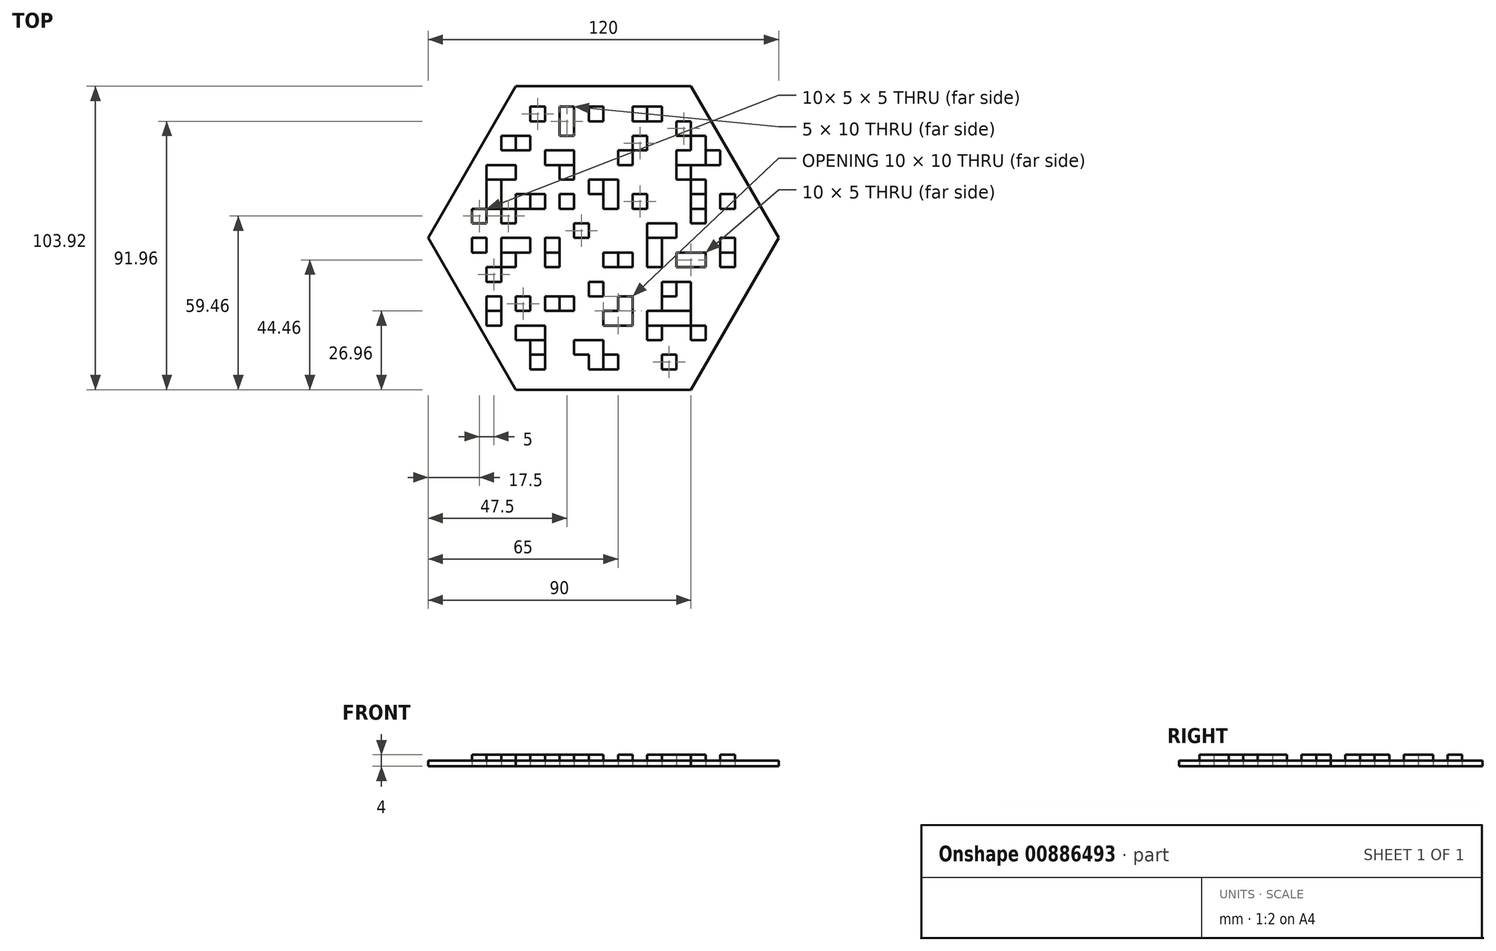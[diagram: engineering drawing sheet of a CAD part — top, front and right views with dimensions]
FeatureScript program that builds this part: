
annotation { "Feature Type Name" : "Feature", "Feature Type Description" : "" }
export const myFeature = defineFeature(function(context is Context, id is Id, definition is map)
    precondition{}
    {
        {
            var Q0;
            Q0=qCreatedBy(makeId("Top.planeOp"),FACE);
            var sketch = newSketch(context, id + "F0", { "sketchPlane" : qUnion([Q0])});
            skCircle(sketch, "E0.cCircle", {"center": v(0, 0) * mm, "radius": 60 * mm, "construction": true});
            skLineSegment(sketch, "E0.0", {"start": v(-60, 0) * mm, "end": v(-30, 51.96) * mm});
            skLineSegment(sketch, "E0.1", {"start": v(-30, 51.96) * mm, "end": v(30, 51.96) * mm});
            skLineSegment(sketch, "E0.2", {"start": v(30, 51.96) * mm, "end": v(60, 0) * mm});
            skLineSegment(sketch, "E0.3", {"start": v(60, 0) * mm, "end": v(30, -51.96) * mm});
            skLineSegment(sketch, "E0.4", {"start": v(30, -51.96) * mm, "end": v(-30, -51.96) * mm});
            skLineSegment(sketch, "E0.5", {"start": v(-30, -51.96) * mm, "end": v(-60, 0) * mm});
            skLineSegment(sketch, "E1", {"start": v(-60, 0) * mm, "end": v(60, 0) * mm});
            skLineSegment(sketch, "E2.0.9.0", {"start": v(-34.02, 45) * mm, "end": v(34.02, 45) * mm});
            skLineSegment(sketch, "E3.trimOffspring", {"start": v(-34.02, -45) * mm, "end": v(34.02, -45) * mm});
            skLineSegment(sketch, "E4.trimOffspring", {"start": v(-36.9, -40) * mm, "end": v(36.9, -40) * mm});
            skLineSegment(sketch, "E5.trimOffspring", {"start": v(-39.8, -35) * mm, "end": v(39.8, -35) * mm});
            skLineSegment(sketch, "E6.trimOffspring", {"start": v(-42.68, -30) * mm, "end": v(42.68, -30) * mm});
            skLineSegment(sketch, "E7.trimOffspring", {"start": v(-45.57, -25) * mm, "end": v(45.57, -25) * mm});
            skLineSegment(sketch, "E8.trimOffspring", {"start": v(-48.45, -20) * mm, "end": v(48.45, -20) * mm});
            skLineSegment(sketch, "E9.trimOffspring", {"start": v(-51.34, -15) * mm, "end": v(51.34, -15) * mm});
            skLineSegment(sketch, "E10.trimOffspring", {"start": v(-54.23, -10) * mm, "end": v(54.23, -10) * mm});
            skLineSegment(sketch, "E11.trimOffspring", {"start": v(-57.11, -5) * mm, "end": v(57.11, -5) * mm});
            skLineSegment(sketch, "E12.trimOffspring", {"start": v(-57.11, 5) * mm, "end": v(57.11, 5) * mm});
            skLineSegment(sketch, "E13.trimOffspring", {"start": v(-54.23, 10) * mm, "end": v(54.23, 10) * mm});
            skLineSegment(sketch, "E14.trimOffspring", {"start": v(-51.34, 15) * mm, "end": v(51.34, 15) * mm});
            skLineSegment(sketch, "E15.trimOffspring", {"start": v(-48.45, 20) * mm, "end": v(48.45, 20) * mm});
            skLineSegment(sketch, "E16.trimOffspring", {"start": v(-45.57, 25) * mm, "end": v(45.57, 25) * mm});
            skLineSegment(sketch, "E17.trimOffspring", {"start": v(-42.68, 30) * mm, "end": v(42.68, 30) * mm});
            skLineSegment(sketch, "E18.trimOffspring", {"start": v(-39.8, 35) * mm, "end": v(39.8, 35) * mm});
            skLineSegment(sketch, "E19.trimOffspring", {"start": v(-36.9, 40) * mm, "end": v(36.9, 40) * mm});
            skLineSegment(sketch, "E20", {"start": v(0, 51.96) * mm, "end": v(0, -51.96) * mm});
            skLineSegment(sketch, "E21.1.0.0", {"start": v(5, 51.96) * mm, "end": v(5, -51.96) * mm});
            skLineSegment(sketch, "E21.2.0.0", {"start": v(10, 51.96) * mm, "end": v(10, -51.96) * mm});
            skLineSegment(sketch, "E21.3.0.0", {"start": v(15, 51.96) * mm, "end": v(15, -51.96) * mm});
            skLineSegment(sketch, "E21.4.0.0", {"start": v(20, 51.96) * mm, "end": v(20, -51.96) * mm});
            skLineSegment(sketch, "E21.5.0.0", {"start": v(25, 51.96) * mm, "end": v(25, -51.96) * mm});
            skLineSegment(sketch, "E21.6.0.0", {"start": v(30, 51.96) * mm, "end": v(30, -51.96) * mm});
            skLineSegment(sketch, "E21.direction1", {"start": v(0, -51.96) * mm, "end": v(5, -51.96) * mm, "construction": true});
            skLineSegment(sketch, "E22.1.0.0", {"start": v(-5, 51.96) * mm, "end": v(-5, -51.96) * mm});
            skLineSegment(sketch, "E22.2.0.0", {"start": v(-10, 51.96) * mm, "end": v(-10, -51.96) * mm});
            skLineSegment(sketch, "E22.3.0.0", {"start": v(-15, 51.96) * mm, "end": v(-15, -51.96) * mm});
            skLineSegment(sketch, "E22.4.0.0", {"start": v(-20, 51.96) * mm, "end": v(-20, -51.96) * mm});
            skLineSegment(sketch, "E22.5.0.0", {"start": v(-25, 51.96) * mm, "end": v(-25, -51.96) * mm});
            skLineSegment(sketch, "E22.6.0.0", {"start": v(-30, 51.96) * mm, "end": v(-30, -51.96) * mm});
            skLineSegment(sketch, "E22.8.0.0", {"start": v(-40, 34.64) * mm, "end": v(-40, -34.64) * mm});
            skLineSegment(sketch, "E22.9.0.0", {"start": v(-45, 25.98) * mm, "end": v(-45, -25.98) * mm});
            skLineSegment(sketch, "E22.direction1", {"start": v(0, -51.96) * mm, "end": v(-5, -51.96) * mm, "construction": true});
            skLineSegment(sketch, "E23.trimOffspring", {"start": v(-35, 43.3) * mm, "end": v(-35, -43.3) * mm});
            skLineSegment(sketch, "E24.trimOffspring", {"start": v(45, 25.98) * mm, "end": v(45, -25.98) * mm});
            skLineSegment(sketch, "E25.trimOffspring", {"start": v(40, 34.64) * mm, "end": v(40, -34.64) * mm});
            skLineSegment(sketch, "E26.trimOffspring", {"start": v(35, 43.3) * mm, "end": v(35, -43.3) * mm});
            skSolve(sketch);
        }
        {
            var Q0;
            {var subQ0=sQuery(id+"F0.wireOp",EDGE,"E21.5.0.0");var subQ1=sQuery(id+"F0.wireOp",EDGE,"E1");var subQ2=makeQuery(id+"F0.imprint","INTERSECT",VERTEX,{"derivedFrom":[subQ1,subQ0]});Q0=makeQuery(id+"F0.imprint","IMPRINT",FACE,{"disambiguationData":[TD([[makeQuery(id+"F0.imprint","IMPRINT",EDGE,{"disambiguationData":[TD([[subQ2,-1.0]])],"derivedFrom":subQ1}),1.0]])]});}
            var Q1;
            {var subQ0=sQuery(id+"F0.wireOp",EDGE,"E21.2.0.0");var subQ1=sQuery(id+"F0.wireOp",EDGE,"E13.trimOffspring");var subQ2=makeQuery(id+"F0.imprint","INTERSECT",VERTEX,{"derivedFrom":[subQ1,subQ0]});Q1=makeQuery(id+"F0.imprint","IMPRINT",FACE,{"disambiguationData":[TD([[makeQuery(id+"F0.imprint","IMPRINT",EDGE,{"disambiguationData":[TD([[subQ2,-1.0]])],"derivedFrom":subQ1}),1.0]])]});}
            var Q2;
            {var subQ0=sQuery(id+"F0.wireOp",EDGE,"E21.1.0.0");var subQ1=sQuery(id+"F0.wireOp",EDGE,"E12.trimOffspring");var subQ2=makeQuery(id+"F0.imprint","INTERSECT",VERTEX,{"derivedFrom":[subQ1,subQ0]});Q2=makeQuery(id+"F0.imprint","IMPRINT",FACE,{"disambiguationData":[TD([[makeQuery(id+"F0.imprint","IMPRINT",EDGE,{"disambiguationData":[TD([[subQ2,-1.0]])],"derivedFrom":subQ1}),1.0]])]});}
            var Q3;
            {var subQ0=sQuery(id+"F0.wireOp",EDGE,"E21.1.0.0");var subQ1=sQuery(id+"F0.wireOp",EDGE,"E13.trimOffspring");var subQ2=makeQuery(id+"F0.imprint","INTERSECT",VERTEX,{"derivedFrom":[subQ1,subQ0]});Q3=makeQuery(id+"F0.imprint","IMPRINT",FACE,{"disambiguationData":[TD([[makeQuery(id+"F0.imprint","IMPRINT",EDGE,{"disambiguationData":[TD([[subQ2,-1.0]])],"derivedFrom":subQ1}),1.0]])]});}
            var Q4;
            {var subQ0=sQuery(id+"F0.wireOp",EDGE,"E22.4.0.0");var subQ1=sQuery(id+"F0.wireOp",EDGE,"E16.trimOffspring");var subQ2=makeQuery(id+"F0.imprint","INTERSECT",VERTEX,{"derivedFrom":[subQ1,subQ0]});Q4=makeQuery(id+"F0.imprint","IMPRINT",FACE,{"disambiguationData":[TD([[makeQuery(id+"F0.imprint","IMPRINT",EDGE,{"disambiguationData":[TD([[subQ2,-1.0]])],"derivedFrom":subQ1}),1.0]])]});}
            var Q5;
            {var subQ0=sQuery(id+"F0.wireOp",EDGE,"E21.2.0.0");var subQ1=sQuery(id+"F0.wireOp",EDGE,"E12.trimOffspring");var subQ2=makeQuery(id+"F0.imprint","INTERSECT",VERTEX,{"derivedFrom":[subQ1,subQ0]});Q5=makeQuery(id+"F0.imprint","IMPRINT",FACE,{"disambiguationData":[TD([[makeQuery(id+"F0.imprint","IMPRINT",EDGE,{"disambiguationData":[TD([[subQ2,-1.0]])],"derivedFrom":subQ1}),1.0]])]});}
            var Q6;
            {var subQ0=sQuery(id+"F0.wireOp",EDGE,"E21.2.0.0");var subQ1=sQuery(id+"F0.wireOp",EDGE,"E17.trimOffspring");var subQ2=makeQuery(id+"F0.imprint","INTERSECT",VERTEX,{"derivedFrom":[subQ1,subQ0]});Q6=makeQuery(id+"F0.imprint","IMPRINT",FACE,{"disambiguationData":[TD([[makeQuery(id+"F0.imprint","IMPRINT",EDGE,{"disambiguationData":[TD([[subQ2,-1.0]])],"derivedFrom":subQ1}),1.0]])]});}
            var Q7;
            {var subQ0=sQuery(id+"F0.wireOp",EDGE,"E20");var subQ1=sQuery(id+"F0.wireOp",EDGE,"E8.trimOffspring");var subQ2=makeQuery(id+"F0.imprint","INTERSECT",VERTEX,{"derivedFrom":[subQ1,subQ0]});Q7=makeQuery(id+"F0.imprint","IMPRINT",FACE,{"disambiguationData":[TD([[makeQuery(id+"F0.imprint","IMPRINT",EDGE,{"disambiguationData":[TD([[subQ2,-1.0]])],"derivedFrom":subQ1}),1.0]])]});}
            var Q8;
            {var subQ0=sQuery(id+"F0.wireOp",EDGE,"E21.1.0.0");var subQ1=sQuery(id+"F0.wireOp",EDGE,"E4.trimOffspring");var subQ2=makeQuery(id+"F0.imprint","INTERSECT",VERTEX,{"derivedFrom":[subQ1,subQ0]});Q8=makeQuery(id+"F0.imprint","IMPRINT",FACE,{"disambiguationData":[TD([[makeQuery(id+"F0.imprint","IMPRINT",EDGE,{"disambiguationData":[TD([[subQ2,-1.0]])],"derivedFrom":subQ1}),1.0]])]});}
            var Q9;
            {var subQ0=sQuery(id+"F0.wireOp",EDGE,"E21.2.0.0");var subQ1=sQuery(id+"F0.wireOp",EDGE,"E1");var subQ2=makeQuery(id+"F0.imprint","INTERSECT",VERTEX,{"derivedFrom":[subQ1,subQ0]});Q9=makeQuery(id+"F0.imprint","IMPRINT",FACE,{"disambiguationData":[TD([[makeQuery(id+"F0.imprint","IMPRINT",EDGE,{"disambiguationData":[TD([[subQ2,-1.0]])],"derivedFrom":subQ1}),-1.0]])]});}
            var Q10;
            {var subQ0=sQuery(id+"F0.wireOp",EDGE,"E21.3.0.0");var subQ1=sQuery(id+"F0.wireOp",EDGE,"E13.trimOffspring");var subQ2=makeQuery(id+"F0.imprint","INTERSECT",VERTEX,{"derivedFrom":[subQ1,subQ0]});Q10=makeQuery(id+"F0.imprint","IMPRINT",FACE,{"disambiguationData":[TD([[makeQuery(id+"F0.imprint","IMPRINT",EDGE,{"disambiguationData":[TD([[subQ2,-1.0]])],"derivedFrom":subQ1}),1.0]])]});}
            var Q11;
            {var subQ0=sQuery(id+"F0.wireOp",EDGE,"E22.2.0.0");var subQ1=sQuery(id+"F0.wireOp",EDGE,"E6.trimOffspring");var subQ2=makeQuery(id+"F0.imprint","INTERSECT",VERTEX,{"derivedFrom":[subQ1,subQ0]});Q11=makeQuery(id+"F0.imprint","IMPRINT",FACE,{"disambiguationData":[TD([[makeQuery(id+"F0.imprint","IMPRINT",EDGE,{"disambiguationData":[TD([[subQ2,-1.0]])],"derivedFrom":subQ1}),1.0]])]});}
            var Q12;
            {var subQ0=sQuery(id+"F0.wireOp",EDGE,"E21.1.0.0");var subQ1=sQuery(id+"F0.wireOp",EDGE,"E1");var subQ2=makeQuery(id+"F0.imprint","INTERSECT",VERTEX,{"derivedFrom":[subQ1,subQ0]});Q12=makeQuery(id+"F0.imprint","IMPRINT",FACE,{"disambiguationData":[TD([[makeQuery(id+"F0.imprint","IMPRINT",EDGE,{"disambiguationData":[TD([[subQ2,-1.0]])],"derivedFrom":subQ1}),-1.0]])]});}
            var Q13;
            {var subQ0=sQuery(id+"F0.wireOp",EDGE,"E21.2.0.0");var subQ1=sQuery(id+"F0.wireOp",EDGE,"E10.trimOffspring");var subQ2=makeQuery(id+"F0.imprint","INTERSECT",VERTEX,{"derivedFrom":[subQ1,subQ0]});Q13=makeQuery(id+"F0.imprint","IMPRINT",FACE,{"disambiguationData":[TD([[makeQuery(id+"F0.imprint","IMPRINT",EDGE,{"disambiguationData":[TD([[subQ2,-1.0]])],"derivedFrom":subQ1}),1.0]])]});}
            var Q14;
            {var subQ0=sQuery(id+"F0.wireOp",EDGE,"E22.3.0.0");var subQ1=sQuery(id+"F0.wireOp",EDGE,"E2.0.9.0");var subQ2=makeQuery(id+"F0.imprint","INTERSECT",VERTEX,{"derivedFrom":[subQ1,subQ0]});Q14=makeQuery(id+"F0.imprint","IMPRINT",FACE,{"disambiguationData":[TD([[makeQuery(id+"F0.imprint","IMPRINT",EDGE,{"disambiguationData":[TD([[subQ2,-1.0]])],"derivedFrom":subQ1}),-1.0]])]});}
            var Q15;
            {var subQ0=sQuery(id+"F0.wireOp",EDGE,"E22.3.0.0");var subQ1=sQuery(id+"F0.wireOp",EDGE,"E12.trimOffspring");var subQ2=makeQuery(id+"F0.imprint","INTERSECT",VERTEX,{"derivedFrom":[subQ1,subQ0]});Q15=makeQuery(id+"F0.imprint","IMPRINT",FACE,{"disambiguationData":[TD([[makeQuery(id+"F0.imprint","IMPRINT",EDGE,{"disambiguationData":[TD([[subQ2,-1.0]])],"derivedFrom":subQ1}),1.0]])]});}
            var Q16;
            {var subQ0=sQuery(id+"F0.wireOp",EDGE,"E20");var subQ1=sQuery(id+"F0.wireOp",EDGE,"E16.trimOffspring");var subQ2=makeQuery(id+"F0.imprint","INTERSECT",VERTEX,{"derivedFrom":[subQ1,subQ0]});Q16=makeQuery(id+"F0.imprint","IMPRINT",FACE,{"disambiguationData":[TD([[makeQuery(id+"F0.imprint","IMPRINT",EDGE,{"disambiguationData":[TD([[subQ2,-1.0]])],"derivedFrom":subQ1}),1.0]])]});}
            var Q17;
            {var subQ0=sQuery(id+"F0.wireOp",EDGE,"E20");var subQ1=sQuery(id+"F0.wireOp",EDGE,"E18.trimOffspring");var subQ2=makeQuery(id+"F0.imprint","INTERSECT",VERTEX,{"derivedFrom":[subQ1,subQ0]});Q17=makeQuery(id+"F0.imprint","IMPRINT",FACE,{"disambiguationData":[TD([[makeQuery(id+"F0.imprint","IMPRINT",EDGE,{"disambiguationData":[TD([[subQ2,-1.0]])],"derivedFrom":subQ1}),1.0]])]});}
            var Q18;
            {var subQ0=sQuery(id+"F0.wireOp",EDGE,"E20");var subQ1=sQuery(id+"F0.wireOp",EDGE,"E5.trimOffspring");var subQ2=makeQuery(id+"F0.imprint","INTERSECT",VERTEX,{"derivedFrom":[subQ1,subQ0]});Q18=makeQuery(id+"F0.imprint","IMPRINT",FACE,{"disambiguationData":[TD([[makeQuery(id+"F0.imprint","IMPRINT",EDGE,{"disambiguationData":[TD([[subQ2,-1.0]])],"derivedFrom":subQ1}),1.0]])]});}
            var Q19;
            {var subQ0=sQuery(id+"F0.wireOp",EDGE,"E21.2.0.0");var subQ1=sQuery(id+"F0.wireOp",EDGE,"E8.trimOffspring");var subQ2=makeQuery(id+"F0.imprint","INTERSECT",VERTEX,{"derivedFrom":[subQ1,subQ0]});Q19=makeQuery(id+"F0.imprint","IMPRINT",FACE,{"disambiguationData":[TD([[makeQuery(id+"F0.imprint","IMPRINT",EDGE,{"disambiguationData":[TD([[subQ2,-1.0]])],"derivedFrom":subQ1}),1.0]])]});}
            var Q20;
            {var subQ0=sQuery(id+"F0.wireOp",EDGE,"E22.2.0.0");var subQ1=sQuery(id+"F0.wireOp",EDGE,"E10.trimOffspring");var subQ2=makeQuery(id+"F0.imprint","INTERSECT",VERTEX,{"derivedFrom":[subQ1,subQ0]});Q20=makeQuery(id+"F0.imprint","IMPRINT",FACE,{"disambiguationData":[TD([[makeQuery(id+"F0.imprint","IMPRINT",EDGE,{"disambiguationData":[TD([[subQ2,-1.0]])],"derivedFrom":subQ1}),1.0]])]});}
            var Q21;
            {var subQ0=sQuery(id+"F0.wireOp",EDGE,"E22.1.0.0");var subQ1=sQuery(id+"F0.wireOp",EDGE,"E9.trimOffspring");var subQ2=makeQuery(id+"F0.imprint","INTERSECT",VERTEX,{"derivedFrom":[subQ1,subQ0]});Q21=makeQuery(id+"F0.imprint","IMPRINT",FACE,{"disambiguationData":[TD([[makeQuery(id+"F0.imprint","IMPRINT",EDGE,{"disambiguationData":[TD([[subQ2,-1.0]])],"derivedFrom":subQ1}),1.0]])]});}
            var Q22;
            {var subQ0=sQuery(id+"F0.wireOp",EDGE,"E22.4.0.0");var subQ1=sQuery(id+"F0.wireOp",EDGE,"E1");var subQ2=makeQuery(id+"F0.imprint","INTERSECT",VERTEX,{"derivedFrom":[subQ1,subQ0]});Q22=makeQuery(id+"F0.imprint","IMPRINT",FACE,{"disambiguationData":[TD([[makeQuery(id+"F0.imprint","IMPRINT",EDGE,{"disambiguationData":[TD([[subQ2,-1.0]])],"derivedFrom":subQ1}),-1.0]])]});}
            var Q23;
            {var subQ0=sQuery(id+"F0.wireOp",EDGE,"E21.3.0.0");var subQ1=sQuery(id+"F0.wireOp",EDGE,"E16.trimOffspring");var subQ2=makeQuery(id+"F0.imprint","INTERSECT",VERTEX,{"derivedFrom":[subQ1,subQ0]});Q23=makeQuery(id+"F0.imprint","IMPRINT",FACE,{"disambiguationData":[TD([[makeQuery(id+"F0.imprint","IMPRINT",EDGE,{"disambiguationData":[TD([[subQ2,-1.0]])],"derivedFrom":subQ1}),1.0]])]});}
            var Q24;
            {var subQ0=sQuery(id+"F0.wireOp",EDGE,"E21.1.0.0");var subQ1=sQuery(id+"F0.wireOp",EDGE,"E15.trimOffspring");var subQ2=makeQuery(id+"F0.imprint","INTERSECT",VERTEX,{"derivedFrom":[subQ1,subQ0]});Q24=makeQuery(id+"F0.imprint","IMPRINT",FACE,{"disambiguationData":[TD([[makeQuery(id+"F0.imprint","IMPRINT",EDGE,{"disambiguationData":[TD([[subQ2,-1.0]])],"derivedFrom":subQ1}),1.0]])]});}
            var Q25;
            {var subQ0=sQuery(id+"F0.wireOp",EDGE,"E22.5.0.0");var subQ1=sQuery(id+"F0.wireOp",EDGE,"E7.trimOffspring");var subQ2=makeQuery(id+"F0.imprint","INTERSECT",VERTEX,{"derivedFrom":[subQ1,subQ0]});Q25=makeQuery(id+"F0.imprint","IMPRINT",FACE,{"disambiguationData":[TD([[makeQuery(id+"F0.imprint","IMPRINT",EDGE,{"disambiguationData":[TD([[subQ2,-1.0]])],"derivedFrom":subQ1}),1.0]])]});}
            var Q26;
            {var subQ0=sQuery(id+"F0.wireOp",EDGE,"E20");var subQ1=sQuery(id+"F0.wireOp",EDGE,"E12.trimOffspring");var subQ2=makeQuery(id+"F0.imprint","INTERSECT",VERTEX,{"derivedFrom":[subQ1,subQ0]});Q26=makeQuery(id+"F0.imprint","IMPRINT",FACE,{"disambiguationData":[TD([[makeQuery(id+"F0.imprint","IMPRINT",EDGE,{"disambiguationData":[TD([[subQ2,-1.0]])],"derivedFrom":subQ1}),1.0]])]});}
            var Q27;
            {var subQ0=sQuery(id+"F0.wireOp",EDGE,"E22.2.0.0");var subQ1=sQuery(id+"F0.wireOp",EDGE,"E7.trimOffspring");var subQ2=makeQuery(id+"F0.imprint","INTERSECT",VERTEX,{"derivedFrom":[subQ1,subQ0]});Q27=makeQuery(id+"F0.imprint","IMPRINT",FACE,{"disambiguationData":[TD([[makeQuery(id+"F0.imprint","IMPRINT",EDGE,{"disambiguationData":[TD([[subQ2,-1.0]])],"derivedFrom":subQ1}),1.0]])]});}
            var Q28;
            {var subQ0=sQuery(id+"F0.wireOp",EDGE,"E22.1.0.0");var subQ1=sQuery(id+"F0.wireOp",EDGE,"E10.trimOffspring");var subQ2=makeQuery(id+"F0.imprint","INTERSECT",VERTEX,{"derivedFrom":[subQ1,subQ0]});Q28=makeQuery(id+"F0.imprint","IMPRINT",FACE,{"disambiguationData":[TD([[makeQuery(id+"F0.imprint","IMPRINT",EDGE,{"disambiguationData":[TD([[subQ2,-1.0]])],"derivedFrom":subQ1}),1.0]])]});}
            var Q29;
            {var subQ0=sQuery(id+"F0.wireOp",EDGE,"E21.3.0.0");var subQ1=sQuery(id+"F0.wireOp",EDGE,"E2.0.9.0");var subQ2=makeQuery(id+"F0.imprint","INTERSECT",VERTEX,{"derivedFrom":[subQ1,subQ0]});Q29=makeQuery(id+"F0.imprint","IMPRINT",FACE,{"disambiguationData":[TD([[makeQuery(id+"F0.imprint","IMPRINT",EDGE,{"disambiguationData":[TD([[subQ2,-1.0]])],"derivedFrom":subQ1}),-1.0]])]});}
            var Q30;
            {var subQ0=sQuery(id+"F0.wireOp",EDGE,"E21.2.0.0");var subQ1=sQuery(id+"F0.wireOp",EDGE,"E5.trimOffspring");var subQ2=makeQuery(id+"F0.imprint","INTERSECT",VERTEX,{"derivedFrom":[subQ1,subQ0]});Q30=makeQuery(id+"F0.imprint","IMPRINT",FACE,{"disambiguationData":[TD([[makeQuery(id+"F0.imprint","IMPRINT",EDGE,{"disambiguationData":[TD([[subQ2,-1.0]])],"derivedFrom":subQ1}),1.0]])]});}
            var Q31;
            {var subQ0=sQuery(id+"F0.wireOp",EDGE,"E21.5.0.0");var subQ1=sQuery(id+"F0.wireOp",EDGE,"E7.trimOffspring");var subQ2=makeQuery(id+"F0.imprint","INTERSECT",VERTEX,{"derivedFrom":[subQ1,subQ0]});Q31=makeQuery(id+"F0.imprint","IMPRINT",FACE,{"disambiguationData":[TD([[makeQuery(id+"F0.imprint","IMPRINT",EDGE,{"disambiguationData":[TD([[subQ2,-1.0]])],"derivedFrom":subQ1}),1.0]])]});}
            var Q32;
            {var subQ0=sQuery(id+"F0.wireOp",EDGE,"E21.4.0.0");var subQ1=sQuery(id+"F0.wireOp",EDGE,"E16.trimOffspring");var subQ2=makeQuery(id+"F0.imprint","INTERSECT",VERTEX,{"derivedFrom":[subQ1,subQ0]});Q32=makeQuery(id+"F0.imprint","IMPRINT",FACE,{"disambiguationData":[TD([[makeQuery(id+"F0.imprint","IMPRINT",EDGE,{"disambiguationData":[TD([[subQ2,-1.0]])],"derivedFrom":subQ1}),1.0]])]});}
            var Q33;
            {var subQ0=sQuery(id+"F0.wireOp",EDGE,"E20");var subQ1=sQuery(id+"F0.wireOp",EDGE,"E7.trimOffspring");var subQ2=makeQuery(id+"F0.imprint","INTERSECT",VERTEX,{"derivedFrom":[subQ1,subQ0]});Q33=makeQuery(id+"F0.imprint","IMPRINT",FACE,{"disambiguationData":[TD([[makeQuery(id+"F0.imprint","IMPRINT",EDGE,{"disambiguationData":[TD([[subQ2,-1.0]])],"derivedFrom":subQ1}),1.0]])]});}
            var Q34;
            {var subQ0=sQuery(id+"F0.wireOp",EDGE,"E22.3.0.0");var subQ1=sQuery(id+"F0.wireOp",EDGE,"E14.trimOffspring");var subQ2=makeQuery(id+"F0.imprint","INTERSECT",VERTEX,{"derivedFrom":[subQ1,subQ0]});Q34=makeQuery(id+"F0.imprint","IMPRINT",FACE,{"disambiguationData":[TD([[makeQuery(id+"F0.imprint","IMPRINT",EDGE,{"disambiguationData":[TD([[subQ2,-1.0]])],"derivedFrom":subQ1}),1.0]])]});}
            var Q35;
            {var subQ0=sQuery(id+"F0.wireOp",EDGE,"E21.4.0.0");var subQ1=sQuery(id+"F0.wireOp",EDGE,"E4.trimOffspring");var subQ2=makeQuery(id+"F0.imprint","INTERSECT",VERTEX,{"derivedFrom":[subQ1,subQ0]});Q35=makeQuery(id+"F0.imprint","IMPRINT",FACE,{"disambiguationData":[TD([[makeQuery(id+"F0.imprint","IMPRINT",EDGE,{"disambiguationData":[TD([[subQ2,-1.0]])],"derivedFrom":subQ1}),1.0]])]});}
            var Q36;
            {var subQ0=sQuery(id+"F0.wireOp",EDGE,"E20");var subQ1=sQuery(id+"F0.wireOp",EDGE,"E10.trimOffspring");var subQ2=makeQuery(id+"F0.imprint","INTERSECT",VERTEX,{"derivedFrom":[subQ1,subQ0]});Q36=makeQuery(id+"F0.imprint","IMPRINT",FACE,{"disambiguationData":[TD([[makeQuery(id+"F0.imprint","IMPRINT",EDGE,{"disambiguationData":[TD([[subQ2,-1.0]])],"derivedFrom":subQ1}),1.0]])]});}
            var Q37;
            {var subQ0=sQuery(id+"F0.wireOp",EDGE,"E21.5.0.0");var subQ1=sQuery(id+"F0.wireOp",EDGE,"E18.trimOffspring");var subQ2=makeQuery(id+"F0.imprint","INTERSECT",VERTEX,{"derivedFrom":[subQ1,subQ0]});Q37=makeQuery(id+"F0.imprint","IMPRINT",FACE,{"disambiguationData":[TD([[makeQuery(id+"F0.imprint","IMPRINT",EDGE,{"disambiguationData":[TD([[subQ2,-1.0]])],"derivedFrom":subQ1}),1.0]])]});}
            var Q38;
            {var subQ0=sQuery(id+"F0.wireOp",EDGE,"E20");var subQ1=sQuery(id+"F0.wireOp",EDGE,"E9.trimOffspring");var subQ2=makeQuery(id+"F0.imprint","INTERSECT",VERTEX,{"derivedFrom":[subQ1,subQ0]});Q38=makeQuery(id+"F0.imprint","IMPRINT",FACE,{"disambiguationData":[TD([[makeQuery(id+"F0.imprint","IMPRINT",EDGE,{"disambiguationData":[TD([[subQ2,-1.0]])],"derivedFrom":subQ1}),1.0]])]});}
            var Q39;
            {var subQ0=sQuery(id+"F0.wireOp",EDGE,"E22.2.0.0");var subQ1=sQuery(id+"F0.wireOp",EDGE,"E14.trimOffspring");var subQ2=makeQuery(id+"F0.imprint","INTERSECT",VERTEX,{"derivedFrom":[subQ1,subQ0]});Q39=makeQuery(id+"F0.imprint","IMPRINT",FACE,{"disambiguationData":[TD([[makeQuery(id+"F0.imprint","IMPRINT",EDGE,{"disambiguationData":[TD([[subQ2,-1.0]])],"derivedFrom":subQ1}),1.0]])]});}
            var Q40;
            {var subQ0=sQuery(id+"F0.wireOp",EDGE,"E21.5.0.0");var subQ1=sQuery(id+"F0.wireOp",EDGE,"E12.trimOffspring");var subQ2=makeQuery(id+"F0.imprint","INTERSECT",VERTEX,{"derivedFrom":[subQ1,subQ0]});Q40=makeQuery(id+"F0.imprint","IMPRINT",FACE,{"disambiguationData":[TD([[makeQuery(id+"F0.imprint","IMPRINT",EDGE,{"disambiguationData":[TD([[subQ2,-1.0]])],"derivedFrom":subQ1}),1.0]])]});}
            var Q41;
            {var subQ0=sQuery(id+"F0.wireOp",EDGE,"E21.3.0.0");var subQ1=sQuery(id+"F0.wireOp",EDGE,"E5.trimOffspring");var subQ2=makeQuery(id+"F0.imprint","INTERSECT",VERTEX,{"derivedFrom":[subQ1,subQ0]});Q41=makeQuery(id+"F0.imprint","IMPRINT",FACE,{"disambiguationData":[TD([[makeQuery(id+"F0.imprint","IMPRINT",EDGE,{"disambiguationData":[TD([[subQ2,-1.0]])],"derivedFrom":subQ1}),1.0]])]});}
            var Q42;
            {var subQ0=sQuery(id+"F0.wireOp",EDGE,"E22.3.0.0");var subQ1=sQuery(id+"F0.wireOp",EDGE,"E1");var subQ2=makeQuery(id+"F0.imprint","INTERSECT",VERTEX,{"derivedFrom":[subQ1,subQ0]});Q42=makeQuery(id+"F0.imprint","IMPRINT",FACE,{"disambiguationData":[TD([[makeQuery(id+"F0.imprint","IMPRINT",EDGE,{"disambiguationData":[TD([[subQ2,-1.0]])],"derivedFrom":subQ1}),1.0]])]});}
            var Q43;
            {var subQ0=sQuery(id+"F0.wireOp",EDGE,"E21.5.0.0");var subQ1=sQuery(id+"F0.wireOp",EDGE,"E1");var subQ2=makeQuery(id+"F0.imprint","INTERSECT",VERTEX,{"derivedFrom":[subQ1,subQ0]});Q43=makeQuery(id+"F0.imprint","IMPRINT",FACE,{"disambiguationData":[TD([[makeQuery(id+"F0.imprint","IMPRINT",EDGE,{"disambiguationData":[TD([[subQ2,-1.0]])],"derivedFrom":subQ1}),-1.0]])]});}
            var Q44;
            {var subQ0=sQuery(id+"F0.wireOp",EDGE,"E21.2.0.0");var subQ1=sQuery(id+"F0.wireOp",EDGE,"E2.0.9.0");var subQ2=makeQuery(id+"F0.imprint","INTERSECT",VERTEX,{"derivedFrom":[subQ1,subQ0]});Q44=makeQuery(id+"F0.imprint","IMPRINT",FACE,{"disambiguationData":[TD([[makeQuery(id+"F0.imprint","IMPRINT",EDGE,{"disambiguationData":[TD([[subQ2,-1.0]])],"derivedFrom":subQ1}),-1.0]])]});}
            var Q45;
            {var subQ0=sQuery(id+"F0.wireOp",EDGE,"E21.4.0.0");var subQ1=sQuery(id+"F0.wireOp",EDGE,"E10.trimOffspring");var subQ2=makeQuery(id+"F0.imprint","INTERSECT",VERTEX,{"derivedFrom":[subQ1,subQ0]});Q45=makeQuery(id+"F0.imprint","IMPRINT",FACE,{"disambiguationData":[TD([[makeQuery(id+"F0.imprint","IMPRINT",EDGE,{"disambiguationData":[TD([[subQ2,-1.0]])],"derivedFrom":subQ1}),1.0]])]});}
            var Q46;
            {var subQ0=sQuery(id+"F0.wireOp",EDGE,"E22.2.0.0");var subQ1=sQuery(id+"F0.wireOp",EDGE,"E2.0.9.0");var subQ2=makeQuery(id+"F0.imprint","INTERSECT",VERTEX,{"derivedFrom":[subQ1,subQ0]});Q46=makeQuery(id+"F0.imprint","IMPRINT",FACE,{"disambiguationData":[TD([[makeQuery(id+"F0.imprint","IMPRINT",EDGE,{"disambiguationData":[TD([[subQ2,-1.0]])],"derivedFrom":subQ1}),-1.0]])]});}
            var Q47;
            {var subQ0=sQuery(id+"F0.wireOp",EDGE,"E21.2.0.0");var subQ1=sQuery(id+"F0.wireOp",EDGE,"E7.trimOffspring");var subQ2=makeQuery(id+"F0.imprint","INTERSECT",VERTEX,{"derivedFrom":[subQ1,subQ0]});Q47=makeQuery(id+"F0.imprint","IMPRINT",FACE,{"disambiguationData":[TD([[makeQuery(id+"F0.imprint","IMPRINT",EDGE,{"disambiguationData":[TD([[subQ2,-1.0]])],"derivedFrom":subQ1}),1.0]])]});}
            var Q48;
            {var subQ0=sQuery(id+"F0.wireOp",EDGE,"E22.4.0.0");var subQ1=sQuery(id+"F0.wireOp",EDGE,"E15.trimOffspring");var subQ2=makeQuery(id+"F0.imprint","INTERSECT",VERTEX,{"derivedFrom":[subQ1,subQ0]});Q48=makeQuery(id+"F0.imprint","IMPRINT",FACE,{"disambiguationData":[TD([[makeQuery(id+"F0.imprint","IMPRINT",EDGE,{"disambiguationData":[TD([[subQ2,-1.0]])],"derivedFrom":subQ1}),1.0]])]});}
            var Q49;
            {var subQ0=sQuery(id+"F0.wireOp",EDGE,"E21.3.0.0");var subQ1=sQuery(id+"F0.wireOp",EDGE,"E12.trimOffspring");var subQ2=makeQuery(id+"F0.imprint","INTERSECT",VERTEX,{"derivedFrom":[subQ1,subQ0]});Q49=makeQuery(id+"F0.imprint","IMPRINT",FACE,{"disambiguationData":[TD([[makeQuery(id+"F0.imprint","IMPRINT",EDGE,{"disambiguationData":[TD([[subQ2,-1.0]])],"derivedFrom":subQ1}),1.0]])]});}
            var Q50;
            {var subQ0=sQuery(id+"F0.wireOp",EDGE,"E20");var subQ1=sQuery(id+"F0.wireOp",EDGE,"E6.trimOffspring");var subQ2=makeQuery(id+"F0.imprint","INTERSECT",VERTEX,{"derivedFrom":[subQ1,subQ0]});Q50=makeQuery(id+"F0.imprint","IMPRINT",FACE,{"disambiguationData":[TD([[makeQuery(id+"F0.imprint","IMPRINT",EDGE,{"disambiguationData":[TD([[subQ2,-1.0]])],"derivedFrom":subQ1}),1.0]])]});}
            var Q51;
            {var subQ0=sQuery(id+"F0.wireOp",EDGE,"E20");var subQ1=sQuery(id+"F0.wireOp",EDGE,"E14.trimOffspring");var subQ2=makeQuery(id+"F0.imprint","INTERSECT",VERTEX,{"derivedFrom":[subQ1,subQ0]});Q51=makeQuery(id+"F0.imprint","IMPRINT",FACE,{"disambiguationData":[TD([[makeQuery(id+"F0.imprint","IMPRINT",EDGE,{"disambiguationData":[TD([[subQ2,-1.0]])],"derivedFrom":subQ1}),1.0]])]});}
            var Q52;
            {var subQ0=sQuery(id+"F0.wireOp",EDGE,"E22.1.0.0");var subQ1=sQuery(id+"F0.wireOp",EDGE,"E8.trimOffspring");var subQ2=makeQuery(id+"F0.imprint","INTERSECT",VERTEX,{"derivedFrom":[subQ1,subQ0]});Q52=makeQuery(id+"F0.imprint","IMPRINT",FACE,{"disambiguationData":[TD([[makeQuery(id+"F0.imprint","IMPRINT",EDGE,{"disambiguationData":[TD([[subQ2,-1.0]])],"derivedFrom":subQ1}),1.0]])]});}
            var Q53;
            {var subQ0=sQuery(id+"F0.wireOp",EDGE,"E22.5.0.0");var subQ1=sQuery(id+"F0.wireOp",EDGE,"E9.trimOffspring");var subQ2=makeQuery(id+"F0.imprint","INTERSECT",VERTEX,{"derivedFrom":[subQ1,subQ0]});Q53=makeQuery(id+"F0.imprint","IMPRINT",FACE,{"disambiguationData":[TD([[makeQuery(id+"F0.imprint","IMPRINT",EDGE,{"disambiguationData":[TD([[subQ2,-1.0]])],"derivedFrom":subQ1}),1.0]])]});}
            var Q54;
            {var subQ0=sQuery(id+"F0.wireOp",EDGE,"E21.1.0.0");var subQ1=sQuery(id+"F0.wireOp",EDGE,"E16.trimOffspring");var subQ2=makeQuery(id+"F0.imprint","INTERSECT",VERTEX,{"derivedFrom":[subQ1,subQ0]});Q54=makeQuery(id+"F0.imprint","IMPRINT",FACE,{"disambiguationData":[TD([[makeQuery(id+"F0.imprint","IMPRINT",EDGE,{"disambiguationData":[TD([[subQ2,-1.0]])],"derivedFrom":subQ1}),1.0]])]});}
            var Q55;
            {var subQ0=sQuery(id+"F0.wireOp",EDGE,"E21.1.0.0");var subQ1=sQuery(id+"F0.wireOp",EDGE,"E1");var subQ2=makeQuery(id+"F0.imprint","INTERSECT",VERTEX,{"derivedFrom":[subQ1,subQ0]});Q55=makeQuery(id+"F0.imprint","IMPRINT",FACE,{"disambiguationData":[TD([[makeQuery(id+"F0.imprint","IMPRINT",EDGE,{"disambiguationData":[TD([[subQ2,-1.0]])],"derivedFrom":subQ1}),1.0]])]});}
            var Q56;
            {var subQ0=sQuery(id+"F0.wireOp",EDGE,"E21.3.0.0");var subQ1=sQuery(id+"F0.wireOp",EDGE,"E6.trimOffspring");var subQ2=makeQuery(id+"F0.imprint","INTERSECT",VERTEX,{"derivedFrom":[subQ1,subQ0]});Q56=makeQuery(id+"F0.imprint","IMPRINT",FACE,{"disambiguationData":[TD([[makeQuery(id+"F0.imprint","IMPRINT",EDGE,{"disambiguationData":[TD([[subQ2,-1.0]])],"derivedFrom":subQ1}),1.0]])]});}
            var Q57;
            {var subQ0=sQuery(id+"F0.wireOp",EDGE,"E22.3.0.0");var subQ1=sQuery(id+"F0.wireOp",EDGE,"E6.trimOffspring");var subQ2=makeQuery(id+"F0.imprint","INTERSECT",VERTEX,{"derivedFrom":[subQ1,subQ0]});Q57=makeQuery(id+"F0.imprint","IMPRINT",FACE,{"disambiguationData":[TD([[makeQuery(id+"F0.imprint","IMPRINT",EDGE,{"disambiguationData":[TD([[subQ2,-1.0]])],"derivedFrom":subQ1}),1.0]])]});}
            var Q58;
            {var subQ0=sQuery(id+"F0.wireOp",EDGE,"E21.3.0.0");var subQ1=sQuery(id+"F0.wireOp",EDGE,"E7.trimOffspring");var subQ2=makeQuery(id+"F0.imprint","INTERSECT",VERTEX,{"derivedFrom":[subQ1,subQ0]});Q58=makeQuery(id+"F0.imprint","IMPRINT",FACE,{"disambiguationData":[TD([[makeQuery(id+"F0.imprint","IMPRINT",EDGE,{"disambiguationData":[TD([[subQ2,-1.0]])],"derivedFrom":subQ1}),1.0]])]});}
            var Q59;
            {var subQ0=sQuery(id+"F0.wireOp",EDGE,"E21.4.0.0");var subQ1=sQuery(id+"F0.wireOp",EDGE,"E14.trimOffspring");var subQ2=makeQuery(id+"F0.imprint","INTERSECT",VERTEX,{"derivedFrom":[subQ1,subQ0]});Q59=makeQuery(id+"F0.imprint","IMPRINT",FACE,{"disambiguationData":[TD([[makeQuery(id+"F0.imprint","IMPRINT",EDGE,{"disambiguationData":[TD([[subQ2,-1.0]])],"derivedFrom":subQ1}),1.0]])]});}
            var Q60;
            {var subQ0=sQuery(id+"F0.wireOp",EDGE,"E21.1.0.0");var subQ1=sQuery(id+"F0.wireOp",EDGE,"E9.trimOffspring");var subQ2=makeQuery(id+"F0.imprint","INTERSECT",VERTEX,{"derivedFrom":[subQ1,subQ0]});Q60=makeQuery(id+"F0.imprint","IMPRINT",FACE,{"disambiguationData":[TD([[makeQuery(id+"F0.imprint","IMPRINT",EDGE,{"disambiguationData":[TD([[subQ2,-1.0]])],"derivedFrom":subQ1}),1.0]])]});}
            var Q61;
            {var subQ0=sQuery(id+"F0.wireOp",EDGE,"E22.1.0.0");var subQ1=sQuery(id+"F0.wireOp",EDGE,"E16.trimOffspring");var subQ2=makeQuery(id+"F0.imprint","INTERSECT",VERTEX,{"derivedFrom":[subQ1,subQ0]});Q61=makeQuery(id+"F0.imprint","IMPRINT",FACE,{"disambiguationData":[TD([[makeQuery(id+"F0.imprint","IMPRINT",EDGE,{"disambiguationData":[TD([[subQ2,-1.0]])],"derivedFrom":subQ1}),1.0]])]});}
            var Q62;
            {var subQ0=sQuery(id+"F0.wireOp",EDGE,"E22.1.0.0");var subQ1=sQuery(id+"F0.wireOp",EDGE,"E1");var subQ2=makeQuery(id+"F0.imprint","INTERSECT",VERTEX,{"derivedFrom":[subQ1,subQ0]});Q62=makeQuery(id+"F0.imprint","IMPRINT",FACE,{"disambiguationData":[TD([[makeQuery(id+"F0.imprint","IMPRINT",EDGE,{"disambiguationData":[TD([[subQ2,-1.0]])],"derivedFrom":subQ1}),-1.0]])]});}
            var Q63;
            {var subQ0=sQuery(id+"F0.wireOp",EDGE,"E21.3.0.0");var subQ1=sQuery(id+"F0.wireOp",EDGE,"E1");var subQ2=makeQuery(id+"F0.imprint","INTERSECT",VERTEX,{"derivedFrom":[subQ1,subQ0]});Q63=makeQuery(id+"F0.imprint","IMPRINT",FACE,{"disambiguationData":[TD([[makeQuery(id+"F0.imprint","IMPRINT",EDGE,{"disambiguationData":[TD([[subQ2,-1.0]])],"derivedFrom":subQ1}),-1.0]])]});}
            var Q64;
            {var subQ0=sQuery(id+"F0.wireOp",EDGE,"E22.5.0.0");var subQ1=sQuery(id+"F0.wireOp",EDGE,"E12.trimOffspring");var subQ2=makeQuery(id+"F0.imprint","INTERSECT",VERTEX,{"derivedFrom":[subQ1,subQ0]});Q64=makeQuery(id+"F0.imprint","IMPRINT",FACE,{"disambiguationData":[TD([[makeQuery(id+"F0.imprint","IMPRINT",EDGE,{"disambiguationData":[TD([[subQ2,-1.0]])],"derivedFrom":subQ1}),1.0]])]});}
            var Q65;
            {var subQ0=sQuery(id+"F0.wireOp",EDGE,"E22.1.0.0");var subQ1=sQuery(id+"F0.wireOp",EDGE,"E4.trimOffspring");var subQ2=makeQuery(id+"F0.imprint","INTERSECT",VERTEX,{"derivedFrom":[subQ1,subQ0]});Q65=makeQuery(id+"F0.imprint","IMPRINT",FACE,{"disambiguationData":[TD([[makeQuery(id+"F0.imprint","IMPRINT",EDGE,{"disambiguationData":[TD([[subQ2,-1.0]])],"derivedFrom":subQ1}),1.0]])]});}
            var Q66;
            {var subQ0=sQuery(id+"F0.wireOp",EDGE,"E22.4.0.0");var subQ1=sQuery(id+"F0.wireOp",EDGE,"E12.trimOffspring");var subQ2=makeQuery(id+"F0.imprint","INTERSECT",VERTEX,{"derivedFrom":[subQ1,subQ0]});Q66=makeQuery(id+"F0.imprint","IMPRINT",FACE,{"disambiguationData":[TD([[makeQuery(id+"F0.imprint","IMPRINT",EDGE,{"disambiguationData":[TD([[subQ2,-1.0]])],"derivedFrom":subQ1}),1.0]])]});}
            var Q67;
            {var subQ0=sQuery(id+"F0.wireOp",EDGE,"E22.5.0.0");var subQ1=sQuery(id+"F0.wireOp",EDGE,"E15.trimOffspring");var subQ2=makeQuery(id+"F0.imprint","INTERSECT",VERTEX,{"derivedFrom":[subQ1,subQ0]});Q67=makeQuery(id+"F0.imprint","IMPRINT",FACE,{"disambiguationData":[TD([[makeQuery(id+"F0.imprint","IMPRINT",EDGE,{"disambiguationData":[TD([[subQ2,-1.0]])],"derivedFrom":subQ1}),1.0]])]});}
            var Q68;
            {var subQ0=sQuery(id+"F0.wireOp",EDGE,"E21.3.0.0");var subQ1=sQuery(id+"F0.wireOp",EDGE,"E15.trimOffspring");var subQ2=makeQuery(id+"F0.imprint","INTERSECT",VERTEX,{"derivedFrom":[subQ1,subQ0]});Q68=makeQuery(id+"F0.imprint","IMPRINT",FACE,{"disambiguationData":[TD([[makeQuery(id+"F0.imprint","IMPRINT",EDGE,{"disambiguationData":[TD([[subQ2,-1.0]])],"derivedFrom":subQ1}),1.0]])]});}
            var Q69;
            {var subQ0=sQuery(id+"F0.wireOp",EDGE,"E22.2.0.0");var subQ1=sQuery(id+"F0.wireOp",EDGE,"E4.trimOffspring");var subQ2=makeQuery(id+"F0.imprint","INTERSECT",VERTEX,{"derivedFrom":[subQ1,subQ0]});Q69=makeQuery(id+"F0.imprint","IMPRINT",FACE,{"disambiguationData":[TD([[makeQuery(id+"F0.imprint","IMPRINT",EDGE,{"disambiguationData":[TD([[subQ2,-1.0]])],"derivedFrom":subQ1}),1.0]])]});}
            var Q70;
            {var subQ0=sQuery(id+"F0.wireOp",EDGE,"E22.4.0.0");var subQ1=sQuery(id+"F0.wireOp",EDGE,"E10.trimOffspring");var subQ2=makeQuery(id+"F0.imprint","INTERSECT",VERTEX,{"derivedFrom":[subQ1,subQ0]});Q70=makeQuery(id+"F0.imprint","IMPRINT",FACE,{"disambiguationData":[TD([[makeQuery(id+"F0.imprint","IMPRINT",EDGE,{"disambiguationData":[TD([[subQ2,-1.0]])],"derivedFrom":subQ1}),1.0]])]});}
            var Q71;
            {var subQ0=sQuery(id+"F0.wireOp",EDGE,"E22.1.0.0");var subQ1=sQuery(id+"F0.wireOp",EDGE,"E7.trimOffspring");var subQ2=makeQuery(id+"F0.imprint","INTERSECT",VERTEX,{"derivedFrom":[subQ1,subQ0]});Q71=makeQuery(id+"F0.imprint","IMPRINT",FACE,{"disambiguationData":[TD([[makeQuery(id+"F0.imprint","IMPRINT",EDGE,{"disambiguationData":[TD([[subQ2,-1.0]])],"derivedFrom":subQ1}),1.0]])]});}
            var Q72;
            {var subQ0=sQuery(id+"F0.wireOp",EDGE,"E21.4.0.0");var subQ1=sQuery(id+"F0.wireOp",EDGE,"E7.trimOffspring");var subQ2=makeQuery(id+"F0.imprint","INTERSECT",VERTEX,{"derivedFrom":[subQ1,subQ0]});Q72=makeQuery(id+"F0.imprint","IMPRINT",FACE,{"disambiguationData":[TD([[makeQuery(id+"F0.imprint","IMPRINT",EDGE,{"disambiguationData":[TD([[subQ2,-1.0]])],"derivedFrom":subQ1}),1.0]])]});}
            var Q73;
            {var subQ0=sQuery(id+"F0.wireOp",EDGE,"E22.3.0.0");var subQ1=sQuery(id+"F0.wireOp",EDGE,"E7.trimOffspring");var subQ2=makeQuery(id+"F0.imprint","INTERSECT",VERTEX,{"derivedFrom":[subQ1,subQ0]});Q73=makeQuery(id+"F0.imprint","IMPRINT",FACE,{"disambiguationData":[TD([[makeQuery(id+"F0.imprint","IMPRINT",EDGE,{"disambiguationData":[TD([[subQ2,-1.0]])],"derivedFrom":subQ1}),1.0]])]});}
            var Q74;
            {var subQ0=sQuery(id+"F0.wireOp",EDGE,"E22.1.0.0");var subQ1=sQuery(id+"F0.wireOp",EDGE,"E1");var subQ2=makeQuery(id+"F0.imprint","INTERSECT",VERTEX,{"derivedFrom":[subQ1,subQ0]});Q74=makeQuery(id+"F0.imprint","IMPRINT",FACE,{"disambiguationData":[TD([[makeQuery(id+"F0.imprint","IMPRINT",EDGE,{"disambiguationData":[TD([[subQ2,-1.0]])],"derivedFrom":subQ1}),1.0]])]});}
            var Q75;
            {var subQ0=sQuery(id+"F0.wireOp",EDGE,"E22.5.0.0");var subQ1=sQuery(id+"F0.wireOp",EDGE,"E4.trimOffspring");var subQ2=makeQuery(id+"F0.imprint","INTERSECT",VERTEX,{"derivedFrom":[subQ1,subQ0]});Q75=makeQuery(id+"F0.imprint","IMPRINT",FACE,{"disambiguationData":[TD([[makeQuery(id+"F0.imprint","IMPRINT",EDGE,{"disambiguationData":[TD([[subQ2,-1.0]])],"derivedFrom":subQ1}),1.0]])]});}
            var Q76;
            {var subQ0=sQuery(id+"F0.wireOp",EDGE,"E21.5.0.0");var subQ1=sQuery(id+"F0.wireOp",EDGE,"E16.trimOffspring");var subQ2=makeQuery(id+"F0.imprint","INTERSECT",VERTEX,{"derivedFrom":[subQ1,subQ0]});Q76=makeQuery(id+"F0.imprint","IMPRINT",FACE,{"disambiguationData":[TD([[makeQuery(id+"F0.imprint","IMPRINT",EDGE,{"disambiguationData":[TD([[subQ2,-1.0]])],"derivedFrom":subQ1}),1.0]])]});}
            var Q77;
            {var subQ0=sQuery(id+"F0.wireOp",EDGE,"E22.1.0.0");var subQ1=sQuery(id+"F0.wireOp",EDGE,"E14.trimOffspring");var subQ2=makeQuery(id+"F0.imprint","INTERSECT",VERTEX,{"derivedFrom":[subQ1,subQ0]});Q77=makeQuery(id+"F0.imprint","IMPRINT",FACE,{"disambiguationData":[TD([[makeQuery(id+"F0.imprint","IMPRINT",EDGE,{"disambiguationData":[TD([[subQ2,-1.0]])],"derivedFrom":subQ1}),1.0]])]});}
            var Q78;
            {var subQ0=sQuery(id+"F0.wireOp",EDGE,"E22.3.0.0");var subQ1=sQuery(id+"F0.wireOp",EDGE,"E1");var subQ2=makeQuery(id+"F0.imprint","INTERSECT",VERTEX,{"derivedFrom":[subQ1,subQ0]});Q78=makeQuery(id+"F0.imprint","IMPRINT",FACE,{"disambiguationData":[TD([[makeQuery(id+"F0.imprint","IMPRINT",EDGE,{"disambiguationData":[TD([[subQ2,-1.0]])],"derivedFrom":subQ1}),-1.0]])]});}
            var Q79;
            {var subQ0=sQuery(id+"F0.wireOp",EDGE,"E22.5.0.0");var subQ1=sQuery(id+"F0.wireOp",EDGE,"E14.trimOffspring");var subQ2=makeQuery(id+"F0.imprint","INTERSECT",VERTEX,{"derivedFrom":[subQ1,subQ0]});Q79=makeQuery(id+"F0.imprint","IMPRINT",FACE,{"disambiguationData":[TD([[makeQuery(id+"F0.imprint","IMPRINT",EDGE,{"disambiguationData":[TD([[subQ2,-1.0]])],"derivedFrom":subQ1}),1.0]])]});}
            var Q80;
            {var subQ0=sQuery(id+"F0.wireOp",EDGE,"E22.2.0.0");var subQ1=sQuery(id+"F0.wireOp",EDGE,"E8.trimOffspring");var subQ2=makeQuery(id+"F0.imprint","INTERSECT",VERTEX,{"derivedFrom":[subQ1,subQ0]});Q80=makeQuery(id+"F0.imprint","IMPRINT",FACE,{"disambiguationData":[TD([[makeQuery(id+"F0.imprint","IMPRINT",EDGE,{"disambiguationData":[TD([[subQ2,-1.0]])],"derivedFrom":subQ1}),1.0]])]});}
            var Q81;
            {var subQ0=sQuery(id+"F0.wireOp",EDGE,"E21.1.0.0");var subQ1=sQuery(id+"F0.wireOp",EDGE,"E8.trimOffspring");var subQ2=makeQuery(id+"F0.imprint","INTERSECT",VERTEX,{"derivedFrom":[subQ1,subQ0]});Q81=makeQuery(id+"F0.imprint","IMPRINT",FACE,{"disambiguationData":[TD([[makeQuery(id+"F0.imprint","IMPRINT",EDGE,{"disambiguationData":[TD([[subQ2,-1.0]])],"derivedFrom":subQ1}),1.0]])]});}
            var Q82;
            {var subQ0=sQuery(id+"F0.wireOp",EDGE,"E21.5.0.0");var subQ1=sQuery(id+"F0.wireOp",EDGE,"E6.trimOffspring");var subQ2=makeQuery(id+"F0.imprint","INTERSECT",VERTEX,{"derivedFrom":[subQ1,subQ0]});Q82=makeQuery(id+"F0.imprint","IMPRINT",FACE,{"disambiguationData":[TD([[makeQuery(id+"F0.imprint","IMPRINT",EDGE,{"disambiguationData":[TD([[subQ2,-1.0]])],"derivedFrom":subQ1}),1.0]])]});}
            var Q83;
            {var subQ0=sQuery(id+"F0.wireOp",EDGE,"E22.3.0.0");var subQ1=sQuery(id+"F0.wireOp",EDGE,"E5.trimOffspring");var subQ2=makeQuery(id+"F0.imprint","INTERSECT",VERTEX,{"derivedFrom":[subQ1,subQ0]});Q83=makeQuery(id+"F0.imprint","IMPRINT",FACE,{"disambiguationData":[TD([[makeQuery(id+"F0.imprint","IMPRINT",EDGE,{"disambiguationData":[TD([[subQ2,-1.0]])],"derivedFrom":subQ1}),1.0]])]});}
            var Q84;
            {var subQ0=sQuery(id+"F0.wireOp",EDGE,"E22.5.0.0");var subQ1=sQuery(id+"F0.wireOp",EDGE,"E10.trimOffspring");var subQ2=makeQuery(id+"F0.imprint","INTERSECT",VERTEX,{"derivedFrom":[subQ1,subQ0]});Q84=makeQuery(id+"F0.imprint","IMPRINT",FACE,{"disambiguationData":[TD([[makeQuery(id+"F0.imprint","IMPRINT",EDGE,{"disambiguationData":[TD([[subQ2,-1.0]])],"derivedFrom":subQ1}),1.0]])]});}
            var Q85;
            {var subQ0=sQuery(id+"F0.wireOp",EDGE,"E22.2.0.0");var subQ1=sQuery(id+"F0.wireOp",EDGE,"E1");var subQ2=makeQuery(id+"F0.imprint","INTERSECT",VERTEX,{"derivedFrom":[subQ1,subQ0]});Q85=makeQuery(id+"F0.imprint","IMPRINT",FACE,{"disambiguationData":[TD([[makeQuery(id+"F0.imprint","IMPRINT",EDGE,{"disambiguationData":[TD([[subQ2,-1.0]])],"derivedFrom":subQ1}),-1.0]])]});}
            var Q86;
            {var subQ0=sQuery(id+"F0.wireOp",EDGE,"E21.2.0.0");var subQ1=sQuery(id+"F0.wireOp",EDGE,"E9.trimOffspring");var subQ2=makeQuery(id+"F0.imprint","INTERSECT",VERTEX,{"derivedFrom":[subQ1,subQ0]});Q86=makeQuery(id+"F0.imprint","IMPRINT",FACE,{"disambiguationData":[TD([[makeQuery(id+"F0.imprint","IMPRINT",EDGE,{"disambiguationData":[TD([[subQ2,-1.0]])],"derivedFrom":subQ1}),1.0]])]});}
            var Q87;
            {var subQ0=sQuery(id+"F0.wireOp",EDGE,"E22.4.0.0");var subQ1=sQuery(id+"F0.wireOp",EDGE,"E5.trimOffspring");var subQ2=makeQuery(id+"F0.imprint","INTERSECT",VERTEX,{"derivedFrom":[subQ1,subQ0]});Q87=makeQuery(id+"F0.imprint","IMPRINT",FACE,{"disambiguationData":[TD([[makeQuery(id+"F0.imprint","IMPRINT",EDGE,{"disambiguationData":[TD([[subQ2,-1.0]])],"derivedFrom":subQ1}),1.0]])]});}
            var Q88;
            {var subQ0=sQuery(id+"F0.wireOp",EDGE,"E21.4.0.0");var subQ1=sQuery(id+"F0.wireOp",EDGE,"E6.trimOffspring");var subQ2=makeQuery(id+"F0.imprint","INTERSECT",VERTEX,{"derivedFrom":[subQ1,subQ0]});Q88=makeQuery(id+"F0.imprint","IMPRINT",FACE,{"disambiguationData":[TD([[makeQuery(id+"F0.imprint","IMPRINT",EDGE,{"disambiguationData":[TD([[subQ2,-1.0]])],"derivedFrom":subQ1}),1.0]])]});}
            var Q89;
            {var subQ0=sQuery(id+"F0.wireOp",EDGE,"E21.2.0.0");var subQ1=sQuery(id+"F0.wireOp",EDGE,"E4.trimOffspring");var subQ2=makeQuery(id+"F0.imprint","INTERSECT",VERTEX,{"derivedFrom":[subQ1,subQ0]});Q89=makeQuery(id+"F0.imprint","IMPRINT",FACE,{"disambiguationData":[TD([[makeQuery(id+"F0.imprint","IMPRINT",EDGE,{"disambiguationData":[TD([[subQ2,-1.0]])],"derivedFrom":subQ1}),1.0]])]});}
            var Q90;
            {var subQ0=sQuery(id+"F0.wireOp",EDGE,"E22.4.0.0");var subQ1=sQuery(id+"F0.wireOp",EDGE,"E8.trimOffspring");var subQ2=makeQuery(id+"F0.imprint","INTERSECT",VERTEX,{"derivedFrom":[subQ1,subQ0]});Q90=makeQuery(id+"F0.imprint","IMPRINT",FACE,{"disambiguationData":[TD([[makeQuery(id+"F0.imprint","IMPRINT",EDGE,{"disambiguationData":[TD([[subQ2,-1.0]])],"derivedFrom":subQ1}),1.0]])]});}
            var Q91;
            {var subQ0=sQuery(id+"F0.wireOp",EDGE,"E21.3.0.0");var subQ1=sQuery(id+"F0.wireOp",EDGE,"E8.trimOffspring");var subQ2=makeQuery(id+"F0.imprint","INTERSECT",VERTEX,{"derivedFrom":[subQ1,subQ0]});Q91=makeQuery(id+"F0.imprint","IMPRINT",FACE,{"disambiguationData":[TD([[makeQuery(id+"F0.imprint","IMPRINT",EDGE,{"disambiguationData":[TD([[subQ2,-1.0]])],"derivedFrom":subQ1}),1.0]])]});}
            var Q92;
            {var subQ0=sQuery(id+"F0.wireOp",EDGE,"E22.3.0.0");var subQ1=sQuery(id+"F0.wireOp",EDGE,"E4.trimOffspring");var subQ2=makeQuery(id+"F0.imprint","INTERSECT",VERTEX,{"derivedFrom":[subQ1,subQ0]});Q92=makeQuery(id+"F0.imprint","IMPRINT",FACE,{"disambiguationData":[TD([[makeQuery(id+"F0.imprint","IMPRINT",EDGE,{"disambiguationData":[TD([[subQ2,-1.0]])],"derivedFrom":subQ1}),1.0]])]});}
            var Q93;
            {var subQ0=sQuery(id+"F0.wireOp",EDGE,"E22.4.0.0");var subQ1=sQuery(id+"F0.wireOp",EDGE,"E6.trimOffspring");var subQ2=makeQuery(id+"F0.imprint","INTERSECT",VERTEX,{"derivedFrom":[subQ1,subQ0]});Q93=makeQuery(id+"F0.imprint","IMPRINT",FACE,{"disambiguationData":[TD([[makeQuery(id+"F0.imprint","IMPRINT",EDGE,{"disambiguationData":[TD([[subQ2,-1.0]])],"derivedFrom":subQ1}),1.0]])]});}
            var Q94;
            {var subQ0=sQuery(id+"F0.wireOp",EDGE,"E20");var subQ1=sQuery(id+"F0.wireOp",EDGE,"E1");var subQ2=makeQuery(id+"F0.imprint","INTERSECT",VERTEX,{"derivedFrom":[subQ1,subQ0]});Q94=makeQuery(id+"F0.imprint","IMPRINT",FACE,{"disambiguationData":[TD([[makeQuery(id+"F0.imprint","IMPRINT",EDGE,{"disambiguationData":[TD([[subQ2,-1.0]])],"derivedFrom":subQ1}),1.0]])]});}
            var Q95;
            {var subQ0=sQuery(id+"F0.wireOp",EDGE,"E22.5.0.0");var subQ1=sQuery(id+"F0.wireOp",EDGE,"E8.trimOffspring");var subQ2=makeQuery(id+"F0.imprint","INTERSECT",VERTEX,{"derivedFrom":[subQ1,subQ0]});Q95=makeQuery(id+"F0.imprint","IMPRINT",FACE,{"disambiguationData":[TD([[makeQuery(id+"F0.imprint","IMPRINT",EDGE,{"disambiguationData":[TD([[subQ2,-1.0]])],"derivedFrom":subQ1}),1.0]])]});}
            var Q96;
            {var subQ0=sQuery(id+"F0.wireOp",EDGE,"E22.1.0.0");var subQ1=sQuery(id+"F0.wireOp",EDGE,"E17.trimOffspring");var subQ2=makeQuery(id+"F0.imprint","INTERSECT",VERTEX,{"derivedFrom":[subQ1,subQ0]});Q96=makeQuery(id+"F0.imprint","IMPRINT",FACE,{"disambiguationData":[TD([[makeQuery(id+"F0.imprint","IMPRINT",EDGE,{"disambiguationData":[TD([[subQ2,-1.0]])],"derivedFrom":subQ1}),1.0]])]});}
            var Q97;
            {var subQ0=sQuery(id+"F0.wireOp",EDGE,"E22.4.0.0");var subQ1=sQuery(id+"F0.wireOp",EDGE,"E1");var subQ2=makeQuery(id+"F0.imprint","INTERSECT",VERTEX,{"derivedFrom":[subQ1,subQ0]});Q97=makeQuery(id+"F0.imprint","IMPRINT",FACE,{"disambiguationData":[TD([[makeQuery(id+"F0.imprint","IMPRINT",EDGE,{"disambiguationData":[TD([[subQ2,-1.0]])],"derivedFrom":subQ1}),1.0]])]});}
            var Q98;
            {var subQ0=sQuery(id+"F0.wireOp",EDGE,"E20");var subQ1=sQuery(id+"F0.wireOp",EDGE,"E13.trimOffspring");var subQ2=makeQuery(id+"F0.imprint","INTERSECT",VERTEX,{"derivedFrom":[subQ1,subQ0]});Q98=makeQuery(id+"F0.imprint","IMPRINT",FACE,{"disambiguationData":[TD([[makeQuery(id+"F0.imprint","IMPRINT",EDGE,{"disambiguationData":[TD([[subQ2,-1.0]])],"derivedFrom":subQ1}),1.0]])]});}
            var Q99;
            {var subQ0=sQuery(id+"F0.wireOp",EDGE,"E21.2.0.0");var subQ1=sQuery(id+"F0.wireOp",EDGE,"E1");var subQ2=makeQuery(id+"F0.imprint","INTERSECT",VERTEX,{"derivedFrom":[subQ1,subQ0]});Q99=makeQuery(id+"F0.imprint","IMPRINT",FACE,{"disambiguationData":[TD([[makeQuery(id+"F0.imprint","IMPRINT",EDGE,{"disambiguationData":[TD([[subQ2,-1.0]])],"derivedFrom":subQ1}),1.0]])]});}
            var Q100;
            {var subQ0=sQuery(id+"F0.wireOp",EDGE,"E21.2.0.0");var subQ1=sQuery(id+"F0.wireOp",EDGE,"E6.trimOffspring");var subQ2=makeQuery(id+"F0.imprint","INTERSECT",VERTEX,{"derivedFrom":[subQ1,subQ0]});Q100=makeQuery(id+"F0.imprint","IMPRINT",FACE,{"disambiguationData":[TD([[makeQuery(id+"F0.imprint","IMPRINT",EDGE,{"disambiguationData":[TD([[subQ2,-1.0]])],"derivedFrom":subQ1}),1.0]])]});}
            var Q101;
            {var subQ0=sQuery(id+"F0.wireOp",EDGE,"E21.4.0.0");var subQ1=sQuery(id+"F0.wireOp",EDGE,"E2.0.9.0");var subQ2=makeQuery(id+"F0.imprint","INTERSECT",VERTEX,{"derivedFrom":[subQ1,subQ0]});Q101=makeQuery(id+"F0.imprint","IMPRINT",FACE,{"disambiguationData":[TD([[makeQuery(id+"F0.imprint","IMPRINT",EDGE,{"disambiguationData":[TD([[subQ2,-1.0]])],"derivedFrom":subQ1}),-1.0]])]});}
            var Q102;
            {var subQ0=sQuery(id+"F0.wireOp",EDGE,"E22.5.0.0");var subQ1=sQuery(id+"F0.wireOp",EDGE,"E17.trimOffspring");var subQ2=makeQuery(id+"F0.imprint","INTERSECT",VERTEX,{"derivedFrom":[subQ1,subQ0]});Q102=makeQuery(id+"F0.imprint","IMPRINT",FACE,{"disambiguationData":[TD([[makeQuery(id+"F0.imprint","IMPRINT",EDGE,{"disambiguationData":[TD([[subQ2,-1.0]])],"derivedFrom":subQ1}),1.0]])]});}
            var Q103;
            {var subQ0=sQuery(id+"F0.wireOp",EDGE,"E20");var subQ1=sQuery(id+"F0.wireOp",EDGE,"E1");var subQ2=makeQuery(id+"F0.imprint","INTERSECT",VERTEX,{"derivedFrom":[subQ1,subQ0]});Q103=makeQuery(id+"F0.imprint","IMPRINT",FACE,{"disambiguationData":[TD([[makeQuery(id+"F0.imprint","IMPRINT",EDGE,{"disambiguationData":[TD([[subQ2,-1.0]])],"derivedFrom":subQ1}),-1.0]])]});}
            var Q104;
            {var subQ0=sQuery(id+"F0.wireOp",EDGE,"E22.2.0.0");var subQ1=sQuery(id+"F0.wireOp",EDGE,"E1");var subQ2=makeQuery(id+"F0.imprint","INTERSECT",VERTEX,{"derivedFrom":[subQ1,subQ0]});Q104=makeQuery(id+"F0.imprint","IMPRINT",FACE,{"disambiguationData":[TD([[makeQuery(id+"F0.imprint","IMPRINT",EDGE,{"disambiguationData":[TD([[subQ2,-1.0]])],"derivedFrom":subQ1}),1.0]])]});}
            var Q105;
            {var subQ0=sQuery(id+"F0.wireOp",EDGE,"E22.1.0.0");var subQ1=sQuery(id+"F0.wireOp",EDGE,"E13.trimOffspring");var subQ2=makeQuery(id+"F0.imprint","INTERSECT",VERTEX,{"derivedFrom":[subQ1,subQ0]});Q105=makeQuery(id+"F0.imprint","IMPRINT",FACE,{"disambiguationData":[TD([[makeQuery(id+"F0.imprint","IMPRINT",EDGE,{"disambiguationData":[TD([[subQ2,-1.0]])],"derivedFrom":subQ1}),1.0]])]});}
            var Q106;
            {var subQ0=sQuery(id+"F0.wireOp",EDGE,"E22.1.0.0");var subQ1=sQuery(id+"F0.wireOp",EDGE,"E5.trimOffspring");var subQ2=makeQuery(id+"F0.imprint","INTERSECT",VERTEX,{"derivedFrom":[subQ1,subQ0]});Q106=makeQuery(id+"F0.imprint","IMPRINT",FACE,{"disambiguationData":[TD([[makeQuery(id+"F0.imprint","IMPRINT",EDGE,{"disambiguationData":[TD([[subQ2,-1.0]])],"derivedFrom":subQ1}),1.0]])]});}
            var Q107;
            {var subQ0=sQuery(id+"F0.wireOp",EDGE,"E21.5.0.0");var subQ1=sQuery(id+"F0.wireOp",EDGE,"E4.trimOffspring");var subQ2=makeQuery(id+"F0.imprint","INTERSECT",VERTEX,{"derivedFrom":[subQ1,subQ0]});Q107=makeQuery(id+"F0.imprint","IMPRINT",FACE,{"disambiguationData":[TD([[makeQuery(id+"F0.imprint","IMPRINT",EDGE,{"disambiguationData":[TD([[subQ2,-1.0]])],"derivedFrom":subQ1}),1.0]])]});}
            var Q108;
            {var subQ0=sQuery(id+"F0.wireOp",EDGE,"E22.4.0.0");var subQ1=sQuery(id+"F0.wireOp",EDGE,"E17.trimOffspring");var subQ2=makeQuery(id+"F0.imprint","INTERSECT",VERTEX,{"derivedFrom":[subQ1,subQ0]});Q108=makeQuery(id+"F0.imprint","IMPRINT",FACE,{"disambiguationData":[TD([[makeQuery(id+"F0.imprint","IMPRINT",EDGE,{"disambiguationData":[TD([[subQ2,-1.0]])],"derivedFrom":subQ1}),1.0]])]});}
            var Q109;
            {var subQ0=sQuery(id+"F0.wireOp",EDGE,"E22.3.0.0");var subQ1=sQuery(id+"F0.wireOp",EDGE,"E8.trimOffspring");var subQ2=makeQuery(id+"F0.imprint","INTERSECT",VERTEX,{"derivedFrom":[subQ1,subQ0]});Q109=makeQuery(id+"F0.imprint","IMPRINT",FACE,{"disambiguationData":[TD([[makeQuery(id+"F0.imprint","IMPRINT",EDGE,{"disambiguationData":[TD([[subQ2,-1.0]])],"derivedFrom":subQ1}),1.0]])]});}
            var Q110;
            {var subQ0=sQuery(id+"F0.wireOp",EDGE,"E21.1.0.0");var subQ1=sQuery(id+"F0.wireOp",EDGE,"E17.trimOffspring");var subQ2=makeQuery(id+"F0.imprint","INTERSECT",VERTEX,{"derivedFrom":[subQ1,subQ0]});Q110=makeQuery(id+"F0.imprint","IMPRINT",FACE,{"disambiguationData":[TD([[makeQuery(id+"F0.imprint","IMPRINT",EDGE,{"disambiguationData":[TD([[subQ2,-1.0]])],"derivedFrom":subQ1}),1.0]])]});}
            var Q111;
            {var subQ0=sQuery(id+"F0.wireOp",EDGE,"E21.4.0.0");var subQ1=sQuery(id+"F0.wireOp",EDGE,"E5.trimOffspring");var subQ2=makeQuery(id+"F0.imprint","INTERSECT",VERTEX,{"derivedFrom":[subQ1,subQ0]});Q111=makeQuery(id+"F0.imprint","IMPRINT",FACE,{"disambiguationData":[TD([[makeQuery(id+"F0.imprint","IMPRINT",EDGE,{"disambiguationData":[TD([[subQ2,-1.0]])],"derivedFrom":subQ1}),1.0]])]});}
            var Q112;
            {var subQ0=sQuery(id+"F0.wireOp",EDGE,"E20");var subQ1=sQuery(id+"F0.wireOp",EDGE,"E17.trimOffspring");var subQ2=makeQuery(id+"F0.imprint","INTERSECT",VERTEX,{"derivedFrom":[subQ1,subQ0]});Q112=makeQuery(id+"F0.imprint","IMPRINT",FACE,{"disambiguationData":[TD([[makeQuery(id+"F0.imprint","IMPRINT",EDGE,{"disambiguationData":[TD([[subQ2,-1.0]])],"derivedFrom":subQ1}),1.0]])]});}
            var Q113;
            {var subQ0=sQuery(id+"F0.wireOp",EDGE,"E22.2.0.0");var subQ1=sQuery(id+"F0.wireOp",EDGE,"E12.trimOffspring");var subQ2=makeQuery(id+"F0.imprint","INTERSECT",VERTEX,{"derivedFrom":[subQ1,subQ0]});Q113=makeQuery(id+"F0.imprint","IMPRINT",FACE,{"disambiguationData":[TD([[makeQuery(id+"F0.imprint","IMPRINT",EDGE,{"disambiguationData":[TD([[subQ2,-1.0]])],"derivedFrom":subQ1}),1.0]])]});}
            var Q114;
            {var subQ0=sQuery(id+"F0.wireOp",EDGE,"E21.3.0.0");var subQ1=sQuery(id+"F0.wireOp",EDGE,"E9.trimOffspring");var subQ2=makeQuery(id+"F0.imprint","INTERSECT",VERTEX,{"derivedFrom":[subQ1,subQ0]});Q114=makeQuery(id+"F0.imprint","IMPRINT",FACE,{"disambiguationData":[TD([[makeQuery(id+"F0.imprint","IMPRINT",EDGE,{"disambiguationData":[TD([[subQ2,-1.0]])],"derivedFrom":subQ1}),1.0]])]});}
            var Q115;
            {var subQ0=sQuery(id+"F0.wireOp",EDGE,"E21.5.0.0");var subQ1=sQuery(id+"F0.wireOp",EDGE,"E14.trimOffspring");var subQ2=makeQuery(id+"F0.imprint","INTERSECT",VERTEX,{"derivedFrom":[subQ1,subQ0]});Q115=makeQuery(id+"F0.imprint","IMPRINT",FACE,{"disambiguationData":[TD([[makeQuery(id+"F0.imprint","IMPRINT",EDGE,{"disambiguationData":[TD([[subQ2,-1.0]])],"derivedFrom":subQ1}),1.0]])]});}
            var Q116;
            {var subQ0=sQuery(id+"F0.wireOp",EDGE,"E22.5.0.0");var subQ1=sQuery(id+"F0.wireOp",EDGE,"E5.trimOffspring");var subQ2=makeQuery(id+"F0.imprint","INTERSECT",VERTEX,{"derivedFrom":[subQ1,subQ0]});Q116=makeQuery(id+"F0.imprint","IMPRINT",FACE,{"disambiguationData":[TD([[makeQuery(id+"F0.imprint","IMPRINT",EDGE,{"disambiguationData":[TD([[subQ2,-1.0]])],"derivedFrom":subQ1}),1.0]])]});}
            var Q117;
            {var subQ0=sQuery(id+"F0.wireOp",EDGE,"E22.3.0.0");var subQ1=sQuery(id+"F0.wireOp",EDGE,"E17.trimOffspring");var subQ2=makeQuery(id+"F0.imprint","INTERSECT",VERTEX,{"derivedFrom":[subQ1,subQ0]});Q117=makeQuery(id+"F0.imprint","IMPRINT",FACE,{"disambiguationData":[TD([[makeQuery(id+"F0.imprint","IMPRINT",EDGE,{"disambiguationData":[TD([[subQ2,-1.0]])],"derivedFrom":subQ1}),1.0]])]});}
            var Q118;
            {var subQ0=sQuery(id+"F0.wireOp",EDGE,"E21.1.0.0");var subQ1=sQuery(id+"F0.wireOp",EDGE,"E6.trimOffspring");var subQ2=makeQuery(id+"F0.imprint","INTERSECT",VERTEX,{"derivedFrom":[subQ1,subQ0]});Q118=makeQuery(id+"F0.imprint","IMPRINT",FACE,{"disambiguationData":[TD([[makeQuery(id+"F0.imprint","IMPRINT",EDGE,{"disambiguationData":[TD([[subQ2,-1.0]])],"derivedFrom":subQ1}),1.0]])]});}
            var Q119;
            {var subQ0=sQuery(id+"F0.wireOp",EDGE,"E22.2.0.0");var subQ1=sQuery(id+"F0.wireOp",EDGE,"E17.trimOffspring");var subQ2=makeQuery(id+"F0.imprint","INTERSECT",VERTEX,{"derivedFrom":[subQ1,subQ0]});Q119=makeQuery(id+"F0.imprint","IMPRINT",FACE,{"disambiguationData":[TD([[makeQuery(id+"F0.imprint","IMPRINT",EDGE,{"disambiguationData":[TD([[subQ2,-1.0]])],"derivedFrom":subQ1}),1.0]])]});}
            var Q120;
            {var subQ0=sQuery(id+"F0.wireOp",EDGE,"E21.1.0.0");var subQ1=sQuery(id+"F0.wireOp",EDGE,"E2.0.9.0");var subQ2=makeQuery(id+"F0.imprint","INTERSECT",VERTEX,{"derivedFrom":[subQ1,subQ0]});Q120=makeQuery(id+"F0.imprint","IMPRINT",FACE,{"disambiguationData":[TD([[makeQuery(id+"F0.imprint","IMPRINT",EDGE,{"disambiguationData":[TD([[subQ2,-1.0]])],"derivedFrom":subQ1}),-1.0]])]});}
            var Q121;
            {var subQ0=sQuery(id+"F0.wireOp",EDGE,"E22.2.0.0");var subQ1=sQuery(id+"F0.wireOp",EDGE,"E15.trimOffspring");var subQ2=makeQuery(id+"F0.imprint","INTERSECT",VERTEX,{"derivedFrom":[subQ1,subQ0]});Q121=makeQuery(id+"F0.imprint","IMPRINT",FACE,{"disambiguationData":[TD([[makeQuery(id+"F0.imprint","IMPRINT",EDGE,{"disambiguationData":[TD([[subQ2,-1.0]])],"derivedFrom":subQ1}),1.0]])]});}
            var Q122;
            {var subQ0=sQuery(id+"F0.wireOp",EDGE,"E22.3.0.0");var subQ1=sQuery(id+"F0.wireOp",EDGE,"E16.trimOffspring");var subQ2=makeQuery(id+"F0.imprint","INTERSECT",VERTEX,{"derivedFrom":[subQ1,subQ0]});Q122=makeQuery(id+"F0.imprint","IMPRINT",FACE,{"disambiguationData":[TD([[makeQuery(id+"F0.imprint","IMPRINT",EDGE,{"disambiguationData":[TD([[subQ2,-1.0]])],"derivedFrom":subQ1}),1.0]])]});}
            var Q123;
            {var subQ0=sQuery(id+"F0.wireOp",EDGE,"E21.5.0.0");var subQ1=sQuery(id+"F0.wireOp",EDGE,"E9.trimOffspring");var subQ2=makeQuery(id+"F0.imprint","INTERSECT",VERTEX,{"derivedFrom":[subQ1,subQ0]});Q123=makeQuery(id+"F0.imprint","IMPRINT",FACE,{"disambiguationData":[TD([[makeQuery(id+"F0.imprint","IMPRINT",EDGE,{"disambiguationData":[TD([[subQ2,-1.0]])],"derivedFrom":subQ1}),1.0]])]});}
            var Q124;
            {var subQ0=sQuery(id+"F0.wireOp",EDGE,"E21.5.0.0");var subQ1=sQuery(id+"F0.wireOp",EDGE,"E5.trimOffspring");var subQ2=makeQuery(id+"F0.imprint","INTERSECT",VERTEX,{"derivedFrom":[subQ1,subQ0]});Q124=makeQuery(id+"F0.imprint","IMPRINT",FACE,{"disambiguationData":[TD([[makeQuery(id+"F0.imprint","IMPRINT",EDGE,{"disambiguationData":[TD([[subQ2,-1.0]])],"derivedFrom":subQ1}),1.0]])]});}
            var Q125;
            {var subQ0=sQuery(id+"F0.wireOp",EDGE,"E22.4.0.0");var subQ1=sQuery(id+"F0.wireOp",EDGE,"E7.trimOffspring");var subQ2=makeQuery(id+"F0.imprint","INTERSECT",VERTEX,{"derivedFrom":[subQ1,subQ0]});Q125=makeQuery(id+"F0.imprint","IMPRINT",FACE,{"disambiguationData":[TD([[makeQuery(id+"F0.imprint","IMPRINT",EDGE,{"disambiguationData":[TD([[subQ2,-1.0]])],"derivedFrom":subQ1}),1.0]])]});}
            var Q126;
            {var subQ0=sQuery(id+"F0.wireOp",EDGE,"E21.1.0.0");var subQ1=sQuery(id+"F0.wireOp",EDGE,"E7.trimOffspring");var subQ2=makeQuery(id+"F0.imprint","INTERSECT",VERTEX,{"derivedFrom":[subQ1,subQ0]});Q126=makeQuery(id+"F0.imprint","IMPRINT",FACE,{"disambiguationData":[TD([[makeQuery(id+"F0.imprint","IMPRINT",EDGE,{"disambiguationData":[TD([[subQ2,-1.0]])],"derivedFrom":subQ1}),1.0]])]});}
            var Q127;
            {var subQ0=sQuery(id+"F0.wireOp",EDGE,"E22.5.0.0");var subQ1=sQuery(id+"F0.wireOp",EDGE,"E13.trimOffspring");var subQ2=makeQuery(id+"F0.imprint","INTERSECT",VERTEX,{"derivedFrom":[subQ1,subQ0]});Q127=makeQuery(id+"F0.imprint","IMPRINT",FACE,{"disambiguationData":[TD([[makeQuery(id+"F0.imprint","IMPRINT",EDGE,{"disambiguationData":[TD([[subQ2,-1.0]])],"derivedFrom":subQ1}),1.0]])]});}
            var Q128;
            {var subQ0=sQuery(id+"F0.wireOp",EDGE,"E21.4.0.0");var subQ1=sQuery(id+"F0.wireOp",EDGE,"E8.trimOffspring");var subQ2=makeQuery(id+"F0.imprint","INTERSECT",VERTEX,{"derivedFrom":[subQ1,subQ0]});Q128=makeQuery(id+"F0.imprint","IMPRINT",FACE,{"disambiguationData":[TD([[makeQuery(id+"F0.imprint","IMPRINT",EDGE,{"disambiguationData":[TD([[subQ2,-1.0]])],"derivedFrom":subQ1}),1.0]])]});}
            var Q129;
            {var subQ0=sQuery(id+"F0.wireOp",EDGE,"E21.3.0.0");var subQ1=sQuery(id+"F0.wireOp",EDGE,"E10.trimOffspring");var subQ2=makeQuery(id+"F0.imprint","INTERSECT",VERTEX,{"derivedFrom":[subQ1,subQ0]});Q129=makeQuery(id+"F0.imprint","IMPRINT",FACE,{"disambiguationData":[TD([[makeQuery(id+"F0.imprint","IMPRINT",EDGE,{"disambiguationData":[TD([[subQ2,-1.0]])],"derivedFrom":subQ1}),1.0]])]});}
            var Q130;
            {var subQ0=sQuery(id+"F0.wireOp",EDGE,"E22.5.0.0");var subQ1=sQuery(id+"F0.wireOp",EDGE,"E2.0.9.0");var subQ2=makeQuery(id+"F0.imprint","INTERSECT",VERTEX,{"derivedFrom":[subQ1,subQ0]});Q130=makeQuery(id+"F0.imprint","IMPRINT",FACE,{"disambiguationData":[TD([[makeQuery(id+"F0.imprint","IMPRINT",EDGE,{"disambiguationData":[TD([[subQ2,-1.0]])],"derivedFrom":subQ1}),-1.0]])]});}
            var Q131;
            {var subQ0=sQuery(id+"F0.wireOp",EDGE,"E21.5.0.0");var subQ1=sQuery(id+"F0.wireOp",EDGE,"E15.trimOffspring");var subQ2=makeQuery(id+"F0.imprint","INTERSECT",VERTEX,{"derivedFrom":[subQ1,subQ0]});Q131=makeQuery(id+"F0.imprint","IMPRINT",FACE,{"disambiguationData":[TD([[makeQuery(id+"F0.imprint","IMPRINT",EDGE,{"disambiguationData":[TD([[subQ2,-1.0]])],"derivedFrom":subQ1}),1.0]])]});}
            var Q132;
            {var subQ0=sQuery(id+"F0.wireOp",EDGE,"E21.4.0.0");var subQ1=sQuery(id+"F0.wireOp",EDGE,"E1");var subQ2=makeQuery(id+"F0.imprint","INTERSECT",VERTEX,{"derivedFrom":[subQ1,subQ0]});Q132=makeQuery(id+"F0.imprint","IMPRINT",FACE,{"disambiguationData":[TD([[makeQuery(id+"F0.imprint","IMPRINT",EDGE,{"disambiguationData":[TD([[subQ2,-1.0]])],"derivedFrom":subQ1}),-1.0]])]});}
            var Q133;
            {var subQ0=sQuery(id+"F0.wireOp",EDGE,"E22.1.0.0");var subQ1=sQuery(id+"F0.wireOp",EDGE,"E12.trimOffspring");var subQ2=makeQuery(id+"F0.imprint","INTERSECT",VERTEX,{"derivedFrom":[subQ1,subQ0]});Q133=makeQuery(id+"F0.imprint","IMPRINT",FACE,{"disambiguationData":[TD([[makeQuery(id+"F0.imprint","IMPRINT",EDGE,{"disambiguationData":[TD([[subQ2,-1.0]])],"derivedFrom":subQ1}),1.0]])]});}
            var Q134;
            {var subQ0=sQuery(id+"F0.wireOp",EDGE,"E22.1.0.0");var subQ1=sQuery(id+"F0.wireOp",EDGE,"E6.trimOffspring");var subQ2=makeQuery(id+"F0.imprint","INTERSECT",VERTEX,{"derivedFrom":[subQ1,subQ0]});Q134=makeQuery(id+"F0.imprint","IMPRINT",FACE,{"disambiguationData":[TD([[makeQuery(id+"F0.imprint","IMPRINT",EDGE,{"disambiguationData":[TD([[subQ2,-1.0]])],"derivedFrom":subQ1}),1.0]])]});}
            var Q135;
            {var subQ0=sQuery(id+"F0.wireOp",EDGE,"E21.3.0.0");var subQ1=sQuery(id+"F0.wireOp",EDGE,"E14.trimOffspring");var subQ2=makeQuery(id+"F0.imprint","INTERSECT",VERTEX,{"derivedFrom":[subQ1,subQ0]});Q135=makeQuery(id+"F0.imprint","IMPRINT",FACE,{"disambiguationData":[TD([[makeQuery(id+"F0.imprint","IMPRINT",EDGE,{"disambiguationData":[TD([[subQ2,-1.0]])],"derivedFrom":subQ1}),1.0]])]});}
            var Q136;
            {var subQ0=sQuery(id+"F0.wireOp",EDGE,"E21.5.0.0");var subQ1=sQuery(id+"F0.wireOp",EDGE,"E17.trimOffspring");var subQ2=makeQuery(id+"F0.imprint","INTERSECT",VERTEX,{"derivedFrom":[subQ1,subQ0]});Q136=makeQuery(id+"F0.imprint","IMPRINT",FACE,{"disambiguationData":[TD([[makeQuery(id+"F0.imprint","IMPRINT",EDGE,{"disambiguationData":[TD([[subQ2,-1.0]])],"derivedFrom":subQ1}),1.0]])]});}
            var Q137;
            {var subQ0=sQuery(id+"F0.wireOp",EDGE,"E21.2.0.0");var subQ1=sQuery(id+"F0.wireOp",EDGE,"E15.trimOffspring");var subQ2=makeQuery(id+"F0.imprint","INTERSECT",VERTEX,{"derivedFrom":[subQ1,subQ0]});Q137=makeQuery(id+"F0.imprint","IMPRINT",FACE,{"disambiguationData":[TD([[makeQuery(id+"F0.imprint","IMPRINT",EDGE,{"disambiguationData":[TD([[subQ2,-1.0]])],"derivedFrom":subQ1}),1.0]])]});}
            var Q138;
            {var subQ0=sQuery(id+"F0.wireOp",EDGE,"E20");var subQ1=sQuery(id+"F0.wireOp",EDGE,"E2.0.9.0");var subQ2=makeQuery(id+"F0.imprint","INTERSECT",VERTEX,{"derivedFrom":[subQ1,subQ0]});Q138=makeQuery(id+"F0.imprint","IMPRINT",FACE,{"disambiguationData":[TD([[makeQuery(id+"F0.imprint","IMPRINT",EDGE,{"disambiguationData":[TD([[subQ2,-1.0]])],"derivedFrom":subQ1}),-1.0]])]});}
            var Q139;
            {var subQ0=sQuery(id+"F0.wireOp",EDGE,"E21.4.0.0");var subQ1=sQuery(id+"F0.wireOp",EDGE,"E9.trimOffspring");var subQ2=makeQuery(id+"F0.imprint","INTERSECT",VERTEX,{"derivedFrom":[subQ1,subQ0]});Q139=makeQuery(id+"F0.imprint","IMPRINT",FACE,{"disambiguationData":[TD([[makeQuery(id+"F0.imprint","IMPRINT",EDGE,{"disambiguationData":[TD([[subQ2,-1.0]])],"derivedFrom":subQ1}),1.0]])]});}
            var Q140;
            {var subQ0=sQuery(id+"F0.wireOp",EDGE,"E21.4.0.0");var subQ1=sQuery(id+"F0.wireOp",EDGE,"E15.trimOffspring");var subQ2=makeQuery(id+"F0.imprint","INTERSECT",VERTEX,{"derivedFrom":[subQ1,subQ0]});Q140=makeQuery(id+"F0.imprint","IMPRINT",FACE,{"disambiguationData":[TD([[makeQuery(id+"F0.imprint","IMPRINT",EDGE,{"disambiguationData":[TD([[subQ2,-1.0]])],"derivedFrom":subQ1}),1.0]])]});}
            var Q141;
            {var subQ0=sQuery(id+"F0.wireOp",EDGE,"E22.2.0.0");var subQ1=sQuery(id+"F0.wireOp",EDGE,"E16.trimOffspring");var subQ2=makeQuery(id+"F0.imprint","INTERSECT",VERTEX,{"derivedFrom":[subQ1,subQ0]});Q141=makeQuery(id+"F0.imprint","IMPRINT",FACE,{"disambiguationData":[TD([[makeQuery(id+"F0.imprint","IMPRINT",EDGE,{"disambiguationData":[TD([[subQ2,-1.0]])],"derivedFrom":subQ1}),1.0]])]});}
            var Q142;
            {var subQ0=sQuery(id+"F0.wireOp",EDGE,"E22.3.0.0");var subQ1=sQuery(id+"F0.wireOp",EDGE,"E10.trimOffspring");var subQ2=makeQuery(id+"F0.imprint","INTERSECT",VERTEX,{"derivedFrom":[subQ1,subQ0]});Q142=makeQuery(id+"F0.imprint","IMPRINT",FACE,{"disambiguationData":[TD([[makeQuery(id+"F0.imprint","IMPRINT",EDGE,{"disambiguationData":[TD([[subQ2,-1.0]])],"derivedFrom":subQ1}),1.0]])]});}
            var Q143;
            {var subQ0=sQuery(id+"F0.wireOp",EDGE,"E22.3.0.0");var subQ1=sQuery(id+"F0.wireOp",EDGE,"E15.trimOffspring");var subQ2=makeQuery(id+"F0.imprint","INTERSECT",VERTEX,{"derivedFrom":[subQ1,subQ0]});Q143=makeQuery(id+"F0.imprint","IMPRINT",FACE,{"disambiguationData":[TD([[makeQuery(id+"F0.imprint","IMPRINT",EDGE,{"disambiguationData":[TD([[subQ2,-1.0]])],"derivedFrom":subQ1}),1.0]])]});}
            var Q144;
            {var subQ0=sQuery(id+"F0.wireOp",EDGE,"E22.4.0.0");var subQ1=sQuery(id+"F0.wireOp",EDGE,"E14.trimOffspring");var subQ2=makeQuery(id+"F0.imprint","INTERSECT",VERTEX,{"derivedFrom":[subQ1,subQ0]});Q144=makeQuery(id+"F0.imprint","IMPRINT",FACE,{"disambiguationData":[TD([[makeQuery(id+"F0.imprint","IMPRINT",EDGE,{"disambiguationData":[TD([[subQ2,-1.0]])],"derivedFrom":subQ1}),1.0]])]});}
            var Q145;
            {var subQ0=sQuery(id+"F0.wireOp",EDGE,"E22.4.0.0");var subQ1=sQuery(id+"F0.wireOp",EDGE,"E13.trimOffspring");var subQ2=makeQuery(id+"F0.imprint","INTERSECT",VERTEX,{"derivedFrom":[subQ1,subQ0]});Q145=makeQuery(id+"F0.imprint","IMPRINT",FACE,{"disambiguationData":[TD([[makeQuery(id+"F0.imprint","IMPRINT",EDGE,{"disambiguationData":[TD([[subQ2,-1.0]])],"derivedFrom":subQ1}),1.0]])]});}
            var Q146;
            {var subQ0=sQuery(id+"F0.wireOp",EDGE,"E21.5.0.0");var subQ1=sQuery(id+"F0.wireOp",EDGE,"E10.trimOffspring");var subQ2=makeQuery(id+"F0.imprint","INTERSECT",VERTEX,{"derivedFrom":[subQ1,subQ0]});Q146=makeQuery(id+"F0.imprint","IMPRINT",FACE,{"disambiguationData":[TD([[makeQuery(id+"F0.imprint","IMPRINT",EDGE,{"disambiguationData":[TD([[subQ2,-1.0]])],"derivedFrom":subQ1}),1.0]])]});}
            var Q147;
            {var subQ0=sQuery(id+"F0.wireOp",EDGE,"E22.2.0.0");var subQ1=sQuery(id+"F0.wireOp",EDGE,"E5.trimOffspring");var subQ2=makeQuery(id+"F0.imprint","INTERSECT",VERTEX,{"derivedFrom":[subQ1,subQ0]});Q147=makeQuery(id+"F0.imprint","IMPRINT",FACE,{"disambiguationData":[TD([[makeQuery(id+"F0.imprint","IMPRINT",EDGE,{"disambiguationData":[TD([[subQ2,-1.0]])],"derivedFrom":subQ1}),1.0]])]});}
            var Q148;
            {var subQ0=sQuery(id+"F0.wireOp",EDGE,"E21.3.0.0");var subQ1=sQuery(id+"F0.wireOp",EDGE,"E18.trimOffspring");var subQ2=makeQuery(id+"F0.imprint","INTERSECT",VERTEX,{"derivedFrom":[subQ1,subQ0]});Q148=makeQuery(id+"F0.imprint","IMPRINT",FACE,{"disambiguationData":[TD([[makeQuery(id+"F0.imprint","IMPRINT",EDGE,{"disambiguationData":[TD([[subQ2,-1.0]])],"derivedFrom":subQ1}),1.0]])]});}
            var Q149;
            {var subQ0=sQuery(id+"F0.wireOp",EDGE,"E21.2.0.0");var subQ1=sQuery(id+"F0.wireOp",EDGE,"E14.trimOffspring");var subQ2=makeQuery(id+"F0.imprint","INTERSECT",VERTEX,{"derivedFrom":[subQ1,subQ0]});Q149=makeQuery(id+"F0.imprint","IMPRINT",FACE,{"disambiguationData":[TD([[makeQuery(id+"F0.imprint","IMPRINT",EDGE,{"disambiguationData":[TD([[subQ2,-1.0]])],"derivedFrom":subQ1}),1.0]])]});}
            var Q150;
            {var subQ0=sQuery(id+"F0.wireOp",EDGE,"E22.3.0.0");var subQ1=sQuery(id+"F0.wireOp",EDGE,"E18.trimOffspring");var subQ2=makeQuery(id+"F0.imprint","INTERSECT",VERTEX,{"derivedFrom":[subQ1,subQ0]});Q150=makeQuery(id+"F0.imprint","IMPRINT",FACE,{"disambiguationData":[TD([[makeQuery(id+"F0.imprint","IMPRINT",EDGE,{"disambiguationData":[TD([[subQ2,-1.0]])],"derivedFrom":subQ1}),1.0]])]});}
            var Q151;
            {var subQ0=sQuery(id+"F0.wireOp",EDGE,"E22.2.0.0");var subQ1=sQuery(id+"F0.wireOp",EDGE,"E13.trimOffspring");var subQ2=makeQuery(id+"F0.imprint","INTERSECT",VERTEX,{"derivedFrom":[subQ1,subQ0]});Q151=makeQuery(id+"F0.imprint","IMPRINT",FACE,{"disambiguationData":[TD([[makeQuery(id+"F0.imprint","IMPRINT",EDGE,{"disambiguationData":[TD([[subQ2,-1.0]])],"derivedFrom":subQ1}),1.0]])]});}
            var Q152;
            {var subQ0=sQuery(id+"F0.wireOp",EDGE,"E22.1.0.0");var subQ1=sQuery(id+"F0.wireOp",EDGE,"E18.trimOffspring");var subQ2=makeQuery(id+"F0.imprint","INTERSECT",VERTEX,{"derivedFrom":[subQ1,subQ0]});Q152=makeQuery(id+"F0.imprint","IMPRINT",FACE,{"disambiguationData":[TD([[makeQuery(id+"F0.imprint","IMPRINT",EDGE,{"disambiguationData":[TD([[subQ2,-1.0]])],"derivedFrom":subQ1}),1.0]])]});}
            var Q153;
            {var subQ0=sQuery(id+"F0.wireOp",EDGE,"E21.4.0.0");var subQ1=sQuery(id+"F0.wireOp",EDGE,"E1");var subQ2=makeQuery(id+"F0.imprint","INTERSECT",VERTEX,{"derivedFrom":[subQ1,subQ0]});Q153=makeQuery(id+"F0.imprint","IMPRINT",FACE,{"disambiguationData":[TD([[makeQuery(id+"F0.imprint","IMPRINT",EDGE,{"disambiguationData":[TD([[subQ2,-1.0]])],"derivedFrom":subQ1}),1.0]])]});}
            var Q154;
            {var subQ0=sQuery(id+"F0.wireOp",EDGE,"E22.5.0.0");var subQ1=sQuery(id+"F0.wireOp",EDGE,"E1");var subQ2=makeQuery(id+"F0.imprint","INTERSECT",VERTEX,{"derivedFrom":[subQ1,subQ0]});Q154=makeQuery(id+"F0.imprint","IMPRINT",FACE,{"disambiguationData":[TD([[makeQuery(id+"F0.imprint","IMPRINT",EDGE,{"disambiguationData":[TD([[subQ2,-1.0]])],"derivedFrom":subQ1}),-1.0]])]});}
            var Q155;
            {var subQ0=sQuery(id+"F0.wireOp",EDGE,"E22.1.0.0");var subQ1=sQuery(id+"F0.wireOp",EDGE,"E2.0.9.0");var subQ2=makeQuery(id+"F0.imprint","INTERSECT",VERTEX,{"derivedFrom":[subQ1,subQ0]});Q155=makeQuery(id+"F0.imprint","IMPRINT",FACE,{"disambiguationData":[TD([[makeQuery(id+"F0.imprint","IMPRINT",EDGE,{"disambiguationData":[TD([[subQ2,-1.0]])],"derivedFrom":subQ1}),-1.0]])]});}
            var Q156;
            {var subQ0=sQuery(id+"F0.wireOp",EDGE,"E21.3.0.0");var subQ1=sQuery(id+"F0.wireOp",EDGE,"E1");var subQ2=makeQuery(id+"F0.imprint","INTERSECT",VERTEX,{"derivedFrom":[subQ1,subQ0]});Q156=makeQuery(id+"F0.imprint","IMPRINT",FACE,{"disambiguationData":[TD([[makeQuery(id+"F0.imprint","IMPRINT",EDGE,{"disambiguationData":[TD([[subQ2,-1.0]])],"derivedFrom":subQ1}),1.0]])]});}
            var Q157;
            {var subQ0=sQuery(id+"F0.wireOp",EDGE,"E21.5.0.0");var subQ1=sQuery(id+"F0.wireOp",EDGE,"E2.0.9.0");var subQ2=makeQuery(id+"F0.imprint","INTERSECT",VERTEX,{"derivedFrom":[subQ1,subQ0]});Q157=makeQuery(id+"F0.imprint","IMPRINT",FACE,{"disambiguationData":[TD([[makeQuery(id+"F0.imprint","IMPRINT",EDGE,{"disambiguationData":[TD([[subQ2,-1.0]])],"derivedFrom":subQ1}),-1.0]])]});}
            var Q158;
            {var subQ0=sQuery(id+"F0.wireOp",EDGE,"E21.5.0.0");var subQ1=sQuery(id+"F0.wireOp",EDGE,"E13.trimOffspring");var subQ2=makeQuery(id+"F0.imprint","INTERSECT",VERTEX,{"derivedFrom":[subQ1,subQ0]});Q158=makeQuery(id+"F0.imprint","IMPRINT",FACE,{"disambiguationData":[TD([[makeQuery(id+"F0.imprint","IMPRINT",EDGE,{"disambiguationData":[TD([[subQ2,-1.0]])],"derivedFrom":subQ1}),1.0]])]});}
            var Q159;
            {var subQ0=sQuery(id+"F0.wireOp",EDGE,"E22.3.0.0");var subQ1=sQuery(id+"F0.wireOp",EDGE,"E13.trimOffspring");var subQ2=makeQuery(id+"F0.imprint","INTERSECT",VERTEX,{"derivedFrom":[subQ1,subQ0]});Q159=makeQuery(id+"F0.imprint","IMPRINT",FACE,{"disambiguationData":[TD([[makeQuery(id+"F0.imprint","IMPRINT",EDGE,{"disambiguationData":[TD([[subQ2,-1.0]])],"derivedFrom":subQ1}),1.0]])]});}
            var Q160;
            {var subQ0=sQuery(id+"F0.wireOp",EDGE,"E22.5.0.0");var subQ1=sQuery(id+"F0.wireOp",EDGE,"E18.trimOffspring");var subQ2=makeQuery(id+"F0.imprint","INTERSECT",VERTEX,{"derivedFrom":[subQ1,subQ0]});Q160=makeQuery(id+"F0.imprint","IMPRINT",FACE,{"disambiguationData":[TD([[makeQuery(id+"F0.imprint","IMPRINT",EDGE,{"disambiguationData":[TD([[subQ2,-1.0]])],"derivedFrom":subQ1}),1.0]])]});}
            var Q161;
            {var subQ0=sQuery(id+"F0.wireOp",EDGE,"E21.3.0.0");var subQ1=sQuery(id+"F0.wireOp",EDGE,"E17.trimOffspring");var subQ2=makeQuery(id+"F0.imprint","INTERSECT",VERTEX,{"derivedFrom":[subQ1,subQ0]});Q161=makeQuery(id+"F0.imprint","IMPRINT",FACE,{"disambiguationData":[TD([[makeQuery(id+"F0.imprint","IMPRINT",EDGE,{"disambiguationData":[TD([[subQ2,-1.0]])],"derivedFrom":subQ1}),1.0]])]});}
            var Q162;
            {var subQ0=sQuery(id+"F0.wireOp",EDGE,"E21.1.0.0");var subQ1=sQuery(id+"F0.wireOp",EDGE,"E18.trimOffspring");var subQ2=makeQuery(id+"F0.imprint","INTERSECT",VERTEX,{"derivedFrom":[subQ1,subQ0]});Q162=makeQuery(id+"F0.imprint","IMPRINT",FACE,{"disambiguationData":[TD([[makeQuery(id+"F0.imprint","IMPRINT",EDGE,{"disambiguationData":[TD([[subQ2,-1.0]])],"derivedFrom":subQ1}),1.0]])]});}
            var Q163;
            {var subQ0=sQuery(id+"F0.wireOp",EDGE,"E21.4.0.0");var subQ1=sQuery(id+"F0.wireOp",EDGE,"E13.trimOffspring");var subQ2=makeQuery(id+"F0.imprint","INTERSECT",VERTEX,{"derivedFrom":[subQ1,subQ0]});Q163=makeQuery(id+"F0.imprint","IMPRINT",FACE,{"disambiguationData":[TD([[makeQuery(id+"F0.imprint","IMPRINT",EDGE,{"disambiguationData":[TD([[subQ2,-1.0]])],"derivedFrom":subQ1}),1.0]])]});}
            var Q164;
            {var subQ0=sQuery(id+"F0.wireOp",EDGE,"E22.1.0.0");var subQ1=sQuery(id+"F0.wireOp",EDGE,"E15.trimOffspring");var subQ2=makeQuery(id+"F0.imprint","INTERSECT",VERTEX,{"derivedFrom":[subQ1,subQ0]});Q164=makeQuery(id+"F0.imprint","IMPRINT",FACE,{"disambiguationData":[TD([[makeQuery(id+"F0.imprint","IMPRINT",EDGE,{"disambiguationData":[TD([[subQ2,-1.0]])],"derivedFrom":subQ1}),1.0]])]});}
            var Q165;
            {var subQ0=sQuery(id+"F0.wireOp",EDGE,"E20");var subQ1=sQuery(id+"F0.wireOp",EDGE,"E4.trimOffspring");var subQ2=makeQuery(id+"F0.imprint","INTERSECT",VERTEX,{"derivedFrom":[subQ1,subQ0]});Q165=makeQuery(id+"F0.imprint","IMPRINT",FACE,{"disambiguationData":[TD([[makeQuery(id+"F0.imprint","IMPRINT",EDGE,{"disambiguationData":[TD([[subQ2,-1.0]])],"derivedFrom":subQ1}),1.0]])]});}
            var Q166;
            {var subQ0=sQuery(id+"F0.wireOp",EDGE,"E21.5.0.0");var subQ1=sQuery(id+"F0.wireOp",EDGE,"E8.trimOffspring");var subQ2=makeQuery(id+"F0.imprint","INTERSECT",VERTEX,{"derivedFrom":[subQ1,subQ0]});Q166=makeQuery(id+"F0.imprint","IMPRINT",FACE,{"disambiguationData":[TD([[makeQuery(id+"F0.imprint","IMPRINT",EDGE,{"disambiguationData":[TD([[subQ2,-1.0]])],"derivedFrom":subQ1}),1.0]])]});}
            var Q167;
            {var subQ0=sQuery(id+"F0.wireOp",EDGE,"E21.1.0.0");var subQ1=sQuery(id+"F0.wireOp",EDGE,"E5.trimOffspring");var subQ2=makeQuery(id+"F0.imprint","INTERSECT",VERTEX,{"derivedFrom":[subQ1,subQ0]});Q167=makeQuery(id+"F0.imprint","IMPRINT",FACE,{"disambiguationData":[TD([[makeQuery(id+"F0.imprint","IMPRINT",EDGE,{"disambiguationData":[TD([[subQ2,-1.0]])],"derivedFrom":subQ1}),1.0]])]});}
            var Q168;
            {var subQ0=sQuery(id+"F0.wireOp",EDGE,"E22.2.0.0");var subQ1=sQuery(id+"F0.wireOp",EDGE,"E18.trimOffspring");var subQ2=makeQuery(id+"F0.imprint","INTERSECT",VERTEX,{"derivedFrom":[subQ1,subQ0]});Q168=makeQuery(id+"F0.imprint","IMPRINT",FACE,{"disambiguationData":[TD([[makeQuery(id+"F0.imprint","IMPRINT",EDGE,{"disambiguationData":[TD([[subQ2,-1.0]])],"derivedFrom":subQ1}),1.0]])]});}
            var Q169;
            {var subQ0=sQuery(id+"F0.wireOp",EDGE,"E22.4.0.0");var subQ1=sQuery(id+"F0.wireOp",EDGE,"E4.trimOffspring");var subQ2=makeQuery(id+"F0.imprint","INTERSECT",VERTEX,{"derivedFrom":[subQ1,subQ0]});Q169=makeQuery(id+"F0.imprint","IMPRINT",FACE,{"disambiguationData":[TD([[makeQuery(id+"F0.imprint","IMPRINT",EDGE,{"disambiguationData":[TD([[subQ2,-1.0]])],"derivedFrom":subQ1}),1.0]])]});}
            var Q170;
            {var subQ0=sQuery(id+"F0.wireOp",EDGE,"E21.3.0.0");var subQ1=sQuery(id+"F0.wireOp",EDGE,"E4.trimOffspring");var subQ2=makeQuery(id+"F0.imprint","INTERSECT",VERTEX,{"derivedFrom":[subQ1,subQ0]});Q170=makeQuery(id+"F0.imprint","IMPRINT",FACE,{"disambiguationData":[TD([[makeQuery(id+"F0.imprint","IMPRINT",EDGE,{"disambiguationData":[TD([[subQ2,-1.0]])],"derivedFrom":subQ1}),1.0]])]});}
            var Q171;
            {var subQ0=sQuery(id+"F0.wireOp",EDGE,"E21.4.0.0");var subQ1=sQuery(id+"F0.wireOp",EDGE,"E18.trimOffspring");var subQ2=makeQuery(id+"F0.imprint","INTERSECT",VERTEX,{"derivedFrom":[subQ1,subQ0]});Q171=makeQuery(id+"F0.imprint","IMPRINT",FACE,{"disambiguationData":[TD([[makeQuery(id+"F0.imprint","IMPRINT",EDGE,{"disambiguationData":[TD([[subQ2,-1.0]])],"derivedFrom":subQ1}),1.0]])]});}
            var Q172;
            {var subQ0=sQuery(id+"F0.wireOp",EDGE,"E21.1.0.0");var subQ1=sQuery(id+"F0.wireOp",EDGE,"E14.trimOffspring");var subQ2=makeQuery(id+"F0.imprint","INTERSECT",VERTEX,{"derivedFrom":[subQ1,subQ0]});Q172=makeQuery(id+"F0.imprint","IMPRINT",FACE,{"disambiguationData":[TD([[makeQuery(id+"F0.imprint","IMPRINT",EDGE,{"disambiguationData":[TD([[subQ2,-1.0]])],"derivedFrom":subQ1}),1.0]])]});}
            var Q173;
            {var subQ0=sQuery(id+"F0.wireOp",EDGE,"E22.2.0.0");var subQ1=sQuery(id+"F0.wireOp",EDGE,"E9.trimOffspring");var subQ2=makeQuery(id+"F0.imprint","INTERSECT",VERTEX,{"derivedFrom":[subQ1,subQ0]});Q173=makeQuery(id+"F0.imprint","IMPRINT",FACE,{"disambiguationData":[TD([[makeQuery(id+"F0.imprint","IMPRINT",EDGE,{"disambiguationData":[TD([[subQ2,-1.0]])],"derivedFrom":subQ1}),1.0]])]});}
            var Q174;
            {var subQ0=sQuery(id+"F0.wireOp",EDGE,"E21.2.0.0");var subQ1=sQuery(id+"F0.wireOp",EDGE,"E16.trimOffspring");var subQ2=makeQuery(id+"F0.imprint","INTERSECT",VERTEX,{"derivedFrom":[subQ1,subQ0]});Q174=makeQuery(id+"F0.imprint","IMPRINT",FACE,{"disambiguationData":[TD([[makeQuery(id+"F0.imprint","IMPRINT",EDGE,{"disambiguationData":[TD([[subQ2,-1.0]])],"derivedFrom":subQ1}),1.0]])]});}
            var Q175;
            {var subQ0=sQuery(id+"F0.wireOp",EDGE,"E22.4.0.0");var subQ1=sQuery(id+"F0.wireOp",EDGE,"E9.trimOffspring");var subQ2=makeQuery(id+"F0.imprint","INTERSECT",VERTEX,{"derivedFrom":[subQ1,subQ0]});Q175=makeQuery(id+"F0.imprint","IMPRINT",FACE,{"disambiguationData":[TD([[makeQuery(id+"F0.imprint","IMPRINT",EDGE,{"disambiguationData":[TD([[subQ2,-1.0]])],"derivedFrom":subQ1}),1.0]])]});}
            var Q176;
            {var subQ0=sQuery(id+"F0.wireOp",EDGE,"E22.5.0.0");var subQ1=sQuery(id+"F0.wireOp",EDGE,"E6.trimOffspring");var subQ2=makeQuery(id+"F0.imprint","INTERSECT",VERTEX,{"derivedFrom":[subQ1,subQ0]});Q176=makeQuery(id+"F0.imprint","IMPRINT",FACE,{"disambiguationData":[TD([[makeQuery(id+"F0.imprint","IMPRINT",EDGE,{"disambiguationData":[TD([[subQ2,-1.0]])],"derivedFrom":subQ1}),1.0]])]});}
            var Q177;
            {var subQ0=sQuery(id+"F0.wireOp",EDGE,"E21.4.0.0");var subQ1=sQuery(id+"F0.wireOp",EDGE,"E12.trimOffspring");var subQ2=makeQuery(id+"F0.imprint","INTERSECT",VERTEX,{"derivedFrom":[subQ1,subQ0]});Q177=makeQuery(id+"F0.imprint","IMPRINT",FACE,{"disambiguationData":[TD([[makeQuery(id+"F0.imprint","IMPRINT",EDGE,{"disambiguationData":[TD([[subQ2,-1.0]])],"derivedFrom":subQ1}),1.0]])]});}
            var Q178;
            {var subQ0=sQuery(id+"F0.wireOp",EDGE,"E20");var subQ1=sQuery(id+"F0.wireOp",EDGE,"E15.trimOffspring");var subQ2=makeQuery(id+"F0.imprint","INTERSECT",VERTEX,{"derivedFrom":[subQ1,subQ0]});Q178=makeQuery(id+"F0.imprint","IMPRINT",FACE,{"disambiguationData":[TD([[makeQuery(id+"F0.imprint","IMPRINT",EDGE,{"disambiguationData":[TD([[subQ2,-1.0]])],"derivedFrom":subQ1}),1.0]])]});}
            var Q179;
            {var subQ0=sQuery(id+"F0.wireOp",EDGE,"E22.3.0.0");var subQ1=sQuery(id+"F0.wireOp",EDGE,"E9.trimOffspring");var subQ2=makeQuery(id+"F0.imprint","INTERSECT",VERTEX,{"derivedFrom":[subQ1,subQ0]});Q179=makeQuery(id+"F0.imprint","IMPRINT",FACE,{"disambiguationData":[TD([[makeQuery(id+"F0.imprint","IMPRINT",EDGE,{"disambiguationData":[TD([[subQ2,-1.0]])],"derivedFrom":subQ1}),1.0]])]});}
            var Q180;
            {var subQ0=sQuery(id+"F0.wireOp",EDGE,"E21.2.0.0");var subQ1=sQuery(id+"F0.wireOp",EDGE,"E18.trimOffspring");var subQ2=makeQuery(id+"F0.imprint","INTERSECT",VERTEX,{"derivedFrom":[subQ1,subQ0]});Q180=makeQuery(id+"F0.imprint","IMPRINT",FACE,{"disambiguationData":[TD([[makeQuery(id+"F0.imprint","IMPRINT",EDGE,{"disambiguationData":[TD([[subQ2,-1.0]])],"derivedFrom":subQ1}),1.0]])]});}
            var Q181;
            {var subQ0=sQuery(id+"F0.wireOp",EDGE,"E21.1.0.0");var subQ1=sQuery(id+"F0.wireOp",EDGE,"E10.trimOffspring");var subQ2=makeQuery(id+"F0.imprint","INTERSECT",VERTEX,{"derivedFrom":[subQ1,subQ0]});Q181=makeQuery(id+"F0.imprint","IMPRINT",FACE,{"disambiguationData":[TD([[makeQuery(id+"F0.imprint","IMPRINT",EDGE,{"disambiguationData":[TD([[subQ2,-1.0]])],"derivedFrom":subQ1}),1.0]])]});}
            var Q182;
            {var subQ0=sQuery(id+"F0.wireOp",EDGE,"E21.4.0.0");var subQ1=sQuery(id+"F0.wireOp",EDGE,"E17.trimOffspring");var subQ2=makeQuery(id+"F0.imprint","INTERSECT",VERTEX,{"derivedFrom":[subQ1,subQ0]});Q182=makeQuery(id+"F0.imprint","IMPRINT",FACE,{"disambiguationData":[TD([[makeQuery(id+"F0.imprint","IMPRINT",EDGE,{"disambiguationData":[TD([[subQ2,-1.0]])],"derivedFrom":subQ1}),1.0]])]});}
            var Q183;
            {var subQ0=sQuery(id+"F0.wireOp",EDGE,"E22.4.0.0");var subQ1=sQuery(id+"F0.wireOp",EDGE,"E18.trimOffspring");var subQ2=makeQuery(id+"F0.imprint","INTERSECT",VERTEX,{"derivedFrom":[subQ1,subQ0]});Q183=makeQuery(id+"F0.imprint","IMPRINT",FACE,{"disambiguationData":[TD([[makeQuery(id+"F0.imprint","IMPRINT",EDGE,{"disambiguationData":[TD([[subQ2,-1.0]])],"derivedFrom":subQ1}),1.0]])]});}
            var Q184;
            {var subQ0=sQuery(id+"F0.wireOp",EDGE,"E22.5.0.0");var subQ1=sQuery(id+"F0.wireOp",EDGE,"E16.trimOffspring");var subQ2=makeQuery(id+"F0.imprint","INTERSECT",VERTEX,{"derivedFrom":[subQ1,subQ0]});Q184=makeQuery(id+"F0.imprint","IMPRINT",FACE,{"disambiguationData":[TD([[makeQuery(id+"F0.imprint","IMPRINT",EDGE,{"disambiguationData":[TD([[subQ2,-1.0]])],"derivedFrom":subQ1}),1.0]])]});}
            var Q185;
            {var subQ0=sQuery(id+"F0.wireOp",EDGE,"E22.4.0.0");var subQ1=sQuery(id+"F0.wireOp",EDGE,"E2.0.9.0");var subQ2=makeQuery(id+"F0.imprint","INTERSECT",VERTEX,{"derivedFrom":[subQ1,subQ0]});Q185=makeQuery(id+"F0.imprint","IMPRINT",FACE,{"disambiguationData":[TD([[makeQuery(id+"F0.imprint","IMPRINT",EDGE,{"disambiguationData":[TD([[subQ2,-1.0]])],"derivedFrom":subQ1}),-1.0]])]});}
            var Q186;
            {var subQ0=sQuery(id+"F0.wireOp",EDGE,"E22.5.0.0");var subQ1=sQuery(id+"F0.wireOp",EDGE,"E1");var subQ2=makeQuery(id+"F0.imprint","INTERSECT",VERTEX,{"derivedFrom":[subQ1,subQ0]});Q186=makeQuery(id+"F0.imprint","IMPRINT",FACE,{"disambiguationData":[TD([[makeQuery(id+"F0.imprint","IMPRINT",EDGE,{"disambiguationData":[TD([[subQ2,-1.0]])],"derivedFrom":subQ1}),1.0]])]});}
            var Q187;
            {var subQ0=sQuery(id+"F0.wireOp",EDGE,"E22.6.0.0");var subQ1=sQuery(id+"F0.wireOp",EDGE,"E2.0.9.0");var subQ2=makeQuery(id+"F0.imprint","INTERSECT",VERTEX,{"derivedFrom":[subQ1,subQ0]});Q187=makeQuery(id+"F0.imprint","IMPRINT",FACE,{"disambiguationData":[TD([[makeQuery(id+"F0.imprint","IMPRINT",EDGE,{"disambiguationData":[TD([[subQ2,-1.0]])],"derivedFrom":subQ1}),-1.0]])]});}
            var Q188;
            {var subQ0=sQuery(id+"F0.wireOp",EDGE,"E22.6.0.0");var subQ1=sQuery(id+"F0.wireOp",EDGE,"E18.trimOffspring");var subQ2=makeQuery(id+"F0.imprint","INTERSECT",VERTEX,{"derivedFrom":[subQ1,subQ0]});Q188=makeQuery(id+"F0.imprint","IMPRINT",FACE,{"disambiguationData":[TD([[makeQuery(id+"F0.imprint","IMPRINT",EDGE,{"disambiguationData":[TD([[subQ2,-1.0]])],"derivedFrom":subQ1}),1.0]])]});}
            var Q189;
            {var subQ0=sQuery(id+"F0.wireOp",EDGE,"E22.6.0.0");var subQ1=sQuery(id+"F0.wireOp",EDGE,"E17.trimOffspring");var subQ2=makeQuery(id+"F0.imprint","INTERSECT",VERTEX,{"derivedFrom":[subQ1,subQ0]});Q189=makeQuery(id+"F0.imprint","IMPRINT",FACE,{"disambiguationData":[TD([[makeQuery(id+"F0.imprint","IMPRINT",EDGE,{"disambiguationData":[TD([[subQ2,-1.0]])],"derivedFrom":subQ1}),1.0]])]});}
            var Q190;
            {var subQ0=sQuery(id+"F0.wireOp",EDGE,"E22.6.0.0");var subQ1=sQuery(id+"F0.wireOp",EDGE,"E16.trimOffspring");var subQ2=makeQuery(id+"F0.imprint","INTERSECT",VERTEX,{"derivedFrom":[subQ1,subQ0]});Q190=makeQuery(id+"F0.imprint","IMPRINT",FACE,{"disambiguationData":[TD([[makeQuery(id+"F0.imprint","IMPRINT",EDGE,{"disambiguationData":[TD([[subQ2,-1.0]])],"derivedFrom":subQ1}),1.0]])]});}
            var Q191;
            {var subQ0=sQuery(id+"F0.wireOp",EDGE,"E22.6.0.0");var subQ1=sQuery(id+"F0.wireOp",EDGE,"E15.trimOffspring");var subQ2=makeQuery(id+"F0.imprint","INTERSECT",VERTEX,{"derivedFrom":[subQ1,subQ0]});Q191=makeQuery(id+"F0.imprint","IMPRINT",FACE,{"disambiguationData":[TD([[makeQuery(id+"F0.imprint","IMPRINT",EDGE,{"disambiguationData":[TD([[subQ2,-1.0]])],"derivedFrom":subQ1}),1.0]])]});}
            var Q192;
            {var subQ0=sQuery(id+"F0.wireOp",EDGE,"E22.6.0.0");var subQ1=sQuery(id+"F0.wireOp",EDGE,"E14.trimOffspring");var subQ2=makeQuery(id+"F0.imprint","INTERSECT",VERTEX,{"derivedFrom":[subQ1,subQ0]});Q192=makeQuery(id+"F0.imprint","IMPRINT",FACE,{"disambiguationData":[TD([[makeQuery(id+"F0.imprint","IMPRINT",EDGE,{"disambiguationData":[TD([[subQ2,-1.0]])],"derivedFrom":subQ1}),1.0]])]});}
            var Q193;
            {var subQ0=sQuery(id+"F0.wireOp",EDGE,"E22.6.0.0");var subQ1=sQuery(id+"F0.wireOp",EDGE,"E13.trimOffspring");var subQ2=makeQuery(id+"F0.imprint","INTERSECT",VERTEX,{"derivedFrom":[subQ1,subQ0]});Q193=makeQuery(id+"F0.imprint","IMPRINT",FACE,{"disambiguationData":[TD([[makeQuery(id+"F0.imprint","IMPRINT",EDGE,{"disambiguationData":[TD([[subQ2,-1.0]])],"derivedFrom":subQ1}),1.0]])]});}
            var Q194;
            {var subQ0=sQuery(id+"F0.wireOp",EDGE,"E22.6.0.0");var subQ1=sQuery(id+"F0.wireOp",EDGE,"E12.trimOffspring");var subQ2=makeQuery(id+"F0.imprint","INTERSECT",VERTEX,{"derivedFrom":[subQ1,subQ0]});Q194=makeQuery(id+"F0.imprint","IMPRINT",FACE,{"disambiguationData":[TD([[makeQuery(id+"F0.imprint","IMPRINT",EDGE,{"disambiguationData":[TD([[subQ2,-1.0]])],"derivedFrom":subQ1}),1.0]])]});}
            var Q195;
            {var subQ0=sQuery(id+"F0.wireOp",EDGE,"E22.6.0.0");var subQ1=sQuery(id+"F0.wireOp",EDGE,"E1");var subQ2=makeQuery(id+"F0.imprint","INTERSECT",VERTEX,{"derivedFrom":[subQ1,subQ0]});Q195=makeQuery(id+"F0.imprint","IMPRINT",FACE,{"disambiguationData":[TD([[makeQuery(id+"F0.imprint","IMPRINT",EDGE,{"disambiguationData":[TD([[subQ2,-1.0]])],"derivedFrom":subQ1}),1.0]])]});}
            var Q196;
            {var subQ0=sQuery(id+"F0.wireOp",EDGE,"E22.6.0.0");var subQ1=sQuery(id+"F0.wireOp",EDGE,"E1");var subQ2=makeQuery(id+"F0.imprint","INTERSECT",VERTEX,{"derivedFrom":[subQ1,subQ0]});Q196=makeQuery(id+"F0.imprint","IMPRINT",FACE,{"disambiguationData":[TD([[makeQuery(id+"F0.imprint","IMPRINT",EDGE,{"disambiguationData":[TD([[subQ2,-1.0]])],"derivedFrom":subQ1}),-1.0]])]});}
            var Q197;
            {var subQ0=sQuery(id+"F0.wireOp",EDGE,"E22.6.0.0");var subQ1=sQuery(id+"F0.wireOp",EDGE,"E10.trimOffspring");var subQ2=makeQuery(id+"F0.imprint","INTERSECT",VERTEX,{"derivedFrom":[subQ1,subQ0]});Q197=makeQuery(id+"F0.imprint","IMPRINT",FACE,{"disambiguationData":[TD([[makeQuery(id+"F0.imprint","IMPRINT",EDGE,{"disambiguationData":[TD([[subQ2,-1.0]])],"derivedFrom":subQ1}),1.0]])]});}
            var Q198;
            {var subQ0=sQuery(id+"F0.wireOp",EDGE,"E22.6.0.0");var subQ1=sQuery(id+"F0.wireOp",EDGE,"E9.trimOffspring");var subQ2=makeQuery(id+"F0.imprint","INTERSECT",VERTEX,{"derivedFrom":[subQ1,subQ0]});Q198=makeQuery(id+"F0.imprint","IMPRINT",FACE,{"disambiguationData":[TD([[makeQuery(id+"F0.imprint","IMPRINT",EDGE,{"disambiguationData":[TD([[subQ2,-1.0]])],"derivedFrom":subQ1}),1.0]])]});}
            var Q199;
            {var subQ0=sQuery(id+"F0.wireOp",EDGE,"E22.6.0.0");var subQ1=sQuery(id+"F0.wireOp",EDGE,"E8.trimOffspring");var subQ2=makeQuery(id+"F0.imprint","INTERSECT",VERTEX,{"derivedFrom":[subQ1,subQ0]});Q199=makeQuery(id+"F0.imprint","IMPRINT",FACE,{"disambiguationData":[TD([[makeQuery(id+"F0.imprint","IMPRINT",EDGE,{"disambiguationData":[TD([[subQ2,-1.0]])],"derivedFrom":subQ1}),1.0]])]});}
            var Q200;
            {var subQ0=sQuery(id+"F0.wireOp",EDGE,"E22.6.0.0");var subQ1=sQuery(id+"F0.wireOp",EDGE,"E7.trimOffspring");var subQ2=makeQuery(id+"F0.imprint","INTERSECT",VERTEX,{"derivedFrom":[subQ1,subQ0]});Q200=makeQuery(id+"F0.imprint","IMPRINT",FACE,{"disambiguationData":[TD([[makeQuery(id+"F0.imprint","IMPRINT",EDGE,{"disambiguationData":[TD([[subQ2,-1.0]])],"derivedFrom":subQ1}),1.0]])]});}
            var Q201;
            {var subQ0=sQuery(id+"F0.wireOp",EDGE,"E22.6.0.0");var subQ1=sQuery(id+"F0.wireOp",EDGE,"E6.trimOffspring");var subQ2=makeQuery(id+"F0.imprint","INTERSECT",VERTEX,{"derivedFrom":[subQ1,subQ0]});Q201=makeQuery(id+"F0.imprint","IMPRINT",FACE,{"disambiguationData":[TD([[makeQuery(id+"F0.imprint","IMPRINT",EDGE,{"disambiguationData":[TD([[subQ2,-1.0]])],"derivedFrom":subQ1}),1.0]])]});}
            var Q202;
            {var subQ0=sQuery(id+"F0.wireOp",EDGE,"E22.6.0.0");var subQ1=sQuery(id+"F0.wireOp",EDGE,"E5.trimOffspring");var subQ2=makeQuery(id+"F0.imprint","INTERSECT",VERTEX,{"derivedFrom":[subQ1,subQ0]});Q202=makeQuery(id+"F0.imprint","IMPRINT",FACE,{"disambiguationData":[TD([[makeQuery(id+"F0.imprint","IMPRINT",EDGE,{"disambiguationData":[TD([[subQ2,-1.0]])],"derivedFrom":subQ1}),1.0]])]});}
            var Q203;
            {var subQ0=sQuery(id+"F0.wireOp",EDGE,"E22.6.0.0");var subQ1=sQuery(id+"F0.wireOp",EDGE,"E4.trimOffspring");var subQ2=makeQuery(id+"F0.imprint","INTERSECT",VERTEX,{"derivedFrom":[subQ1,subQ0]});Q203=makeQuery(id+"F0.imprint","IMPRINT",FACE,{"disambiguationData":[TD([[makeQuery(id+"F0.imprint","IMPRINT",EDGE,{"disambiguationData":[TD([[subQ2,-1.0]])],"derivedFrom":subQ1}),1.0]])]});}
            var Q204;
            {var subQ0=sQuery(id+"F0.wireOp",EDGE,"E23.trimOffspring");var subQ1=sQuery(id+"F0.wireOp",EDGE,"E4.trimOffspring");var subQ2=makeQuery(id+"F0.imprint","INTERSECT",VERTEX,{"derivedFrom":[subQ1,subQ0]});Q204=makeQuery(id+"F0.imprint","IMPRINT",FACE,{"disambiguationData":[TD([[makeQuery(id+"F0.imprint","IMPRINT",EDGE,{"disambiguationData":[TD([[subQ2,-1.0]])],"derivedFrom":subQ1}),1.0]])]});}
            var Q205;
            {var subQ0=sQuery(id+"F0.wireOp",EDGE,"E23.trimOffspring");var subQ1=sQuery(id+"F0.wireOp",EDGE,"E5.trimOffspring");var subQ2=makeQuery(id+"F0.imprint","INTERSECT",VERTEX,{"derivedFrom":[subQ1,subQ0]});Q205=makeQuery(id+"F0.imprint","IMPRINT",FACE,{"disambiguationData":[TD([[makeQuery(id+"F0.imprint","IMPRINT",EDGE,{"disambiguationData":[TD([[subQ2,-1.0]])],"derivedFrom":subQ1}),1.0]])]});}
            var Q206;
            {var subQ0=sQuery(id+"F0.wireOp",EDGE,"E23.trimOffspring");var subQ1=sQuery(id+"F0.wireOp",EDGE,"E6.trimOffspring");var subQ2=makeQuery(id+"F0.imprint","INTERSECT",VERTEX,{"derivedFrom":[subQ1,subQ0]});Q206=makeQuery(id+"F0.imprint","IMPRINT",FACE,{"disambiguationData":[TD([[makeQuery(id+"F0.imprint","IMPRINT",EDGE,{"disambiguationData":[TD([[subQ2,-1.0]])],"derivedFrom":subQ1}),1.0]])]});}
            var Q207;
            {var subQ0=sQuery(id+"F0.wireOp",EDGE,"E23.trimOffspring");var subQ1=sQuery(id+"F0.wireOp",EDGE,"E7.trimOffspring");var subQ2=makeQuery(id+"F0.imprint","INTERSECT",VERTEX,{"derivedFrom":[subQ1,subQ0]});Q207=makeQuery(id+"F0.imprint","IMPRINT",FACE,{"disambiguationData":[TD([[makeQuery(id+"F0.imprint","IMPRINT",EDGE,{"disambiguationData":[TD([[subQ2,-1.0]])],"derivedFrom":subQ1}),1.0]])]});}
            var Q208;
            {var subQ0=sQuery(id+"F0.wireOp",EDGE,"E23.trimOffspring");var subQ1=sQuery(id+"F0.wireOp",EDGE,"E8.trimOffspring");var subQ2=makeQuery(id+"F0.imprint","INTERSECT",VERTEX,{"derivedFrom":[subQ1,subQ0]});Q208=makeQuery(id+"F0.imprint","IMPRINT",FACE,{"disambiguationData":[TD([[makeQuery(id+"F0.imprint","IMPRINT",EDGE,{"disambiguationData":[TD([[subQ2,-1.0]])],"derivedFrom":subQ1}),1.0]])]});}
            var Q209;
            {var subQ0=sQuery(id+"F0.wireOp",EDGE,"E23.trimOffspring");var subQ1=sQuery(id+"F0.wireOp",EDGE,"E9.trimOffspring");var subQ2=makeQuery(id+"F0.imprint","INTERSECT",VERTEX,{"derivedFrom":[subQ1,subQ0]});Q209=makeQuery(id+"F0.imprint","IMPRINT",FACE,{"disambiguationData":[TD([[makeQuery(id+"F0.imprint","IMPRINT",EDGE,{"disambiguationData":[TD([[subQ2,-1.0]])],"derivedFrom":subQ1}),1.0]])]});}
            var Q210;
            {var subQ0=sQuery(id+"F0.wireOp",EDGE,"E23.trimOffspring");var subQ1=sQuery(id+"F0.wireOp",EDGE,"E10.trimOffspring");var subQ2=makeQuery(id+"F0.imprint","INTERSECT",VERTEX,{"derivedFrom":[subQ1,subQ0]});Q210=makeQuery(id+"F0.imprint","IMPRINT",FACE,{"disambiguationData":[TD([[makeQuery(id+"F0.imprint","IMPRINT",EDGE,{"disambiguationData":[TD([[subQ2,-1.0]])],"derivedFrom":subQ1}),1.0]])]});}
            var Q211;
            {var subQ0=sQuery(id+"F0.wireOp",EDGE,"E23.trimOffspring");var subQ1=sQuery(id+"F0.wireOp",EDGE,"E1");var subQ2=makeQuery(id+"F0.imprint","INTERSECT",VERTEX,{"derivedFrom":[subQ1,subQ0]});Q211=makeQuery(id+"F0.imprint","IMPRINT",FACE,{"disambiguationData":[TD([[makeQuery(id+"F0.imprint","IMPRINT",EDGE,{"disambiguationData":[TD([[subQ2,-1.0]])],"derivedFrom":subQ1}),-1.0]])]});}
            var Q212;
            {var subQ0=sQuery(id+"F0.wireOp",EDGE,"E23.trimOffspring");var subQ1=sQuery(id+"F0.wireOp",EDGE,"E1");var subQ2=makeQuery(id+"F0.imprint","INTERSECT",VERTEX,{"derivedFrom":[subQ1,subQ0]});Q212=makeQuery(id+"F0.imprint","IMPRINT",FACE,{"disambiguationData":[TD([[makeQuery(id+"F0.imprint","IMPRINT",EDGE,{"disambiguationData":[TD([[subQ2,-1.0]])],"derivedFrom":subQ1}),1.0]])]});}
            var Q213;
            {var subQ0=sQuery(id+"F0.wireOp",EDGE,"E23.trimOffspring");var subQ1=sQuery(id+"F0.wireOp",EDGE,"E12.trimOffspring");var subQ2=makeQuery(id+"F0.imprint","INTERSECT",VERTEX,{"derivedFrom":[subQ1,subQ0]});Q213=makeQuery(id+"F0.imprint","IMPRINT",FACE,{"disambiguationData":[TD([[makeQuery(id+"F0.imprint","IMPRINT",EDGE,{"disambiguationData":[TD([[subQ2,-1.0]])],"derivedFrom":subQ1}),1.0]])]});}
            var Q214;
            {var subQ0=sQuery(id+"F0.wireOp",EDGE,"E23.trimOffspring");var subQ1=sQuery(id+"F0.wireOp",EDGE,"E13.trimOffspring");var subQ2=makeQuery(id+"F0.imprint","INTERSECT",VERTEX,{"derivedFrom":[subQ1,subQ0]});Q214=makeQuery(id+"F0.imprint","IMPRINT",FACE,{"disambiguationData":[TD([[makeQuery(id+"F0.imprint","IMPRINT",EDGE,{"disambiguationData":[TD([[subQ2,-1.0]])],"derivedFrom":subQ1}),1.0]])]});}
            var Q215;
            {var subQ0=sQuery(id+"F0.wireOp",EDGE,"E23.trimOffspring");var subQ1=sQuery(id+"F0.wireOp",EDGE,"E14.trimOffspring");var subQ2=makeQuery(id+"F0.imprint","INTERSECT",VERTEX,{"derivedFrom":[subQ1,subQ0]});Q215=makeQuery(id+"F0.imprint","IMPRINT",FACE,{"disambiguationData":[TD([[makeQuery(id+"F0.imprint","IMPRINT",EDGE,{"disambiguationData":[TD([[subQ2,-1.0]])],"derivedFrom":subQ1}),1.0]])]});}
            var Q216;
            {var subQ0=sQuery(id+"F0.wireOp",EDGE,"E23.trimOffspring");var subQ1=sQuery(id+"F0.wireOp",EDGE,"E15.trimOffspring");var subQ2=makeQuery(id+"F0.imprint","INTERSECT",VERTEX,{"derivedFrom":[subQ1,subQ0]});Q216=makeQuery(id+"F0.imprint","IMPRINT",FACE,{"disambiguationData":[TD([[makeQuery(id+"F0.imprint","IMPRINT",EDGE,{"disambiguationData":[TD([[subQ2,-1.0]])],"derivedFrom":subQ1}),1.0]])]});}
            var Q217;
            {var subQ0=sQuery(id+"F0.wireOp",EDGE,"E23.trimOffspring");var subQ1=sQuery(id+"F0.wireOp",EDGE,"E16.trimOffspring");var subQ2=makeQuery(id+"F0.imprint","INTERSECT",VERTEX,{"derivedFrom":[subQ1,subQ0]});Q217=makeQuery(id+"F0.imprint","IMPRINT",FACE,{"disambiguationData":[TD([[makeQuery(id+"F0.imprint","IMPRINT",EDGE,{"disambiguationData":[TD([[subQ2,-1.0]])],"derivedFrom":subQ1}),1.0]])]});}
            var Q218;
            {var subQ0=sQuery(id+"F0.wireOp",EDGE,"E23.trimOffspring");var subQ1=sQuery(id+"F0.wireOp",EDGE,"E17.trimOffspring");var subQ2=makeQuery(id+"F0.imprint","INTERSECT",VERTEX,{"derivedFrom":[subQ1,subQ0]});Q218=makeQuery(id+"F0.imprint","IMPRINT",FACE,{"disambiguationData":[TD([[makeQuery(id+"F0.imprint","IMPRINT",EDGE,{"disambiguationData":[TD([[subQ2,-1.0]])],"derivedFrom":subQ1}),1.0]])]});}
            var Q219;
            {var subQ0=sQuery(id+"F0.wireOp",EDGE,"E23.trimOffspring");var subQ1=sQuery(id+"F0.wireOp",EDGE,"E18.trimOffspring");var subQ2=makeQuery(id+"F0.imprint","INTERSECT",VERTEX,{"derivedFrom":[subQ1,subQ0]});Q219=makeQuery(id+"F0.imprint","IMPRINT",FACE,{"disambiguationData":[TD([[makeQuery(id+"F0.imprint","IMPRINT",EDGE,{"disambiguationData":[TD([[subQ2,-1.0]])],"derivedFrom":subQ1}),1.0]])]});}
            var Q220;
            {var subQ1=sQuery(id+"F0.wireOp",EDGE,"E2.0.9.0");var subQ7=sQuery(id+"F0.wireOp",EDGE,"E0.0");var subQ8=makeQuery(id+"F0.imprint","INTERSECT",VERTEX,{"derivedFrom":[subQ7,subQ1]});Q220=makeQuery(id+"F0.imprint","IMPRINT",FACE,{"disambiguationData":[TD([[makeQuery(id+"F0.imprint","IMPRINT",EDGE,{"disambiguationData":[TD([[subQ8,1.0]])],"derivedFrom":subQ7}),-1.0]])]});}
            var Q221;
            {var subQ1=sQuery(id+"F0.wireOp",EDGE,"E0.0");var subQ3=sQuery(id+"F0.wireOp",EDGE,"E2.0.9.0");var subQ4=makeQuery(id+"F0.imprint","INTERSECT",VERTEX,{"derivedFrom":[subQ1,subQ3]});Q221=makeQuery(id+"F0.imprint","IMPRINT",FACE,{"disambiguationData":[TD([[makeQuery(id+"F0.imprint","IMPRINT",EDGE,{"disambiguationData":[TD([[subQ4,-1.0]])],"derivedFrom":subQ3}),1.0]])]});}
            var Q222;
            {var subQ0=sQuery(id+"F0.wireOp",EDGE,"E22.6.0.0");var subQ5=sQuery(id+"F0.wireOp",EDGE,"E2.0.9.0");var subQ6=makeQuery(id+"F0.imprint","INTERSECT",VERTEX,{"derivedFrom":[subQ5,subQ0]});Q222=makeQuery(id+"F0.imprint","IMPRINT",FACE,{"disambiguationData":[TD([[makeQuery(id+"F0.imprint","IMPRINT",EDGE,{"disambiguationData":[TD([[subQ6,-1.0]])],"derivedFrom":subQ5}),1.0]])]});}
            var Q223;
            {var subQ0=sQuery(id+"F0.wireOp",EDGE,"E22.4.0.0");var subQ1=sQuery(id+"F0.wireOp",EDGE,"E0.1");var subQ2=makeQuery(id+"F0.imprint","INTERSECT",VERTEX,{"derivedFrom":[subQ1,subQ0]});Q223=makeQuery(id+"F0.imprint","IMPRINT",FACE,{"disambiguationData":[TD([[makeQuery(id+"F0.imprint","IMPRINT",EDGE,{"disambiguationData":[TD([[subQ2,1.0]])],"derivedFrom":subQ1}),-1.0]])]});}
            var Q224;
            {var subQ1=sQuery(id+"F0.wireOp",EDGE,"E0.2");var subQ3=sQuery(id+"F0.wireOp",EDGE,"E12.trimOffspring");var subQ4=makeQuery(id+"F0.imprint","INTERSECT",VERTEX,{"derivedFrom":[subQ1,subQ3]});Q224=makeQuery(id+"F0.imprint","IMPRINT",FACE,{"disambiguationData":[TD([[makeQuery(id+"F0.imprint","IMPRINT",EDGE,{"disambiguationData":[TD([[subQ4,1.0]])],"derivedFrom":subQ3}),-1.0]])]});}
            var Q225;
            {var subQ0=sQuery(id+"F0.wireOp",EDGE,"E15.trimOffspring");var subQ1=sQuery(id+"F0.wireOp",EDGE,"E0.2");var subQ2=makeQuery(id+"F0.imprint","INTERSECT",VERTEX,{"derivedFrom":[subQ1,subQ0]});Q225=makeQuery(id+"F0.imprint","IMPRINT",FACE,{"disambiguationData":[TD([[makeQuery(id+"F0.imprint","IMPRINT",EDGE,{"disambiguationData":[TD([[subQ2,1.0]])],"derivedFrom":subQ1}),-1.0]])]});}
            var Q226;
            {var subQ0=sQuery(id+"F0.wireOp",EDGE,"E22.8.0.0");var subQ1=sQuery(id+"F0.wireOp",EDGE,"E1");var subQ2=makeQuery(id+"F0.imprint","INTERSECT",VERTEX,{"derivedFrom":[subQ1,subQ0]});Q226=makeQuery(id+"F0.imprint","IMPRINT",FACE,{"disambiguationData":[TD([[makeQuery(id+"F0.imprint","IMPRINT",EDGE,{"disambiguationData":[TD([[subQ2,-1.0]])],"derivedFrom":subQ1}),1.0]])]});}
            var Q227;
            {var subQ0=sQuery(id+"F0.wireOp",EDGE,"E21.3.0.0");var subQ1=sQuery(id+"F0.wireOp",EDGE,"E0.4");var subQ2=makeQuery(id+"F0.imprint","INTERSECT",VERTEX,{"derivedFrom":[subQ1,subQ0]});Q227=makeQuery(id+"F0.imprint","IMPRINT",FACE,{"disambiguationData":[TD([[makeQuery(id+"F0.imprint","IMPRINT",EDGE,{"disambiguationData":[TD([[subQ2,1.0]])],"derivedFrom":subQ1}),-1.0]])]});}
            var Q228;
            {var subQ0=sQuery(id+"F0.wireOp",EDGE,"E25.trimOffspring");var subQ1=sQuery(id+"F0.wireOp",EDGE,"E13.trimOffspring");var subQ2=makeQuery(id+"F0.imprint","INTERSECT",VERTEX,{"derivedFrom":[subQ1,subQ0]});Q228=makeQuery(id+"F0.imprint","IMPRINT",FACE,{"disambiguationData":[TD([[makeQuery(id+"F0.imprint","IMPRINT",EDGE,{"disambiguationData":[TD([[subQ2,-1.0]])],"derivedFrom":subQ1}),1.0]])]});}
            var Q229;
            {var subQ0=sQuery(id+"F0.wireOp",EDGE,"E25.trimOffspring");var subQ1=sQuery(id+"F0.wireOp",EDGE,"E7.trimOffspring");var subQ2=makeQuery(id+"F0.imprint","INTERSECT",VERTEX,{"derivedFrom":[subQ1,subQ0]});Q229=makeQuery(id+"F0.imprint","IMPRINT",FACE,{"disambiguationData":[TD([[makeQuery(id+"F0.imprint","IMPRINT",EDGE,{"disambiguationData":[TD([[subQ2,-1.0]])],"derivedFrom":subQ1}),1.0]])]});}
            var Q230;
            {var subQ0=sQuery(id+"F0.wireOp",EDGE,"E21.6.0.0");var subQ1=sQuery(id+"F0.wireOp",EDGE,"E13.trimOffspring");var subQ2=makeQuery(id+"F0.imprint","INTERSECT",VERTEX,{"derivedFrom":[subQ1,subQ0]});Q230=makeQuery(id+"F0.imprint","IMPRINT",FACE,{"disambiguationData":[TD([[makeQuery(id+"F0.imprint","IMPRINT",EDGE,{"disambiguationData":[TD([[subQ2,-1.0]])],"derivedFrom":subQ1}),1.0]])]});}
            var Q231;
            {var subQ1=sQuery(id+"F0.wireOp",EDGE,"E0.3");var subQ7=sQuery(id+"F0.wireOp",EDGE,"E5.trimOffspring");var subQ8=makeQuery(id+"F0.imprint","INTERSECT",VERTEX,{"derivedFrom":[subQ1,subQ7]});Q231=makeQuery(id+"F0.imprint","IMPRINT",FACE,{"disambiguationData":[TD([[makeQuery(id+"F0.imprint","IMPRINT",EDGE,{"disambiguationData":[TD([[subQ8,1.0]])],"derivedFrom":subQ1}),-1.0]])]});}
            var Q232;
            {var subQ0=sQuery(id+"F0.wireOp",EDGE,"E21.3.0.0");var subQ1=sQuery(id+"F0.wireOp",EDGE,"E3.trimOffspring");var subQ2=makeQuery(id+"F0.imprint","INTERSECT",VERTEX,{"derivedFrom":[subQ1,subQ0]});Q232=makeQuery(id+"F0.imprint","IMPRINT",FACE,{"disambiguationData":[TD([[makeQuery(id+"F0.imprint","IMPRINT",EDGE,{"disambiguationData":[TD([[subQ2,-1.0]])],"derivedFrom":subQ1}),1.0]])]});}
            var Q233;
            {var subQ0=sQuery(id+"F0.wireOp",EDGE,"E22.8.0.0");var subQ1=sQuery(id+"F0.wireOp",EDGE,"E7.trimOffspring");var subQ2=makeQuery(id+"F0.imprint","INTERSECT",VERTEX,{"derivedFrom":[subQ1,subQ0]});Q233=makeQuery(id+"F0.imprint","IMPRINT",FACE,{"disambiguationData":[TD([[makeQuery(id+"F0.imprint","IMPRINT",EDGE,{"disambiguationData":[TD([[subQ2,-1.0]])],"derivedFrom":subQ1}),1.0]])]});}
            var Q234;
            {var subQ0=sQuery(id+"F0.wireOp",EDGE,"E20");var subQ1=sQuery(id+"F0.wireOp",EDGE,"E3.trimOffspring");var subQ2=makeQuery(id+"F0.imprint","INTERSECT",VERTEX,{"derivedFrom":[subQ1,subQ0]});Q234=makeQuery(id+"F0.imprint","IMPRINT",FACE,{"disambiguationData":[TD([[makeQuery(id+"F0.imprint","IMPRINT",EDGE,{"disambiguationData":[TD([[subQ2,-1.0]])],"derivedFrom":subQ1}),1.0]])]});}
            var Q235;
            {var subQ0=sQuery(id+"F0.wireOp",EDGE,"E26.trimOffspring");var subQ1=sQuery(id+"F0.wireOp",EDGE,"E16.trimOffspring");var subQ2=makeQuery(id+"F0.imprint","INTERSECT",VERTEX,{"derivedFrom":[subQ1,subQ0]});Q235=makeQuery(id+"F0.imprint","IMPRINT",FACE,{"disambiguationData":[TD([[makeQuery(id+"F0.imprint","IMPRINT",EDGE,{"disambiguationData":[TD([[subQ2,-1.0]])],"derivedFrom":subQ1}),1.0]])]});}
            var Q236;
            {var subQ0=sQuery(id+"F0.wireOp",EDGE,"E21.6.0.0");var subQ1=sQuery(id+"F0.wireOp",EDGE,"E1");var subQ2=makeQuery(id+"F0.imprint","INTERSECT",VERTEX,{"derivedFrom":[subQ1,subQ0]});Q236=makeQuery(id+"F0.imprint","IMPRINT",FACE,{"disambiguationData":[TD([[makeQuery(id+"F0.imprint","IMPRINT",EDGE,{"disambiguationData":[TD([[subQ2,-1.0]])],"derivedFrom":subQ1}),-1.0]])]});}
            var Q237;
            {var subQ0=sQuery(id+"F0.wireOp",EDGE,"E25.trimOffspring");var subQ1=sQuery(id+"F0.wireOp",EDGE,"E12.trimOffspring");var subQ2=makeQuery(id+"F0.imprint","INTERSECT",VERTEX,{"derivedFrom":[subQ1,subQ0]});Q237=makeQuery(id+"F0.imprint","IMPRINT",FACE,{"disambiguationData":[TD([[makeQuery(id+"F0.imprint","IMPRINT",EDGE,{"disambiguationData":[TD([[subQ2,-1.0]])],"derivedFrom":subQ1}),1.0]])]});}
            var Q238;
            {var subQ0=sQuery(id+"F0.wireOp",EDGE,"E15.trimOffspring");var subQ1=sQuery(id+"F0.wireOp",EDGE,"E0.0");var subQ2=makeQuery(id+"F0.imprint","INTERSECT",VERTEX,{"derivedFrom":[subQ1,subQ0]});Q238=makeQuery(id+"F0.imprint","IMPRINT",FACE,{"disambiguationData":[TD([[makeQuery(id+"F0.imprint","IMPRINT",EDGE,{"disambiguationData":[TD([[subQ2,-1.0]])],"derivedFrom":subQ1}),-1.0]])]});}
            var Q239;
            {var subQ0=sQuery(id+"F0.wireOp",EDGE,"E22.2.0.0");var subQ1=sQuery(id+"F0.wireOp",EDGE,"E0.4");var subQ2=makeQuery(id+"F0.imprint","INTERSECT",VERTEX,{"derivedFrom":[subQ1,subQ0]});Q239=makeQuery(id+"F0.imprint","IMPRINT",FACE,{"disambiguationData":[TD([[makeQuery(id+"F0.imprint","IMPRINT",EDGE,{"disambiguationData":[TD([[subQ2,-1.0]])],"derivedFrom":subQ1}),-1.0]])]});}
            var Q240;
            {var subQ0=sQuery(id+"F0.wireOp",EDGE,"E22.4.0.0");var subQ1=sQuery(id+"F0.wireOp",EDGE,"E3.trimOffspring");var subQ2=makeQuery(id+"F0.imprint","INTERSECT",VERTEX,{"derivedFrom":[subQ1,subQ0]});Q240=makeQuery(id+"F0.imprint","IMPRINT",FACE,{"disambiguationData":[TD([[makeQuery(id+"F0.imprint","IMPRINT",EDGE,{"disambiguationData":[TD([[subQ2,-1.0]])],"derivedFrom":subQ1}),1.0]])]});}
            var Q241;
            {var subQ0=sQuery(id+"F0.wireOp",EDGE,"E17.trimOffspring");var subQ1=sQuery(id+"F0.wireOp",EDGE,"E0.0");var subQ2=makeQuery(id+"F0.imprint","INTERSECT",VERTEX,{"derivedFrom":[subQ1,subQ0]});Q241=makeQuery(id+"F0.imprint","IMPRINT",FACE,{"disambiguationData":[TD([[makeQuery(id+"F0.imprint","IMPRINT",EDGE,{"disambiguationData":[TD([[subQ2,-1.0]])],"derivedFrom":subQ1}),-1.0]])]});}
            var Q242;
            {var subQ0=sQuery(id+"F0.wireOp",EDGE,"E22.9.0.0");var subQ1=sQuery(id+"F0.wireOp",EDGE,"E15.trimOffspring");var subQ2=makeQuery(id+"F0.imprint","INTERSECT",VERTEX,{"derivedFrom":[subQ1,subQ0]});Q242=makeQuery(id+"F0.imprint","IMPRINT",FACE,{"disambiguationData":[TD([[makeQuery(id+"F0.imprint","IMPRINT",EDGE,{"disambiguationData":[TD([[subQ2,-1.0]])],"derivedFrom":subQ1}),1.0]])]});}
            var Q243;
            {var subQ0=sQuery(id+"F0.wireOp",EDGE,"E22.9.0.0");var subQ1=sQuery(id+"F0.wireOp",EDGE,"E1");var subQ2=makeQuery(id+"F0.imprint","INTERSECT",VERTEX,{"derivedFrom":[subQ1,subQ0]});Q243=makeQuery(id+"F0.imprint","IMPRINT",FACE,{"disambiguationData":[TD([[makeQuery(id+"F0.imprint","IMPRINT",EDGE,{"disambiguationData":[TD([[subQ2,-1.0]])],"derivedFrom":subQ1}),-1.0]])]});}
            var Q244;
            {var subQ0=sQuery(id+"F0.wireOp",EDGE,"E21.6.0.0");var subQ1=sQuery(id+"F0.wireOp",EDGE,"E16.trimOffspring");var subQ2=makeQuery(id+"F0.imprint","INTERSECT",VERTEX,{"derivedFrom":[subQ1,subQ0]});Q244=makeQuery(id+"F0.imprint","IMPRINT",FACE,{"disambiguationData":[TD([[makeQuery(id+"F0.imprint","IMPRINT",EDGE,{"disambiguationData":[TD([[subQ2,-1.0]])],"derivedFrom":subQ1}),1.0]])]});}
            var Q245;
            {var subQ0=sQuery(id+"F0.wireOp",EDGE,"E25.trimOffspring");var subQ1=sQuery(id+"F0.wireOp",EDGE,"E8.trimOffspring");var subQ2=makeQuery(id+"F0.imprint","INTERSECT",VERTEX,{"derivedFrom":[subQ1,subQ0]});Q245=makeQuery(id+"F0.imprint","IMPRINT",FACE,{"disambiguationData":[TD([[makeQuery(id+"F0.imprint","IMPRINT",EDGE,{"disambiguationData":[TD([[subQ2,-1.0]])],"derivedFrom":subQ1}),1.0]])]});}
            var Q246;
            {var subQ0=sQuery(id+"F0.wireOp",EDGE,"E21.6.0.0");var subQ1=sQuery(id+"F0.wireOp",EDGE,"E5.trimOffspring");var subQ2=makeQuery(id+"F0.imprint","INTERSECT",VERTEX,{"derivedFrom":[subQ1,subQ0]});Q246=makeQuery(id+"F0.imprint","IMPRINT",FACE,{"disambiguationData":[TD([[makeQuery(id+"F0.imprint","IMPRINT",EDGE,{"disambiguationData":[TD([[subQ2,-1.0]])],"derivedFrom":subQ1}),1.0]])]});}
            var Q247;
            {var subQ0=sQuery(id+"F0.wireOp",EDGE,"E21.6.0.0");var subQ1=sQuery(id+"F0.wireOp",EDGE,"E4.trimOffspring");var subQ2=makeQuery(id+"F0.imprint","INTERSECT",VERTEX,{"derivedFrom":[subQ1,subQ0]});Q247=makeQuery(id+"F0.imprint","IMPRINT",FACE,{"disambiguationData":[TD([[makeQuery(id+"F0.imprint","IMPRINT",EDGE,{"disambiguationData":[TD([[subQ2,-1.0]])],"derivedFrom":subQ1}),1.0]])]});}
            var Q248;
            {var subQ0=sQuery(id+"F0.wireOp",EDGE,"E22.6.0.0");var subQ1=sQuery(id+"F0.wireOp",EDGE,"E3.trimOffspring");var subQ2=makeQuery(id+"F0.imprint","INTERSECT",VERTEX,{"derivedFrom":[subQ1,subQ0]});Q248=makeQuery(id+"F0.imprint","IMPRINT",FACE,{"disambiguationData":[TD([[makeQuery(id+"F0.imprint","IMPRINT",EDGE,{"disambiguationData":[TD([[subQ2,-1.0]])],"derivedFrom":subQ1}),1.0]])]});}
            var Q249;
            {var subQ0=sQuery(id+"F0.wireOp",EDGE,"E21.6.0.0");var subQ1=sQuery(id+"F0.wireOp",EDGE,"E15.trimOffspring");var subQ2=makeQuery(id+"F0.imprint","INTERSECT",VERTEX,{"derivedFrom":[subQ1,subQ0]});Q249=makeQuery(id+"F0.imprint","IMPRINT",FACE,{"disambiguationData":[TD([[makeQuery(id+"F0.imprint","IMPRINT",EDGE,{"disambiguationData":[TD([[subQ2,-1.0]])],"derivedFrom":subQ1}),1.0]])]});}
            var Q250;
            {var subQ0=sQuery(id+"F0.wireOp",EDGE,"E22.6.0.0");var subQ5=sQuery(id+"F0.wireOp",EDGE,"E3.trimOffspring");var subQ6=makeQuery(id+"F0.imprint","INTERSECT",VERTEX,{"derivedFrom":[subQ5,subQ0]});Q250=makeQuery(id+"F0.imprint","IMPRINT",FACE,{"disambiguationData":[TD([[makeQuery(id+"F0.imprint","IMPRINT",EDGE,{"disambiguationData":[TD([[subQ6,-1.0]])],"derivedFrom":subQ5}),-1.0]])]});}
            var Q251;
            {var subQ0=sQuery(id+"F0.wireOp",EDGE,"E18.trimOffspring");var subQ1=sQuery(id+"F0.wireOp",EDGE,"E0.2");var subQ2=makeQuery(id+"F0.imprint","INTERSECT",VERTEX,{"derivedFrom":[subQ1,subQ0]});Q251=makeQuery(id+"F0.imprint","IMPRINT",FACE,{"disambiguationData":[TD([[makeQuery(id+"F0.imprint","IMPRINT",EDGE,{"disambiguationData":[TD([[subQ2,1.0]])],"derivedFrom":subQ1}),-1.0]])]});}
            var Q252;
            {var subQ1=sQuery(id+"F0.wireOp",EDGE,"E0.5");var subQ3=sQuery(id+"F0.wireOp",EDGE,"E3.trimOffspring");var subQ4=makeQuery(id+"F0.imprint","INTERSECT",VERTEX,{"derivedFrom":[subQ1,subQ3]});Q252=makeQuery(id+"F0.imprint","IMPRINT",FACE,{"disambiguationData":[TD([[makeQuery(id+"F0.imprint","IMPRINT",EDGE,{"disambiguationData":[TD([[subQ4,-1.0]])],"derivedFrom":subQ3}),-1.0]])]});}
            var Q253;
            {var subQ0=sQuery(id+"F0.wireOp",EDGE,"E22.8.0.0");var subQ1=sQuery(id+"F0.wireOp",EDGE,"E10.trimOffspring");var subQ2=makeQuery(id+"F0.imprint","INTERSECT",VERTEX,{"derivedFrom":[subQ1,subQ0]});Q253=makeQuery(id+"F0.imprint","IMPRINT",FACE,{"disambiguationData":[TD([[makeQuery(id+"F0.imprint","IMPRINT",EDGE,{"disambiguationData":[TD([[subQ2,-1.0]])],"derivedFrom":subQ1}),1.0]])]});}
            var Q254;
            {var subQ0=sQuery(id+"F0.wireOp",EDGE,"E21.6.0.0");var subQ1=sQuery(id+"F0.wireOp",EDGE,"E8.trimOffspring");var subQ2=makeQuery(id+"F0.imprint","INTERSECT",VERTEX,{"derivedFrom":[subQ1,subQ0]});Q254=makeQuery(id+"F0.imprint","IMPRINT",FACE,{"disambiguationData":[TD([[makeQuery(id+"F0.imprint","IMPRINT",EDGE,{"disambiguationData":[TD([[subQ2,-1.0]])],"derivedFrom":subQ1}),1.0]])]});}
            var Q255;
            {var subQ0=sQuery(id+"F0.wireOp",EDGE,"E22.5.0.0");var subQ1=sQuery(id+"F0.wireOp",EDGE,"E3.trimOffspring");var subQ2=makeQuery(id+"F0.imprint","INTERSECT",VERTEX,{"derivedFrom":[subQ1,subQ0]});Q255=makeQuery(id+"F0.imprint","IMPRINT",FACE,{"disambiguationData":[TD([[makeQuery(id+"F0.imprint","IMPRINT",EDGE,{"disambiguationData":[TD([[subQ2,-1.0]])],"derivedFrom":subQ1}),1.0]])]});}
            var Q256;
            {var subQ0=sQuery(id+"F0.wireOp",EDGE,"E21.3.0.0");var subQ1=sQuery(id+"F0.wireOp",EDGE,"E0.1");var subQ2=makeQuery(id+"F0.imprint","INTERSECT",VERTEX,{"derivedFrom":[subQ1,subQ0]});Q256=makeQuery(id+"F0.imprint","IMPRINT",FACE,{"disambiguationData":[TD([[makeQuery(id+"F0.imprint","IMPRINT",EDGE,{"disambiguationData":[TD([[subQ2,-1.0]])],"derivedFrom":subQ1}),-1.0]])]});}
            var Q257;
            {var subQ0=sQuery(id+"F0.wireOp",EDGE,"E22.3.0.0");var subQ1=sQuery(id+"F0.wireOp",EDGE,"E0.4");var subQ2=makeQuery(id+"F0.imprint","INTERSECT",VERTEX,{"derivedFrom":[subQ1,subQ0]});Q257=makeQuery(id+"F0.imprint","IMPRINT",FACE,{"disambiguationData":[TD([[makeQuery(id+"F0.imprint","IMPRINT",EDGE,{"disambiguationData":[TD([[subQ2,-1.0]])],"derivedFrom":subQ1}),-1.0]])]});}
            var Q258;
            {var subQ0=sQuery(id+"F0.wireOp",EDGE,"E21.6.0.0");var subQ1=sQuery(id+"F0.wireOp",EDGE,"E1");var subQ2=makeQuery(id+"F0.imprint","INTERSECT",VERTEX,{"derivedFrom":[subQ1,subQ0]});Q258=makeQuery(id+"F0.imprint","IMPRINT",FACE,{"disambiguationData":[TD([[makeQuery(id+"F0.imprint","IMPRINT",EDGE,{"disambiguationData":[TD([[subQ2,-1.0]])],"derivedFrom":subQ1}),1.0]])]});}
            var Q259;
            {var subQ0=sQuery(id+"F0.wireOp",EDGE,"E13.trimOffspring");var subQ1=sQuery(id+"F0.wireOp",EDGE,"E0.2");var subQ2=makeQuery(id+"F0.imprint","INTERSECT",VERTEX,{"derivedFrom":[subQ1,subQ0]});Q259=makeQuery(id+"F0.imprint","IMPRINT",FACE,{"disambiguationData":[TD([[makeQuery(id+"F0.imprint","IMPRINT",EDGE,{"disambiguationData":[TD([[subQ2,1.0]])],"derivedFrom":subQ1}),-1.0]])]});}
            var Q260;
            {var subQ0=sQuery(id+"F0.wireOp",EDGE,"E22.8.0.0");var subQ1=sQuery(id+"F0.wireOp",EDGE,"E1");var subQ2=makeQuery(id+"F0.imprint","INTERSECT",VERTEX,{"derivedFrom":[subQ1,subQ0]});Q260=makeQuery(id+"F0.imprint","IMPRINT",FACE,{"disambiguationData":[TD([[makeQuery(id+"F0.imprint","IMPRINT",EDGE,{"disambiguationData":[TD([[subQ2,-1.0]])],"derivedFrom":subQ1}),-1.0]])]});}
            var Q261;
            {var subQ0=sQuery(id+"F0.wireOp",EDGE,"E22.9.0.0");var subQ1=sQuery(id+"F0.wireOp",EDGE,"E9.trimOffspring");var subQ2=makeQuery(id+"F0.imprint","INTERSECT",VERTEX,{"derivedFrom":[subQ1,subQ0]});Q261=makeQuery(id+"F0.imprint","IMPRINT",FACE,{"disambiguationData":[TD([[makeQuery(id+"F0.imprint","IMPRINT",EDGE,{"disambiguationData":[TD([[subQ2,-1.0]])],"derivedFrom":subQ1}),1.0]])]});}
            var Q262;
            {var subQ0=sQuery(id+"F0.wireOp",EDGE,"E21.1.0.0");var subQ1=sQuery(id+"F0.wireOp",EDGE,"E3.trimOffspring");var subQ2=makeQuery(id+"F0.imprint","INTERSECT",VERTEX,{"derivedFrom":[subQ1,subQ0]});Q262=makeQuery(id+"F0.imprint","IMPRINT",FACE,{"disambiguationData":[TD([[makeQuery(id+"F0.imprint","IMPRINT",EDGE,{"disambiguationData":[TD([[subQ2,-1.0]])],"derivedFrom":subQ1}),1.0]])]});}
            var Q263;
            {var subQ3=sQuery(id+"F0.wireOp",EDGE,"E21.5.0.0");var subQ5=sQuery(id+"F0.wireOp",EDGE,"E2.0.9.0");var subQ6=makeQuery(id+"F0.imprint","INTERSECT",VERTEX,{"derivedFrom":[subQ5,subQ3]});Q263=makeQuery(id+"F0.imprint","IMPRINT",FACE,{"disambiguationData":[TD([[makeQuery(id+"F0.imprint","IMPRINT",EDGE,{"disambiguationData":[TD([[subQ6,-1.0]])],"derivedFrom":subQ5}),1.0]])]});}
            var Q264;
            {var subQ0=sQuery(id+"F0.wireOp",EDGE,"E22.9.0.0");var subQ1=sQuery(id+"F0.wireOp",EDGE,"E12.trimOffspring");var subQ2=makeQuery(id+"F0.imprint","INTERSECT",VERTEX,{"derivedFrom":[subQ1,subQ0]});Q264=makeQuery(id+"F0.imprint","IMPRINT",FACE,{"disambiguationData":[TD([[makeQuery(id+"F0.imprint","IMPRINT",EDGE,{"disambiguationData":[TD([[subQ2,-1.0]])],"derivedFrom":subQ1}),1.0]])]});}
            var Q265;
            {var subQ0=sQuery(id+"F0.wireOp",EDGE,"E26.trimOffspring");var subQ1=sQuery(id+"F0.wireOp",EDGE,"E15.trimOffspring");var subQ2=makeQuery(id+"F0.imprint","INTERSECT",VERTEX,{"derivedFrom":[subQ1,subQ0]});Q265=makeQuery(id+"F0.imprint","IMPRINT",FACE,{"disambiguationData":[TD([[makeQuery(id+"F0.imprint","IMPRINT",EDGE,{"disambiguationData":[TD([[subQ2,-1.0]])],"derivedFrom":subQ1}),1.0]])]});}
            var Q266;
            {var subQ0=sQuery(id+"F0.wireOp",EDGE,"E8.trimOffspring");var subQ1=sQuery(id+"F0.wireOp",EDGE,"E0.3");var subQ2=makeQuery(id+"F0.imprint","INTERSECT",VERTEX,{"derivedFrom":[subQ1,subQ0]});Q266=makeQuery(id+"F0.imprint","IMPRINT",FACE,{"disambiguationData":[TD([[makeQuery(id+"F0.imprint","IMPRINT",EDGE,{"disambiguationData":[TD([[subQ2,1.0]])],"derivedFrom":subQ1}),-1.0]])]});}
            var Q267;
            {var subQ0=sQuery(id+"F0.wireOp",EDGE,"E9.trimOffspring");var subQ1=sQuery(id+"F0.wireOp",EDGE,"E0.5");var subQ2=makeQuery(id+"F0.imprint","INTERSECT",VERTEX,{"derivedFrom":[subQ1,subQ0]});Q267=makeQuery(id+"F0.imprint","IMPRINT",FACE,{"disambiguationData":[TD([[makeQuery(id+"F0.imprint","IMPRINT",EDGE,{"disambiguationData":[TD([[subQ2,-1.0]])],"derivedFrom":subQ1}),-1.0]])]});}
            var Q268;
            {var subQ0=sQuery(id+"F0.wireOp",EDGE,"E22.9.0.0");var subQ1=sQuery(id+"F0.wireOp",EDGE,"E7.trimOffspring");var subQ2=makeQuery(id+"F0.imprint","INTERSECT",VERTEX,{"derivedFrom":[subQ1,subQ0]});Q268=makeQuery(id+"F0.imprint","IMPRINT",FACE,{"disambiguationData":[TD([[makeQuery(id+"F0.imprint","IMPRINT",EDGE,{"disambiguationData":[TD([[subQ2,-1.0]])],"derivedFrom":subQ1}),1.0]])]});}
            var Q269;
            {var subQ0=sQuery(id+"F0.wireOp",EDGE,"E25.trimOffspring");var subQ1=sQuery(id+"F0.wireOp",EDGE,"E10.trimOffspring");var subQ2=makeQuery(id+"F0.imprint","INTERSECT",VERTEX,{"derivedFrom":[subQ1,subQ0]});Q269=makeQuery(id+"F0.imprint","IMPRINT",FACE,{"disambiguationData":[TD([[makeQuery(id+"F0.imprint","IMPRINT",EDGE,{"disambiguationData":[TD([[subQ2,-1.0]])],"derivedFrom":subQ1}),1.0]])]});}
            var Q270;
            {var subQ0=sQuery(id+"F0.wireOp",EDGE,"E17.trimOffspring");var subQ1=sQuery(id+"F0.wireOp",EDGE,"E0.2");var subQ2=makeQuery(id+"F0.imprint","INTERSECT",VERTEX,{"derivedFrom":[subQ1,subQ0]});Q270=makeQuery(id+"F0.imprint","IMPRINT",FACE,{"disambiguationData":[TD([[makeQuery(id+"F0.imprint","IMPRINT",EDGE,{"disambiguationData":[TD([[subQ2,1.0]])],"derivedFrom":subQ1}),-1.0]])]});}
            var Q271;
            {var subQ0=sQuery(id+"F0.wireOp",EDGE,"E21.6.0.0");var subQ1=sQuery(id+"F0.wireOp",EDGE,"E14.trimOffspring");var subQ2=makeQuery(id+"F0.imprint","INTERSECT",VERTEX,{"derivedFrom":[subQ1,subQ0]});Q271=makeQuery(id+"F0.imprint","IMPRINT",FACE,{"disambiguationData":[TD([[makeQuery(id+"F0.imprint","IMPRINT",EDGE,{"disambiguationData":[TD([[subQ2,-1.0]])],"derivedFrom":subQ1}),1.0]])]});}
            var Q272;
            {var subQ0=sQuery(id+"F0.wireOp",EDGE,"E22.8.0.0");var subQ1=sQuery(id+"F0.wireOp",EDGE,"E16.trimOffspring");var subQ2=makeQuery(id+"F0.imprint","INTERSECT",VERTEX,{"derivedFrom":[subQ1,subQ0]});Q272=makeQuery(id+"F0.imprint","IMPRINT",FACE,{"disambiguationData":[TD([[makeQuery(id+"F0.imprint","IMPRINT",EDGE,{"disambiguationData":[TD([[subQ2,-1.0]])],"derivedFrom":subQ1}),1.0]])]});}
            var Q273;
            {var subQ1=sQuery(id+"F0.wireOp",EDGE,"E0.0");var subQ5=sQuery(id+"F0.wireOp",EDGE,"E18.trimOffspring");var subQ6=makeQuery(id+"F0.imprint","INTERSECT",VERTEX,{"derivedFrom":[subQ1,subQ5]});Q273=makeQuery(id+"F0.imprint","IMPRINT",FACE,{"disambiguationData":[TD([[makeQuery(id+"F0.imprint","IMPRINT",EDGE,{"disambiguationData":[TD([[subQ6,1.0]])],"derivedFrom":subQ1}),-1.0]])]});}
            var Q274;
            {var subQ5=sQuery(id+"F0.wireOp",EDGE,"E6.trimOffspring");var subQ7=sQuery(id+"F0.wireOp",EDGE,"E0.5");var subQ8=makeQuery(id+"F0.imprint","INTERSECT",VERTEX,{"derivedFrom":[subQ7,subQ5]});Q274=makeQuery(id+"F0.imprint","IMPRINT",FACE,{"disambiguationData":[TD([[makeQuery(id+"F0.imprint","IMPRINT",EDGE,{"disambiguationData":[TD([[subQ8,-1.0]])],"derivedFrom":subQ7}),-1.0]])]});}
            var Q275;
            {var subQ0=sQuery(id+"F0.wireOp",EDGE,"E20");var subQ1=sQuery(id+"F0.wireOp",EDGE,"E0.4");var subQ2=makeQuery(id+"F0.imprint","INTERSECT",VERTEX,{"derivedFrom":[subQ1,subQ0]});Q275=makeQuery(id+"F0.imprint","IMPRINT",FACE,{"disambiguationData":[TD([[makeQuery(id+"F0.imprint","IMPRINT",EDGE,{"disambiguationData":[TD([[subQ2,1.0]])],"derivedFrom":subQ1}),-1.0]])]});}
            var Q276;
            {var subQ0=sQuery(id+"F0.wireOp",EDGE,"E22.9.0.0");var subQ1=sQuery(id+"F0.wireOp",EDGE,"E13.trimOffspring");var subQ2=makeQuery(id+"F0.imprint","INTERSECT",VERTEX,{"derivedFrom":[subQ1,subQ0]});Q276=makeQuery(id+"F0.imprint","IMPRINT",FACE,{"disambiguationData":[TD([[makeQuery(id+"F0.imprint","IMPRINT",EDGE,{"disambiguationData":[TD([[subQ2,-1.0]])],"derivedFrom":subQ1}),1.0]])]});}
            var Q277;
            {var subQ0=sQuery(id+"F0.wireOp",EDGE,"E22.9.0.0");var subQ1=sQuery(id+"F0.wireOp",EDGE,"E14.trimOffspring");var subQ2=makeQuery(id+"F0.imprint","INTERSECT",VERTEX,{"derivedFrom":[subQ1,subQ0]});Q277=makeQuery(id+"F0.imprint","IMPRINT",FACE,{"disambiguationData":[TD([[makeQuery(id+"F0.imprint","IMPRINT",EDGE,{"disambiguationData":[TD([[subQ2,-1.0]])],"derivedFrom":subQ1}),1.0]])]});}
            var Q278;
            {var subQ0=sQuery(id+"F0.wireOp",EDGE,"E26.trimOffspring");var subQ1=sQuery(id+"F0.wireOp",EDGE,"E12.trimOffspring");var subQ2=makeQuery(id+"F0.imprint","INTERSECT",VERTEX,{"derivedFrom":[subQ1,subQ0]});Q278=makeQuery(id+"F0.imprint","IMPRINT",FACE,{"disambiguationData":[TD([[makeQuery(id+"F0.imprint","IMPRINT",EDGE,{"disambiguationData":[TD([[subQ2,-1.0]])],"derivedFrom":subQ1}),1.0]])]});}
            var Q279;
            {var subQ0=sQuery(id+"F0.wireOp",EDGE,"E26.trimOffspring");var subQ1=sQuery(id+"F0.wireOp",EDGE,"E10.trimOffspring");var subQ2=makeQuery(id+"F0.imprint","INTERSECT",VERTEX,{"derivedFrom":[subQ1,subQ0]});Q279=makeQuery(id+"F0.imprint","IMPRINT",FACE,{"disambiguationData":[TD([[makeQuery(id+"F0.imprint","IMPRINT",EDGE,{"disambiguationData":[TD([[subQ2,-1.0]])],"derivedFrom":subQ1}),1.0]])]});}
            var Q280;
            {var subQ0=sQuery(id+"F0.wireOp",EDGE,"E22.8.0.0");var subQ1=sQuery(id+"F0.wireOp",EDGE,"E9.trimOffspring");var subQ2=makeQuery(id+"F0.imprint","INTERSECT",VERTEX,{"derivedFrom":[subQ1,subQ0]});Q280=makeQuery(id+"F0.imprint","IMPRINT",FACE,{"disambiguationData":[TD([[makeQuery(id+"F0.imprint","IMPRINT",EDGE,{"disambiguationData":[TD([[subQ2,-1.0]])],"derivedFrom":subQ1}),1.0]])]});}
            var Q281;
            {var subQ0=sQuery(id+"F0.wireOp",EDGE,"E21.6.0.0");var subQ1=sQuery(id+"F0.wireOp",EDGE,"E10.trimOffspring");var subQ2=makeQuery(id+"F0.imprint","INTERSECT",VERTEX,{"derivedFrom":[subQ1,subQ0]});Q281=makeQuery(id+"F0.imprint","IMPRINT",FACE,{"disambiguationData":[TD([[makeQuery(id+"F0.imprint","IMPRINT",EDGE,{"disambiguationData":[TD([[subQ2,-1.0]])],"derivedFrom":subQ1}),1.0]])]});}
            var Q282;
            {var subQ0=sQuery(id+"F0.wireOp",EDGE,"E14.trimOffspring");var subQ1=sQuery(id+"F0.wireOp",EDGE,"E0.0");var subQ2=makeQuery(id+"F0.imprint","INTERSECT",VERTEX,{"derivedFrom":[subQ1,subQ0]});Q282=makeQuery(id+"F0.imprint","IMPRINT",FACE,{"disambiguationData":[TD([[makeQuery(id+"F0.imprint","IMPRINT",EDGE,{"disambiguationData":[TD([[subQ2,-1.0]])],"derivedFrom":subQ1}),-1.0]])]});}
            var Q283;
            {var subQ0=sQuery(id+"F0.wireOp",EDGE,"E26.trimOffspring");var subQ1=sQuery(id+"F0.wireOp",EDGE,"E6.trimOffspring");var subQ2=makeQuery(id+"F0.imprint","INTERSECT",VERTEX,{"derivedFrom":[subQ1,subQ0]});Q283=makeQuery(id+"F0.imprint","IMPRINT",FACE,{"disambiguationData":[TD([[makeQuery(id+"F0.imprint","IMPRINT",EDGE,{"disambiguationData":[TD([[subQ2,-1.0]])],"derivedFrom":subQ1}),1.0]])]});}
            var Q284;
            {var subQ0=sQuery(id+"F0.wireOp",EDGE,"E22.8.0.0");var subQ1=sQuery(id+"F0.wireOp",EDGE,"E8.trimOffspring");var subQ2=makeQuery(id+"F0.imprint","INTERSECT",VERTEX,{"derivedFrom":[subQ1,subQ0]});Q284=makeQuery(id+"F0.imprint","IMPRINT",FACE,{"disambiguationData":[TD([[makeQuery(id+"F0.imprint","IMPRINT",EDGE,{"disambiguationData":[TD([[subQ2,-1.0]])],"derivedFrom":subQ1}),1.0]])]});}
            var Q285;
            {var subQ0=sQuery(id+"F0.wireOp",EDGE,"E21.1.0.0");var subQ1=sQuery(id+"F0.wireOp",EDGE,"E0.4");var subQ2=makeQuery(id+"F0.imprint","INTERSECT",VERTEX,{"derivedFrom":[subQ1,subQ0]});Q285=makeQuery(id+"F0.imprint","IMPRINT",FACE,{"disambiguationData":[TD([[makeQuery(id+"F0.imprint","IMPRINT",EDGE,{"disambiguationData":[TD([[subQ2,1.0]])],"derivedFrom":subQ1}),-1.0]])]});}
            var Q286;
            {var subQ0=sQuery(id+"F0.wireOp",EDGE,"E17.trimOffspring");var subQ1=sQuery(id+"F0.wireOp",EDGE,"E0.0");var subQ2=makeQuery(id+"F0.imprint","INTERSECT",VERTEX,{"derivedFrom":[subQ1,subQ0]});Q286=makeQuery(id+"F0.imprint","IMPRINT",FACE,{"disambiguationData":[TD([[makeQuery(id+"F0.imprint","IMPRINT",EDGE,{"disambiguationData":[TD([[subQ2,1.0]])],"derivedFrom":subQ1}),-1.0]])]});}
            var Q287;
            {var subQ1=sQuery(id+"F0.wireOp",EDGE,"E3.trimOffspring");var subQ5=sQuery(id+"F0.wireOp",EDGE,"E0.5");var subQ6=makeQuery(id+"F0.imprint","INTERSECT",VERTEX,{"derivedFrom":[subQ5,subQ1]});Q287=makeQuery(id+"F0.imprint","IMPRINT",FACE,{"disambiguationData":[TD([[makeQuery(id+"F0.imprint","IMPRINT",EDGE,{"disambiguationData":[TD([[subQ6,-1.0]])],"derivedFrom":subQ5}),-1.0]])]});}
            var Q288;
            {var subQ0=sQuery(id+"F0.wireOp",EDGE,"E10.trimOffspring");var subQ1=sQuery(id+"F0.wireOp",EDGE,"E0.3");var subQ2=makeQuery(id+"F0.imprint","INTERSECT",VERTEX,{"derivedFrom":[subQ1,subQ0]});Q288=makeQuery(id+"F0.imprint","IMPRINT",FACE,{"disambiguationData":[TD([[makeQuery(id+"F0.imprint","IMPRINT",EDGE,{"disambiguationData":[TD([[subQ2,1.0]])],"derivedFrom":subQ1}),-1.0]])]});}
            var Q289;
            {var subQ1=sQuery(id+"F0.wireOp",EDGE,"E0.2");var subQ7=sQuery(id+"F0.wireOp",EDGE,"E17.trimOffspring");var subQ8=makeQuery(id+"F0.imprint","INTERSECT",VERTEX,{"derivedFrom":[subQ1,subQ7]});Q289=makeQuery(id+"F0.imprint","IMPRINT",FACE,{"disambiguationData":[TD([[makeQuery(id+"F0.imprint","IMPRINT",EDGE,{"disambiguationData":[TD([[subQ8,-1.0]])],"derivedFrom":subQ1}),-1.0]])]});}
            var Q290;
            {var subQ0=sQuery(id+"F0.wireOp",EDGE,"E22.3.0.0");var subQ1=sQuery(id+"F0.wireOp",EDGE,"E0.1");var subQ2=makeQuery(id+"F0.imprint","INTERSECT",VERTEX,{"derivedFrom":[subQ1,subQ0]});Q290=makeQuery(id+"F0.imprint","IMPRINT",FACE,{"disambiguationData":[TD([[makeQuery(id+"F0.imprint","IMPRINT",EDGE,{"disambiguationData":[TD([[subQ2,1.0]])],"derivedFrom":subQ1}),-1.0]])]});}
            var Q291;
            {var subQ0=sQuery(id+"F0.wireOp",EDGE,"E21.6.0.0");var subQ1=sQuery(id+"F0.wireOp",EDGE,"E9.trimOffspring");var subQ2=makeQuery(id+"F0.imprint","INTERSECT",VERTEX,{"derivedFrom":[subQ1,subQ0]});Q291=makeQuery(id+"F0.imprint","IMPRINT",FACE,{"disambiguationData":[TD([[makeQuery(id+"F0.imprint","IMPRINT",EDGE,{"disambiguationData":[TD([[subQ2,-1.0]])],"derivedFrom":subQ1}),1.0]])]});}
            var Q292;
            {var subQ0=sQuery(id+"F0.wireOp",EDGE,"E9.trimOffspring");var subQ1=sQuery(id+"F0.wireOp",EDGE,"E0.3");var subQ2=makeQuery(id+"F0.imprint","INTERSECT",VERTEX,{"derivedFrom":[subQ1,subQ0]});Q292=makeQuery(id+"F0.imprint","IMPRINT",FACE,{"disambiguationData":[TD([[makeQuery(id+"F0.imprint","IMPRINT",EDGE,{"disambiguationData":[TD([[subQ2,1.0]])],"derivedFrom":subQ1}),-1.0]])]});}
            var Q293;
            {var subQ0=sQuery(id+"F0.wireOp",EDGE,"E21.6.0.0");var subQ1=sQuery(id+"F0.wireOp",EDGE,"E17.trimOffspring");var subQ2=makeQuery(id+"F0.imprint","INTERSECT",VERTEX,{"derivedFrom":[subQ1,subQ0]});Q293=makeQuery(id+"F0.imprint","IMPRINT",FACE,{"disambiguationData":[TD([[makeQuery(id+"F0.imprint","IMPRINT",EDGE,{"disambiguationData":[TD([[subQ2,-1.0]])],"derivedFrom":subQ1}),1.0]])]});}
            var Q294;
            {var subQ0=sQuery(id+"F0.wireOp",EDGE,"E7.trimOffspring");var subQ1=sQuery(id+"F0.wireOp",EDGE,"E0.3");var subQ2=makeQuery(id+"F0.imprint","INTERSECT",VERTEX,{"derivedFrom":[subQ1,subQ0]});Q294=makeQuery(id+"F0.imprint","IMPRINT",FACE,{"disambiguationData":[TD([[makeQuery(id+"F0.imprint","IMPRINT",EDGE,{"disambiguationData":[TD([[subQ2,1.0]])],"derivedFrom":subQ1}),-1.0]])]});}
            var Q295;
            {var subQ0=sQuery(id+"F0.wireOp",EDGE,"E6.trimOffspring");var subQ1=sQuery(id+"F0.wireOp",EDGE,"E0.3");var subQ2=makeQuery(id+"F0.imprint","INTERSECT",VERTEX,{"derivedFrom":[subQ1,subQ0]});Q295=makeQuery(id+"F0.imprint","IMPRINT",FACE,{"disambiguationData":[TD([[makeQuery(id+"F0.imprint","IMPRINT",EDGE,{"disambiguationData":[TD([[subQ2,-1.0]])],"derivedFrom":subQ1}),-1.0]])]});}
            var Q296;
            {var subQ0=sQuery(id+"F0.wireOp",EDGE,"E14.trimOffspring");var subQ1=sQuery(id+"F0.wireOp",EDGE,"E0.2");var subQ2=makeQuery(id+"F0.imprint","INTERSECT",VERTEX,{"derivedFrom":[subQ1,subQ0]});Q296=makeQuery(id+"F0.imprint","IMPRINT",FACE,{"disambiguationData":[TD([[makeQuery(id+"F0.imprint","IMPRINT",EDGE,{"disambiguationData":[TD([[subQ2,1.0]])],"derivedFrom":subQ1}),-1.0]])]});}
            var Q297;
            {var subQ0=sQuery(id+"F0.wireOp",EDGE,"E4.trimOffspring");var subQ1=sQuery(id+"F0.wireOp",EDGE,"E0.5");var subQ2=makeQuery(id+"F0.imprint","INTERSECT",VERTEX,{"derivedFrom":[subQ1,subQ0]});Q297=makeQuery(id+"F0.imprint","IMPRINT",FACE,{"disambiguationData":[TD([[makeQuery(id+"F0.imprint","IMPRINT",EDGE,{"disambiguationData":[TD([[subQ2,-1.0]])],"derivedFrom":subQ1}),-1.0]])]});}
            var Q298;
            {var subQ0=sQuery(id+"F0.wireOp",EDGE,"E26.trimOffspring");var subQ1=sQuery(id+"F0.wireOp",EDGE,"E1");var subQ2=makeQuery(id+"F0.imprint","INTERSECT",VERTEX,{"derivedFrom":[subQ1,subQ0]});Q298=makeQuery(id+"F0.imprint","IMPRINT",FACE,{"disambiguationData":[TD([[makeQuery(id+"F0.imprint","IMPRINT",EDGE,{"disambiguationData":[TD([[subQ2,-1.0]])],"derivedFrom":subQ1}),1.0]])]});}
            var Q299;
            {var subQ0=sQuery(id+"F0.wireOp",EDGE,"E21.6.0.0");var subQ1=sQuery(id+"F0.wireOp",EDGE,"E7.trimOffspring");var subQ2=makeQuery(id+"F0.imprint","INTERSECT",VERTEX,{"derivedFrom":[subQ1,subQ0]});Q299=makeQuery(id+"F0.imprint","IMPRINT",FACE,{"disambiguationData":[TD([[makeQuery(id+"F0.imprint","IMPRINT",EDGE,{"disambiguationData":[TD([[subQ2,-1.0]])],"derivedFrom":subQ1}),1.0]])]});}
            var Q300;
            {var subQ1=sQuery(id+"F0.wireOp",EDGE,"E0.2");var subQ3=sQuery(id+"F0.wireOp",EDGE,"E2.0.9.0");var subQ4=makeQuery(id+"F0.imprint","INTERSECT",VERTEX,{"derivedFrom":[subQ1,subQ3]});Q300=makeQuery(id+"F0.imprint","IMPRINT",FACE,{"disambiguationData":[TD([[makeQuery(id+"F0.imprint","IMPRINT",EDGE,{"disambiguationData":[TD([[subQ4,1.0]])],"derivedFrom":subQ3}),1.0]])]});}
            var Q301;
            {var subQ0=sQuery(id+"F0.wireOp",EDGE,"E21.2.0.0");var subQ1=sQuery(id+"F0.wireOp",EDGE,"E3.trimOffspring");var subQ2=makeQuery(id+"F0.imprint","INTERSECT",VERTEX,{"derivedFrom":[subQ1,subQ0]});Q301=makeQuery(id+"F0.imprint","IMPRINT",FACE,{"disambiguationData":[TD([[makeQuery(id+"F0.imprint","IMPRINT",EDGE,{"disambiguationData":[TD([[subQ2,-1.0]])],"derivedFrom":subQ1}),1.0]])]});}
            var Q302;
            {var subQ0=sQuery(id+"F0.wireOp",EDGE,"E22.1.0.0");var subQ1=sQuery(id+"F0.wireOp",EDGE,"E0.1");var subQ2=makeQuery(id+"F0.imprint","INTERSECT",VERTEX,{"derivedFrom":[subQ1,subQ0]});Q302=makeQuery(id+"F0.imprint","IMPRINT",FACE,{"disambiguationData":[TD([[makeQuery(id+"F0.imprint","IMPRINT",EDGE,{"disambiguationData":[TD([[subQ2,1.0]])],"derivedFrom":subQ1}),-1.0]])]});}
            var Q303;
            {var subQ0=sQuery(id+"F0.wireOp",EDGE,"E22.1.0.0");var subQ1=sQuery(id+"F0.wireOp",EDGE,"E0.4");var subQ2=makeQuery(id+"F0.imprint","INTERSECT",VERTEX,{"derivedFrom":[subQ1,subQ0]});Q303=makeQuery(id+"F0.imprint","IMPRINT",FACE,{"disambiguationData":[TD([[makeQuery(id+"F0.imprint","IMPRINT",EDGE,{"disambiguationData":[TD([[subQ2,-1.0]])],"derivedFrom":subQ1}),-1.0]])]});}
            var Q304;
            {var subQ0=sQuery(id+"F0.wireOp",EDGE,"E6.trimOffspring");var subQ1=sQuery(id+"F0.wireOp",EDGE,"E0.5");var subQ2=makeQuery(id+"F0.imprint","INTERSECT",VERTEX,{"derivedFrom":[subQ1,subQ0]});Q304=makeQuery(id+"F0.imprint","IMPRINT",FACE,{"disambiguationData":[TD([[makeQuery(id+"F0.imprint","IMPRINT",EDGE,{"disambiguationData":[TD([[subQ2,1.0]])],"derivedFrom":subQ1}),-1.0]])]});}
            var Q305;
            {var subQ0=sQuery(id+"F0.wireOp",EDGE,"E19.trimOffspring");var subQ1=sQuery(id+"F0.wireOp",EDGE,"E0.2");var subQ2=makeQuery(id+"F0.imprint","INTERSECT",VERTEX,{"derivedFrom":[subQ1,subQ0]});Q305=makeQuery(id+"F0.imprint","IMPRINT",FACE,{"disambiguationData":[TD([[makeQuery(id+"F0.imprint","IMPRINT",EDGE,{"disambiguationData":[TD([[subQ2,1.0]])],"derivedFrom":subQ1}),-1.0]])]});}
            var Q306;
            {var subQ0=sQuery(id+"F0.wireOp",EDGE,"E20");var subQ1=sQuery(id+"F0.wireOp",EDGE,"E0.1");var subQ2=makeQuery(id+"F0.imprint","INTERSECT",VERTEX,{"derivedFrom":[subQ1,subQ0]});Q306=makeQuery(id+"F0.imprint","IMPRINT",FACE,{"disambiguationData":[TD([[makeQuery(id+"F0.imprint","IMPRINT",EDGE,{"disambiguationData":[TD([[subQ2,-1.0]])],"derivedFrom":subQ1}),-1.0]])]});}
            var Q307;
            {var subQ0=sQuery(id+"F0.wireOp",EDGE,"E26.trimOffspring");var subQ1=sQuery(id+"F0.wireOp",EDGE,"E13.trimOffspring");var subQ2=makeQuery(id+"F0.imprint","INTERSECT",VERTEX,{"derivedFrom":[subQ1,subQ0]});Q307=makeQuery(id+"F0.imprint","IMPRINT",FACE,{"disambiguationData":[TD([[makeQuery(id+"F0.imprint","IMPRINT",EDGE,{"disambiguationData":[TD([[subQ2,-1.0]])],"derivedFrom":subQ1}),1.0]])]});}
            var Q308;
            {var subQ0=sQuery(id+"F0.wireOp",EDGE,"E21.4.0.0");var subQ1=sQuery(id+"F0.wireOp",EDGE,"E0.4");var subQ2=makeQuery(id+"F0.imprint","INTERSECT",VERTEX,{"derivedFrom":[subQ1,subQ0]});Q308=makeQuery(id+"F0.imprint","IMPRINT",FACE,{"disambiguationData":[TD([[makeQuery(id+"F0.imprint","IMPRINT",EDGE,{"disambiguationData":[TD([[subQ2,1.0]])],"derivedFrom":subQ1}),-1.0]])]});}
            var Q309;
            {var subQ0=sQuery(id+"F0.wireOp",EDGE,"E25.trimOffspring");var subQ1=sQuery(id+"F0.wireOp",EDGE,"E1");var subQ2=makeQuery(id+"F0.imprint","INTERSECT",VERTEX,{"derivedFrom":[subQ1,subQ0]});Q309=makeQuery(id+"F0.imprint","IMPRINT",FACE,{"disambiguationData":[TD([[makeQuery(id+"F0.imprint","IMPRINT",EDGE,{"disambiguationData":[TD([[subQ2,-1.0]])],"derivedFrom":subQ1}),-1.0]])]});}
            var Q310;
            {var subQ0=sQuery(id+"F0.wireOp",EDGE,"E22.8.0.0");var subQ1=sQuery(id+"F0.wireOp",EDGE,"E12.trimOffspring");var subQ2=makeQuery(id+"F0.imprint","INTERSECT",VERTEX,{"derivedFrom":[subQ1,subQ0]});Q310=makeQuery(id+"F0.imprint","IMPRINT",FACE,{"disambiguationData":[TD([[makeQuery(id+"F0.imprint","IMPRINT",EDGE,{"disambiguationData":[TD([[subQ2,-1.0]])],"derivedFrom":subQ1}),1.0]])]});}
            var Q311;
            {var subQ0=sQuery(id+"F0.wireOp",EDGE,"E21.6.0.0");var subQ1=sQuery(id+"F0.wireOp",EDGE,"E18.trimOffspring");var subQ2=makeQuery(id+"F0.imprint","INTERSECT",VERTEX,{"derivedFrom":[subQ1,subQ0]});Q311=makeQuery(id+"F0.imprint","IMPRINT",FACE,{"disambiguationData":[TD([[makeQuery(id+"F0.imprint","IMPRINT",EDGE,{"disambiguationData":[TD([[subQ2,-1.0]])],"derivedFrom":subQ1}),1.0]])]});}
            var Q312;
            {var subQ0=sQuery(id+"F0.wireOp",EDGE,"E22.8.0.0");var subQ1=sQuery(id+"F0.wireOp",EDGE,"E6.trimOffspring");var subQ2=makeQuery(id+"F0.imprint","INTERSECT",VERTEX,{"derivedFrom":[subQ1,subQ0]});Q312=makeQuery(id+"F0.imprint","IMPRINT",FACE,{"disambiguationData":[TD([[makeQuery(id+"F0.imprint","IMPRINT",EDGE,{"disambiguationData":[TD([[subQ2,-1.0]])],"derivedFrom":subQ1}),1.0]])]});}
            var Q313;
            {var subQ0=sQuery(id+"F0.wireOp",EDGE,"E18.trimOffspring");var subQ1=sQuery(id+"F0.wireOp",EDGE,"E0.2");var subQ2=makeQuery(id+"F0.imprint","INTERSECT",VERTEX,{"derivedFrom":[subQ1,subQ0]});Q313=makeQuery(id+"F0.imprint","IMPRINT",FACE,{"disambiguationData":[TD([[makeQuery(id+"F0.imprint","IMPRINT",EDGE,{"disambiguationData":[TD([[subQ2,-1.0]])],"derivedFrom":subQ1}),-1.0]])]});}
            var Q314;
            {var subQ0=sQuery(id+"F0.wireOp",EDGE,"E22.2.0.0");var subQ1=sQuery(id+"F0.wireOp",EDGE,"E3.trimOffspring");var subQ2=makeQuery(id+"F0.imprint","INTERSECT",VERTEX,{"derivedFrom":[subQ1,subQ0]});Q314=makeQuery(id+"F0.imprint","IMPRINT",FACE,{"disambiguationData":[TD([[makeQuery(id+"F0.imprint","IMPRINT",EDGE,{"disambiguationData":[TD([[subQ2,-1.0]])],"derivedFrom":subQ1}),1.0]])]});}
            var Q315;
            {var subQ0=sQuery(id+"F0.wireOp",EDGE,"E5.trimOffspring");var subQ1=sQuery(id+"F0.wireOp",EDGE,"E0.5");var subQ2=makeQuery(id+"F0.imprint","INTERSECT",VERTEX,{"derivedFrom":[subQ1,subQ0]});Q315=makeQuery(id+"F0.imprint","IMPRINT",FACE,{"disambiguationData":[TD([[makeQuery(id+"F0.imprint","IMPRINT",EDGE,{"disambiguationData":[TD([[subQ2,-1.0]])],"derivedFrom":subQ1}),-1.0]])]});}
            var Q316;
            {var subQ0=sQuery(id+"F0.wireOp",EDGE,"E26.trimOffspring");var subQ1=sQuery(id+"F0.wireOp",EDGE,"E9.trimOffspring");var subQ2=makeQuery(id+"F0.imprint","INTERSECT",VERTEX,{"derivedFrom":[subQ1,subQ0]});Q316=makeQuery(id+"F0.imprint","IMPRINT",FACE,{"disambiguationData":[TD([[makeQuery(id+"F0.imprint","IMPRINT",EDGE,{"disambiguationData":[TD([[subQ2,-1.0]])],"derivedFrom":subQ1}),1.0]])]});}
            var Q317;
            {var subQ0=sQuery(id+"F0.wireOp",EDGE,"E26.trimOffspring");var subQ1=sQuery(id+"F0.wireOp",EDGE,"E1");var subQ2=makeQuery(id+"F0.imprint","INTERSECT",VERTEX,{"derivedFrom":[subQ1,subQ0]});Q317=makeQuery(id+"F0.imprint","IMPRINT",FACE,{"disambiguationData":[TD([[makeQuery(id+"F0.imprint","IMPRINT",EDGE,{"disambiguationData":[TD([[subQ2,-1.0]])],"derivedFrom":subQ1}),-1.0]])]});}
            var Q318;
            {var subQ0=sQuery(id+"F0.wireOp",EDGE,"E22.4.0.0");var subQ1=sQuery(id+"F0.wireOp",EDGE,"E0.4");var subQ2=makeQuery(id+"F0.imprint","INTERSECT",VERTEX,{"derivedFrom":[subQ1,subQ0]});Q318=makeQuery(id+"F0.imprint","IMPRINT",FACE,{"disambiguationData":[TD([[makeQuery(id+"F0.imprint","IMPRINT",EDGE,{"disambiguationData":[TD([[subQ2,-1.0]])],"derivedFrom":subQ1}),-1.0]])]});}
            var Q319;
            {var subQ0=sQuery(id+"F0.wireOp",EDGE,"E19.trimOffspring");var subQ1=sQuery(id+"F0.wireOp",EDGE,"E0.0");var subQ2=makeQuery(id+"F0.imprint","INTERSECT",VERTEX,{"derivedFrom":[subQ1,subQ0]});Q319=makeQuery(id+"F0.imprint","IMPRINT",FACE,{"disambiguationData":[TD([[makeQuery(id+"F0.imprint","IMPRINT",EDGE,{"disambiguationData":[TD([[subQ2,-1.0]])],"derivedFrom":subQ1}),-1.0]])]});}
            var Q320;
            {var subQ0=sQuery(id+"F0.wireOp",EDGE,"E13.trimOffspring");var subQ1=sQuery(id+"F0.wireOp",EDGE,"E0.0");var subQ2=makeQuery(id+"F0.imprint","INTERSECT",VERTEX,{"derivedFrom":[subQ1,subQ0]});Q320=makeQuery(id+"F0.imprint","IMPRINT",FACE,{"disambiguationData":[TD([[makeQuery(id+"F0.imprint","IMPRINT",EDGE,{"disambiguationData":[TD([[subQ2,-1.0]])],"derivedFrom":subQ1}),-1.0]])]});}
            var Q321;
            {var subQ1=sQuery(id+"F0.wireOp",EDGE,"E0.3");var subQ3=sQuery(id+"F0.wireOp",EDGE,"E3.trimOffspring");var subQ4=makeQuery(id+"F0.imprint","INTERSECT",VERTEX,{"derivedFrom":[subQ1,subQ3]});Q321=makeQuery(id+"F0.imprint","IMPRINT",FACE,{"disambiguationData":[TD([[makeQuery(id+"F0.imprint","IMPRINT",EDGE,{"disambiguationData":[TD([[subQ4,1.0]])],"derivedFrom":subQ3}),-1.0]])]});}
            var Q322;
            {var subQ1=sQuery(id+"F0.wireOp",EDGE,"E3.trimOffspring");var subQ6=sQuery(id+"F0.wireOp",EDGE,"E0.3");var subQ9=makeQuery(id+"F0.imprint","INTERSECT",VERTEX,{"derivedFrom":[subQ6,subQ1]});Q322=makeQuery(id+"F0.imprint","IMPRINT",FACE,{"disambiguationData":[TD([[makeQuery(id+"F0.imprint","IMPRINT",EDGE,{"disambiguationData":[TD([[subQ9,1.0]])],"derivedFrom":subQ6}),-1.0]])]});}
            var Q323;
            {var subQ0=sQuery(id+"F0.wireOp",EDGE,"E4.trimOffspring");var subQ1=sQuery(id+"F0.wireOp",EDGE,"E0.3");var subQ2=makeQuery(id+"F0.imprint","INTERSECT",VERTEX,{"derivedFrom":[subQ1,subQ0]});Q323=makeQuery(id+"F0.imprint","IMPRINT",FACE,{"disambiguationData":[TD([[makeQuery(id+"F0.imprint","IMPRINT",EDGE,{"disambiguationData":[TD([[subQ2,1.0]])],"derivedFrom":subQ1}),-1.0]])]});}
            var Q324;
            {var subQ0=sQuery(id+"F0.wireOp",EDGE,"E21.4.0.0");var subQ1=sQuery(id+"F0.wireOp",EDGE,"E3.trimOffspring");var subQ2=makeQuery(id+"F0.imprint","INTERSECT",VERTEX,{"derivedFrom":[subQ1,subQ0]});Q324=makeQuery(id+"F0.imprint","IMPRINT",FACE,{"disambiguationData":[TD([[makeQuery(id+"F0.imprint","IMPRINT",EDGE,{"disambiguationData":[TD([[subQ2,-1.0]])],"derivedFrom":subQ1}),1.0]])]});}
            var Q325;
            {var subQ0=sQuery(id+"F0.wireOp",EDGE,"E21.6.0.0");var subQ1=sQuery(id+"F0.wireOp",EDGE,"E6.trimOffspring");var subQ2=makeQuery(id+"F0.imprint","INTERSECT",VERTEX,{"derivedFrom":[subQ1,subQ0]});Q325=makeQuery(id+"F0.imprint","IMPRINT",FACE,{"disambiguationData":[TD([[makeQuery(id+"F0.imprint","IMPRINT",EDGE,{"disambiguationData":[TD([[subQ2,-1.0]])],"derivedFrom":subQ1}),1.0]])]});}
            var Q326;
            {var subQ0=sQuery(id+"F0.wireOp",EDGE,"E20");var subQ1=sQuery(id+"F0.wireOp",EDGE,"E0.1");var subQ2=makeQuery(id+"F0.imprint","INTERSECT",VERTEX,{"derivedFrom":[subQ1,subQ0]});Q326=makeQuery(id+"F0.imprint","IMPRINT",FACE,{"disambiguationData":[TD([[makeQuery(id+"F0.imprint","IMPRINT",EDGE,{"disambiguationData":[TD([[subQ2,1.0]])],"derivedFrom":subQ1}),-1.0]])]});}
            var Q327;
            {var subQ0=sQuery(id+"F0.wireOp",EDGE,"E21.1.0.0");var subQ1=sQuery(id+"F0.wireOp",EDGE,"E0.1");var subQ2=makeQuery(id+"F0.imprint","INTERSECT",VERTEX,{"derivedFrom":[subQ1,subQ0]});Q327=makeQuery(id+"F0.imprint","IMPRINT",FACE,{"disambiguationData":[TD([[makeQuery(id+"F0.imprint","IMPRINT",EDGE,{"disambiguationData":[TD([[subQ2,-1.0]])],"derivedFrom":subQ1}),-1.0]])]});}
            var Q328;
            {var subQ0=sQuery(id+"F0.wireOp",EDGE,"E26.trimOffspring");var subQ1=sQuery(id+"F0.wireOp",EDGE,"E7.trimOffspring");var subQ2=makeQuery(id+"F0.imprint","INTERSECT",VERTEX,{"derivedFrom":[subQ1,subQ0]});Q328=makeQuery(id+"F0.imprint","IMPRINT",FACE,{"disambiguationData":[TD([[makeQuery(id+"F0.imprint","IMPRINT",EDGE,{"disambiguationData":[TD([[subQ2,-1.0]])],"derivedFrom":subQ1}),1.0]])]});}
            var Q329;
            {var subQ0=sQuery(id+"F0.wireOp",EDGE,"E25.trimOffspring");var subQ1=sQuery(id+"F0.wireOp",EDGE,"E14.trimOffspring");var subQ2=makeQuery(id+"F0.imprint","INTERSECT",VERTEX,{"derivedFrom":[subQ1,subQ0]});Q329=makeQuery(id+"F0.imprint","IMPRINT",FACE,{"disambiguationData":[TD([[makeQuery(id+"F0.imprint","IMPRINT",EDGE,{"disambiguationData":[TD([[subQ2,-1.0]])],"derivedFrom":subQ1}),1.0]])]});}
            var Q330;
            {var subQ0=sQuery(id+"F0.wireOp",EDGE,"E21.6.0.0");var subQ1=sQuery(id+"F0.wireOp",EDGE,"E12.trimOffspring");var subQ2=makeQuery(id+"F0.imprint","INTERSECT",VERTEX,{"derivedFrom":[subQ1,subQ0]});Q330=makeQuery(id+"F0.imprint","IMPRINT",FACE,{"disambiguationData":[TD([[makeQuery(id+"F0.imprint","IMPRINT",EDGE,{"disambiguationData":[TD([[subQ2,-1.0]])],"derivedFrom":subQ1}),1.0]])]});}
            var Q331;
            {var subQ0=sQuery(id+"F0.wireOp",EDGE,"E25.trimOffspring");var subQ1=sQuery(id+"F0.wireOp",EDGE,"E9.trimOffspring");var subQ2=makeQuery(id+"F0.imprint","INTERSECT",VERTEX,{"derivedFrom":[subQ1,subQ0]});Q331=makeQuery(id+"F0.imprint","IMPRINT",FACE,{"disambiguationData":[TD([[makeQuery(id+"F0.imprint","IMPRINT",EDGE,{"disambiguationData":[TD([[subQ2,-1.0]])],"derivedFrom":subQ1}),1.0]])]});}
            var Q332;
            {var subQ0=sQuery(id+"F0.wireOp",EDGE,"E18.trimOffspring");var subQ1=sQuery(id+"F0.wireOp",EDGE,"E0.0");var subQ2=makeQuery(id+"F0.imprint","INTERSECT",VERTEX,{"derivedFrom":[subQ1,subQ0]});Q332=makeQuery(id+"F0.imprint","IMPRINT",FACE,{"disambiguationData":[TD([[makeQuery(id+"F0.imprint","IMPRINT",EDGE,{"disambiguationData":[TD([[subQ2,-1.0]])],"derivedFrom":subQ1}),-1.0]])]});}
            var Q333;
            {var subQ0=sQuery(id+"F0.wireOp",EDGE,"E22.1.0.0");var subQ1=sQuery(id+"F0.wireOp",EDGE,"E3.trimOffspring");var subQ2=makeQuery(id+"F0.imprint","INTERSECT",VERTEX,{"derivedFrom":[subQ1,subQ0]});Q333=makeQuery(id+"F0.imprint","IMPRINT",FACE,{"disambiguationData":[TD([[makeQuery(id+"F0.imprint","IMPRINT",EDGE,{"disambiguationData":[TD([[subQ2,-1.0]])],"derivedFrom":subQ1}),1.0]])]});}
            var Q334;
            {var subQ0=sQuery(id+"F0.wireOp",EDGE,"E22.8.0.0");var subQ1=sQuery(id+"F0.wireOp",EDGE,"E14.trimOffspring");var subQ2=makeQuery(id+"F0.imprint","INTERSECT",VERTEX,{"derivedFrom":[subQ1,subQ0]});Q334=makeQuery(id+"F0.imprint","IMPRINT",FACE,{"disambiguationData":[TD([[makeQuery(id+"F0.imprint","IMPRINT",EDGE,{"disambiguationData":[TD([[subQ2,-1.0]])],"derivedFrom":subQ1}),1.0]])]});}
            var Q335;
            {var subQ1=sQuery(id+"F0.wireOp",EDGE,"E2.0.9.0");var subQ6=sQuery(id+"F0.wireOp",EDGE,"E0.2");var subQ9=makeQuery(id+"F0.imprint","INTERSECT",VERTEX,{"derivedFrom":[subQ6,subQ1]});Q335=makeQuery(id+"F0.imprint","IMPRINT",FACE,{"disambiguationData":[TD([[makeQuery(id+"F0.imprint","IMPRINT",EDGE,{"disambiguationData":[TD([[subQ9,-1.0]])],"derivedFrom":subQ6}),-1.0]])]});}
            var Q336;
            {var subQ0=sQuery(id+"F0.wireOp",EDGE,"E21.2.0.0");var subQ1=sQuery(id+"F0.wireOp",EDGE,"E0.1");var subQ2=makeQuery(id+"F0.imprint","INTERSECT",VERTEX,{"derivedFrom":[subQ1,subQ0]});Q336=makeQuery(id+"F0.imprint","IMPRINT",FACE,{"disambiguationData":[TD([[makeQuery(id+"F0.imprint","IMPRINT",EDGE,{"disambiguationData":[TD([[subQ2,-1.0]])],"derivedFrom":subQ1}),-1.0]])]});}
            var Q337;
            {var subQ5=sQuery(id+"F0.wireOp",EDGE,"E6.trimOffspring");var subQ6=sQuery(id+"F0.wireOp",EDGE,"E0.3");var subQ7=makeQuery(id+"F0.imprint","INTERSECT",VERTEX,{"derivedFrom":[subQ6,subQ5]});Q337=makeQuery(id+"F0.imprint","IMPRINT",FACE,{"disambiguationData":[TD([[makeQuery(id+"F0.imprint","IMPRINT",EDGE,{"disambiguationData":[TD([[subQ7,1.0]])],"derivedFrom":subQ6}),-1.0]])]});}
            var Q338;
            {var subQ0=sQuery(id+"F0.wireOp",EDGE,"E21.5.0.0");var subQ1=sQuery(id+"F0.wireOp",EDGE,"E3.trimOffspring");var subQ2=makeQuery(id+"F0.imprint","INTERSECT",VERTEX,{"derivedFrom":[subQ1,subQ0]});Q338=makeQuery(id+"F0.imprint","IMPRINT",FACE,{"disambiguationData":[TD([[makeQuery(id+"F0.imprint","IMPRINT",EDGE,{"disambiguationData":[TD([[subQ2,-1.0]])],"derivedFrom":subQ1}),1.0]])]});}
            var Q339;
            {var subQ0=sQuery(id+"F0.wireOp",EDGE,"E22.2.0.0");var subQ1=sQuery(id+"F0.wireOp",EDGE,"E0.1");var subQ2=makeQuery(id+"F0.imprint","INTERSECT",VERTEX,{"derivedFrom":[subQ1,subQ0]});Q339=makeQuery(id+"F0.imprint","IMPRINT",FACE,{"disambiguationData":[TD([[makeQuery(id+"F0.imprint","IMPRINT",EDGE,{"disambiguationData":[TD([[subQ2,1.0]])],"derivedFrom":subQ1}),-1.0]])]});}
            var Q340;
            {var subQ1=sQuery(id+"F0.wireOp",EDGE,"E0.3");var subQ3=sQuery(id+"F0.wireOp",EDGE,"E11.trimOffspring");var subQ4=makeQuery(id+"F0.imprint","INTERSECT",VERTEX,{"derivedFrom":[subQ1,subQ3]});Q340=makeQuery(id+"F0.imprint","IMPRINT",FACE,{"disambiguationData":[TD([[makeQuery(id+"F0.imprint","IMPRINT",EDGE,{"disambiguationData":[TD([[subQ4,1.0]])],"derivedFrom":subQ3}),1.0]])]});}
            var Q341;
            {var subQ0=sQuery(id+"F0.wireOp",EDGE,"E21.4.0.0");var subQ1=sQuery(id+"F0.wireOp",EDGE,"E0.1");var subQ2=makeQuery(id+"F0.imprint","INTERSECT",VERTEX,{"derivedFrom":[subQ1,subQ0]});Q341=makeQuery(id+"F0.imprint","IMPRINT",FACE,{"disambiguationData":[TD([[makeQuery(id+"F0.imprint","IMPRINT",EDGE,{"disambiguationData":[TD([[subQ2,-1.0]])],"derivedFrom":subQ1}),-1.0]])]});}
            var Q342;
            {var subQ0=sQuery(id+"F0.wireOp",EDGE,"E22.9.0.0");var subQ1=sQuery(id+"F0.wireOp",EDGE,"E10.trimOffspring");var subQ2=makeQuery(id+"F0.imprint","INTERSECT",VERTEX,{"derivedFrom":[subQ1,subQ0]});Q342=makeQuery(id+"F0.imprint","IMPRINT",FACE,{"disambiguationData":[TD([[makeQuery(id+"F0.imprint","IMPRINT",EDGE,{"disambiguationData":[TD([[subQ2,-1.0]])],"derivedFrom":subQ1}),1.0]])]});}
            var Q343;
            {var subQ0=sQuery(id+"F0.wireOp",EDGE,"E22.3.0.0");var subQ1=sQuery(id+"F0.wireOp",EDGE,"E3.trimOffspring");var subQ2=makeQuery(id+"F0.imprint","INTERSECT",VERTEX,{"derivedFrom":[subQ1,subQ0]});Q343=makeQuery(id+"F0.imprint","IMPRINT",FACE,{"disambiguationData":[TD([[makeQuery(id+"F0.imprint","IMPRINT",EDGE,{"disambiguationData":[TD([[subQ2,-1.0]])],"derivedFrom":subQ1}),1.0]])]});}
            var Q344;
            {var subQ0=sQuery(id+"F0.wireOp",EDGE,"E20");var subQ1=sQuery(id+"F0.wireOp",EDGE,"E0.4");var subQ2=makeQuery(id+"F0.imprint","INTERSECT",VERTEX,{"derivedFrom":[subQ1,subQ0]});Q344=makeQuery(id+"F0.imprint","IMPRINT",FACE,{"disambiguationData":[TD([[makeQuery(id+"F0.imprint","IMPRINT",EDGE,{"disambiguationData":[TD([[subQ2,-1.0]])],"derivedFrom":subQ1}),-1.0]])]});}
            var Q345;
            {var subQ0=sQuery(id+"F0.wireOp",EDGE,"E12.trimOffspring");var subQ1=sQuery(id+"F0.wireOp",EDGE,"E0.2");var subQ2=makeQuery(id+"F0.imprint","INTERSECT",VERTEX,{"derivedFrom":[subQ1,subQ0]});Q345=makeQuery(id+"F0.imprint","IMPRINT",FACE,{"disambiguationData":[TD([[makeQuery(id+"F0.imprint","IMPRINT",EDGE,{"disambiguationData":[TD([[subQ2,1.0]])],"derivedFrom":subQ1}),-1.0]])]});}
            var Q346;
            {var subQ0=sQuery(id+"F0.wireOp",EDGE,"E22.8.0.0");var subQ1=sQuery(id+"F0.wireOp",EDGE,"E15.trimOffspring");var subQ2=makeQuery(id+"F0.imprint","INTERSECT",VERTEX,{"derivedFrom":[subQ1,subQ0]});Q346=makeQuery(id+"F0.imprint","IMPRINT",FACE,{"disambiguationData":[TD([[makeQuery(id+"F0.imprint","IMPRINT",EDGE,{"disambiguationData":[TD([[subQ2,-1.0]])],"derivedFrom":subQ1}),1.0]])]});}
            var Q347;
            {var subQ0=sQuery(id+"F0.wireOp",EDGE,"E26.trimOffspring");var subQ1=sQuery(id+"F0.wireOp",EDGE,"E14.trimOffspring");var subQ2=makeQuery(id+"F0.imprint","INTERSECT",VERTEX,{"derivedFrom":[subQ1,subQ0]});Q347=makeQuery(id+"F0.imprint","IMPRINT",FACE,{"disambiguationData":[TD([[makeQuery(id+"F0.imprint","IMPRINT",EDGE,{"disambiguationData":[TD([[subQ2,-1.0]])],"derivedFrom":subQ1}),1.0]])]});}
            var Q348;
            {var subQ0=sQuery(id+"F0.wireOp",EDGE,"E22.9.0.0");var subQ1=sQuery(id+"F0.wireOp",EDGE,"E8.trimOffspring");var subQ2=makeQuery(id+"F0.imprint","INTERSECT",VERTEX,{"derivedFrom":[subQ1,subQ0]});Q348=makeQuery(id+"F0.imprint","IMPRINT",FACE,{"disambiguationData":[TD([[makeQuery(id+"F0.imprint","IMPRINT",EDGE,{"disambiguationData":[TD([[subQ2,-1.0]])],"derivedFrom":subQ1}),1.0]])]});}
            var Q349;
            {var subQ0=sQuery(id+"F0.wireOp",EDGE,"E8.trimOffspring");var subQ1=sQuery(id+"F0.wireOp",EDGE,"E0.5");var subQ2=makeQuery(id+"F0.imprint","INTERSECT",VERTEX,{"derivedFrom":[subQ1,subQ0]});Q349=makeQuery(id+"F0.imprint","IMPRINT",FACE,{"disambiguationData":[TD([[makeQuery(id+"F0.imprint","IMPRINT",EDGE,{"disambiguationData":[TD([[subQ2,-1.0]])],"derivedFrom":subQ1}),-1.0]])]});}
            var Q350;
            {var subQ0=sQuery(id+"F0.wireOp",EDGE,"E22.9.0.0");var subQ1=sQuery(id+"F0.wireOp",EDGE,"E1");var subQ2=makeQuery(id+"F0.imprint","INTERSECT",VERTEX,{"derivedFrom":[subQ1,subQ0]});Q350=makeQuery(id+"F0.imprint","IMPRINT",FACE,{"disambiguationData":[TD([[makeQuery(id+"F0.imprint","IMPRINT",EDGE,{"disambiguationData":[TD([[subQ2,-1.0]])],"derivedFrom":subQ1}),1.0]])]});}
            var Q351;
            {var subQ3=sQuery(id+"F0.wireOp",EDGE,"E21.5.0.0");var subQ5=sQuery(id+"F0.wireOp",EDGE,"E3.trimOffspring");var subQ6=makeQuery(id+"F0.imprint","INTERSECT",VERTEX,{"derivedFrom":[subQ5,subQ3]});Q351=makeQuery(id+"F0.imprint","IMPRINT",FACE,{"disambiguationData":[TD([[makeQuery(id+"F0.imprint","IMPRINT",EDGE,{"disambiguationData":[TD([[subQ6,-1.0]])],"derivedFrom":subQ5}),-1.0]])]});}
            var Q352;
            {var subQ0=sQuery(id+"F0.wireOp",EDGE,"E25.trimOffspring");var subQ1=sQuery(id+"F0.wireOp",EDGE,"E15.trimOffspring");var subQ2=makeQuery(id+"F0.imprint","INTERSECT",VERTEX,{"derivedFrom":[subQ1,subQ0]});Q352=makeQuery(id+"F0.imprint","IMPRINT",FACE,{"disambiguationData":[TD([[makeQuery(id+"F0.imprint","IMPRINT",EDGE,{"disambiguationData":[TD([[subQ2,-1.0]])],"derivedFrom":subQ1}),1.0]])]});}
            var Q353;
            {var subQ0=sQuery(id+"F0.wireOp",EDGE,"E7.trimOffspring");var subQ1=sQuery(id+"F0.wireOp",EDGE,"E0.5");var subQ2=makeQuery(id+"F0.imprint","INTERSECT",VERTEX,{"derivedFrom":[subQ1,subQ0]});Q353=makeQuery(id+"F0.imprint","IMPRINT",FACE,{"disambiguationData":[TD([[makeQuery(id+"F0.imprint","IMPRINT",EDGE,{"disambiguationData":[TD([[subQ2,-1.0]])],"derivedFrom":subQ1}),-1.0]])]});}
            var Q354;
            {var subQ0=sQuery(id+"F0.wireOp",EDGE,"E25.trimOffspring");var subQ1=sQuery(id+"F0.wireOp",EDGE,"E1");var subQ2=makeQuery(id+"F0.imprint","INTERSECT",VERTEX,{"derivedFrom":[subQ1,subQ0]});Q354=makeQuery(id+"F0.imprint","IMPRINT",FACE,{"disambiguationData":[TD([[makeQuery(id+"F0.imprint","IMPRINT",EDGE,{"disambiguationData":[TD([[subQ2,-1.0]])],"derivedFrom":subQ1}),1.0]])]});}
            var Q355;
            {var subQ0=sQuery(id+"F0.wireOp",EDGE,"E26.trimOffspring");var subQ1=sQuery(id+"F0.wireOp",EDGE,"E8.trimOffspring");var subQ2=makeQuery(id+"F0.imprint","INTERSECT",VERTEX,{"derivedFrom":[subQ1,subQ0]});Q355=makeQuery(id+"F0.imprint","IMPRINT",FACE,{"disambiguationData":[TD([[makeQuery(id+"F0.imprint","IMPRINT",EDGE,{"disambiguationData":[TD([[subQ2,-1.0]])],"derivedFrom":subQ1}),1.0]])]});}
            var Q356;
            {var subQ0=sQuery(id+"F0.wireOp",EDGE,"E21.2.0.0");var subQ1=sQuery(id+"F0.wireOp",EDGE,"E0.4");var subQ2=makeQuery(id+"F0.imprint","INTERSECT",VERTEX,{"derivedFrom":[subQ1,subQ0]});Q356=makeQuery(id+"F0.imprint","IMPRINT",FACE,{"disambiguationData":[TD([[makeQuery(id+"F0.imprint","IMPRINT",EDGE,{"disambiguationData":[TD([[subQ2,1.0]])],"derivedFrom":subQ1}),-1.0]])]});}
            var Q357;
            {var subQ0=sQuery(id+"F0.wireOp",EDGE,"E22.8.0.0");var subQ1=sQuery(id+"F0.wireOp",EDGE,"E13.trimOffspring");var subQ2=makeQuery(id+"F0.imprint","INTERSECT",VERTEX,{"derivedFrom":[subQ1,subQ0]});Q357=makeQuery(id+"F0.imprint","IMPRINT",FACE,{"disambiguationData":[TD([[makeQuery(id+"F0.imprint","IMPRINT",EDGE,{"disambiguationData":[TD([[subQ2,-1.0]])],"derivedFrom":subQ1}),1.0]])]});}
            var Q358;
            {var subQ0=sQuery(id+"F0.wireOp",EDGE,"E16.trimOffspring");var subQ1=sQuery(id+"F0.wireOp",EDGE,"E0.0");var subQ2=makeQuery(id+"F0.imprint","INTERSECT",VERTEX,{"derivedFrom":[subQ1,subQ0]});Q358=makeQuery(id+"F0.imprint","IMPRINT",FACE,{"disambiguationData":[TD([[makeQuery(id+"F0.imprint","IMPRINT",EDGE,{"disambiguationData":[TD([[subQ2,-1.0]])],"derivedFrom":subQ1}),-1.0]])]});}
            var Q359;
            {var subQ0=sQuery(id+"F0.wireOp",EDGE,"E7.trimOffspring");var subQ1=sQuery(id+"F0.wireOp",EDGE,"E0.3");var subQ2=makeQuery(id+"F0.imprint","INTERSECT",VERTEX,{"derivedFrom":[subQ1,subQ0]});Q359=makeQuery(id+"F0.imprint","IMPRINT",FACE,{"disambiguationData":[TD([[makeQuery(id+"F0.imprint","IMPRINT",EDGE,{"disambiguationData":[TD([[subQ2,-1.0]])],"derivedFrom":subQ1}),-1.0]])]});}
            var Q360;
            {var subQ0=sQuery(id+"F0.wireOp",EDGE,"E16.trimOffspring");var subQ1=sQuery(id+"F0.wireOp",EDGE,"E0.2");var subQ2=makeQuery(id+"F0.imprint","INTERSECT",VERTEX,{"derivedFrom":[subQ1,subQ0]});Q360=makeQuery(id+"F0.imprint","IMPRINT",FACE,{"disambiguationData":[TD([[makeQuery(id+"F0.imprint","IMPRINT",EDGE,{"disambiguationData":[TD([[subQ2,1.0]])],"derivedFrom":subQ1}),-1.0]])]});}
            var Q361;
            {var subQ0=sQuery(id+"F0.wireOp",EDGE,"E4.trimOffspring");var subQ1=sQuery(id+"F0.wireOp",EDGE,"E0.3");var subQ2=makeQuery(id+"F0.imprint","INTERSECT",VERTEX,{"derivedFrom":[subQ1,subQ0]});Q361=makeQuery(id+"F0.imprint","IMPRINT",FACE,{"disambiguationData":[TD([[makeQuery(id+"F0.imprint","IMPRINT",EDGE,{"disambiguationData":[TD([[subQ2,-1.0]])],"derivedFrom":subQ1}),-1.0]])]});}
            var Q362;
            {var subQ0=sQuery(id+"F0.wireOp",EDGE,"E4.trimOffspring");var subQ1=sQuery(id+"F0.wireOp",EDGE,"E0.5");var subQ2=makeQuery(id+"F0.imprint","INTERSECT",VERTEX,{"derivedFrom":[subQ1,subQ0]});Q362=makeQuery(id+"F0.imprint","IMPRINT",FACE,{"disambiguationData":[TD([[makeQuery(id+"F0.imprint","IMPRINT",EDGE,{"disambiguationData":[TD([[subQ2,1.0]])],"derivedFrom":subQ1}),-1.0]])]});}
            var Q363;
            {var subQ0=sQuery(id+"F0.wireOp",EDGE,"E7.trimOffspring");var subQ1=sQuery(id+"F0.wireOp",EDGE,"E0.5");var subQ2=makeQuery(id+"F0.imprint","INTERSECT",VERTEX,{"derivedFrom":[subQ1,subQ0]});Q363=makeQuery(id+"F0.imprint","IMPRINT",FACE,{"disambiguationData":[TD([[makeQuery(id+"F0.imprint","IMPRINT",EDGE,{"disambiguationData":[TD([[subQ2,1.0]])],"derivedFrom":subQ1}),-1.0]])]});}
            var Q364;
            {var subQ0=sQuery(id+"F0.wireOp",EDGE,"E12.trimOffspring");var subQ1=sQuery(id+"F0.wireOp",EDGE,"E0.0");var subQ2=makeQuery(id+"F0.imprint","INTERSECT",VERTEX,{"derivedFrom":[subQ1,subQ0]});Q364=makeQuery(id+"F0.imprint","IMPRINT",FACE,{"disambiguationData":[TD([[makeQuery(id+"F0.imprint","IMPRINT",EDGE,{"disambiguationData":[TD([[subQ2,-1.0]])],"derivedFrom":subQ1}),-1.0]])]});}
            var Q365;
            {var subQ1=sQuery(id+"F0.wireOp",EDGE,"E0.0");var subQ3=sQuery(id+"F0.wireOp",EDGE,"E12.trimOffspring");var subQ4=makeQuery(id+"F0.imprint","INTERSECT",VERTEX,{"derivedFrom":[subQ1,subQ3]});Q365=makeQuery(id+"F0.imprint","IMPRINT",FACE,{"disambiguationData":[TD([[makeQuery(id+"F0.imprint","IMPRINT",EDGE,{"disambiguationData":[TD([[subQ4,-1.0]])],"derivedFrom":subQ3}),-1.0]])]});}
            var Q366;
            {var subQ1=sQuery(id+"F0.wireOp",EDGE,"E0.5");var subQ3=sQuery(id+"F0.wireOp",EDGE,"E11.trimOffspring");var subQ4=makeQuery(id+"F0.imprint","INTERSECT",VERTEX,{"derivedFrom":[subQ1,subQ3]});Q366=makeQuery(id+"F0.imprint","IMPRINT",FACE,{"disambiguationData":[TD([[makeQuery(id+"F0.imprint","IMPRINT",EDGE,{"disambiguationData":[TD([[subQ4,-1.0]])],"derivedFrom":subQ3}),1.0]])]});}
            var Q367;
            {var subQ0=sQuery(id+"F0.wireOp",EDGE,"E10.trimOffspring");var subQ1=sQuery(id+"F0.wireOp",EDGE,"E0.5");var subQ2=makeQuery(id+"F0.imprint","INTERSECT",VERTEX,{"derivedFrom":[subQ1,subQ0]});Q367=makeQuery(id+"F0.imprint","IMPRINT",FACE,{"disambiguationData":[TD([[makeQuery(id+"F0.imprint","IMPRINT",EDGE,{"disambiguationData":[TD([[subQ2,-1.0]])],"derivedFrom":subQ1}),-1.0]])]});}
            extrude(context, id + "F1", {"entities" : qUnion([Q0, Q1, Q2, Q3, Q4, Q5, Q6, Q7, Q8, Q9, Q10, Q11, Q12, Q13, Q14, Q15, Q16, Q17, Q18, Q19, Q20, Q21, Q22, Q23, Q24, Q25, Q26, Q27, Q28, Q29, Q30, Q31, Q32, Q33, Q34, Q35, Q36, Q37, Q38, Q39, Q40, Q41, Q42, Q43, Q44, Q45, Q46, Q47, Q48, Q49, Q50, Q51, Q52, Q53, Q54, Q55, Q56, Q57, Q58, Q59, Q60, Q61, Q62, Q63, Q64, Q65, Q66, Q67, Q68, Q69, Q70, Q71, Q72, Q73, Q74, Q75, Q76, Q77, Q78, Q79, Q80, Q81, Q82, Q83, Q84, Q85, Q86, Q87, Q88, Q89, Q90, Q91, Q92, Q93, Q94, Q95, Q96, Q97, Q98, Q99, Q100, Q101, Q102, Q103, Q104, Q105, Q106, Q107, Q108, Q109, Q110, Q111, Q112, Q113, Q114, Q115, Q116, Q117, Q118, Q119, Q120, Q121, Q122, Q123, Q124, Q125, Q126, Q127, Q128, Q129, Q130, Q131, Q132, Q133, Q134, Q135, Q136, Q137, Q138, Q139, Q140, Q141, Q142, Q143, Q144, Q145, Q146, Q147, Q148, Q149, Q150, Q151, Q152, Q153, Q154, Q155, Q156, Q157, Q158, Q159, Q160, Q161, Q162, Q163, Q164, Q165, Q166, Q167, Q168, Q169, Q170, Q171, Q172, Q173, Q174, Q175, Q176, Q177, Q178, Q179, Q180, Q181, Q182, Q183, Q184, Q185, Q186, Q187, Q188, Q189, Q190, Q191, Q192, Q193, Q194, Q195, Q196, Q197, Q198, Q199, Q200, Q201, Q202, Q203, Q204, Q205, Q206, Q207, Q208, Q209, Q210, Q211, Q212, Q213, Q214, Q215, Q216, Q217, Q218, Q219, Q220, Q221, Q222, Q223, Q224, Q225, Q226, Q227, Q228, Q229, Q230, Q231, Q232, Q233, Q234, Q235, Q236, Q237, Q238, Q239, Q240, Q241, Q242, Q243, Q244, Q245, Q246, Q247, Q248, Q249, Q250, Q251, Q252, Q253, Q254, Q255, Q256, Q257, Q258, Q259, Q260, Q261, Q262, Q263, Q264, Q265, Q266, Q267, Q268, Q269, Q270, Q271, Q272, Q273, Q274, Q275, Q276, Q277, Q278, Q279, Q280, Q281, Q282, Q283, Q284, Q285, Q286, Q287, Q288, Q289, Q290, Q291, Q292, Q293, Q294, Q295, Q296, Q297, Q298, Q299, Q300, Q301, Q302, Q303, Q304, Q305, Q306, Q307, Q308, Q309, Q310, Q311, Q312, Q313, Q314, Q315, Q316, Q317, Q318, Q319, Q320, Q321, Q322, Q323, Q324, Q325, Q326, Q327, Q328, Q329, Q330, Q331, Q332, Q333, Q334, Q335, Q336, Q337, Q338, Q339, Q340, Q341, Q342, Q343, Q344, Q345, Q346, Q347, Q348, Q349, Q350, Q351, Q352, Q353, Q354, Q355, Q356, Q357, Q358, Q359, Q360, Q361, Q362, Q363, Q364, Q365, Q366, Q367]), "depth" : 2 * mm, "offsetDistance" : 25 * mm});
        }
        {
            var Q0;
            {var subQ0=sQuery(id+"F0.wireOp",EDGE,"E22.3.0.0");var subQ1=sQuery(id+"F0.wireOp",EDGE,"E13.trimOffspring");var subQ2=makeQuery(id+"F0.imprint","INTERSECT",VERTEX,{"derivedFrom":[subQ1,subQ0]});Q0=makeQuery(id+"F0.imprint","IMPRINT",FACE,{"disambiguationData":[TD([[makeQuery(id+"F0.imprint","IMPRINT",EDGE,{"disambiguationData":[TD([[subQ2,-1.0]])],"derivedFrom":subQ1}),1.0]])]});}
            var Q1;
            {var subQ0=sQuery(id+"F0.wireOp",EDGE,"E22.1.0.0");var subQ1=sQuery(id+"F0.wireOp",EDGE,"E14.trimOffspring");var subQ2=makeQuery(id+"F0.imprint","INTERSECT",VERTEX,{"derivedFrom":[subQ1,subQ0]});Q1=makeQuery(id+"F0.imprint","IMPRINT",FACE,{"disambiguationData":[TD([[makeQuery(id+"F0.imprint","IMPRINT",EDGE,{"disambiguationData":[TD([[subQ2,-1.0]])],"derivedFrom":subQ1}),1.0]])]});}
            var Q2;
            {var subQ0=sQuery(id+"F0.wireOp",EDGE,"E21.1.0.0");var subQ1=sQuery(id+"F0.wireOp",EDGE,"E16.trimOffspring");var subQ2=makeQuery(id+"F0.imprint","INTERSECT",VERTEX,{"derivedFrom":[subQ1,subQ0]});Q2=makeQuery(id+"F0.imprint","IMPRINT",FACE,{"disambiguationData":[TD([[makeQuery(id+"F0.imprint","IMPRINT",EDGE,{"disambiguationData":[TD([[subQ2,-1.0]])],"derivedFrom":subQ1}),1.0]])]});}
            var Q3;
            {var subQ0=sQuery(id+"F0.wireOp",EDGE,"E22.1.0.0");var subQ1=sQuery(id+"F0.wireOp",EDGE,"E8.trimOffspring");var subQ2=makeQuery(id+"F0.imprint","INTERSECT",VERTEX,{"derivedFrom":[subQ1,subQ0]});Q3=makeQuery(id+"F0.imprint","IMPRINT",FACE,{"disambiguationData":[TD([[makeQuery(id+"F0.imprint","IMPRINT",EDGE,{"disambiguationData":[TD([[subQ2,-1.0]])],"derivedFrom":subQ1}),1.0]])]});}
            var Q4;
            {var subQ0=sQuery(id+"F0.wireOp",EDGE,"E22.4.0.0");var subQ1=sQuery(id+"F0.wireOp",EDGE,"E7.trimOffspring");var subQ2=makeQuery(id+"F0.imprint","INTERSECT",VERTEX,{"derivedFrom":[subQ1,subQ0]});Q4=makeQuery(id+"F0.imprint","IMPRINT",FACE,{"disambiguationData":[TD([[makeQuery(id+"F0.imprint","IMPRINT",EDGE,{"disambiguationData":[TD([[subQ2,-1.0]])],"derivedFrom":subQ1}),1.0]])]});}
            var Q5;
            {var subQ0=sQuery(id+"F0.wireOp",EDGE,"E23.trimOffspring");var subQ1=sQuery(id+"F0.wireOp",EDGE,"E10.trimOffspring");var subQ2=makeQuery(id+"F0.imprint","INTERSECT",VERTEX,{"derivedFrom":[subQ1,subQ0]});Q5=makeQuery(id+"F0.imprint","IMPRINT",FACE,{"disambiguationData":[TD([[makeQuery(id+"F0.imprint","IMPRINT",EDGE,{"disambiguationData":[TD([[subQ2,-1.0]])],"derivedFrom":subQ1}),1.0]])]});}
            var Q6;
            {var subQ0=sQuery(id+"F0.wireOp",EDGE,"E22.5.0.0");var subQ1=sQuery(id+"F0.wireOp",EDGE,"E4.trimOffspring");var subQ2=makeQuery(id+"F0.imprint","INTERSECT",VERTEX,{"derivedFrom":[subQ1,subQ0]});Q6=makeQuery(id+"F0.imprint","IMPRINT",FACE,{"disambiguationData":[TD([[makeQuery(id+"F0.imprint","IMPRINT",EDGE,{"disambiguationData":[TD([[subQ2,-1.0]])],"derivedFrom":subQ1}),1.0]])]});}
            var Q7;
            {var subQ0=sQuery(id+"F0.wireOp",EDGE,"E22.9.0.0");var subQ1=sQuery(id+"F0.wireOp",EDGE,"E1");var subQ2=makeQuery(id+"F0.imprint","INTERSECT",VERTEX,{"derivedFrom":[subQ1,subQ0]});Q7=makeQuery(id+"F0.imprint","IMPRINT",FACE,{"disambiguationData":[TD([[makeQuery(id+"F0.imprint","IMPRINT",EDGE,{"disambiguationData":[TD([[subQ2,-1.0]])],"derivedFrom":subQ1}),-1.0]])]});}
            var Q8;
            {var subQ0=sQuery(id+"F0.wireOp",EDGE,"E22.8.0.0");var subQ1=sQuery(id+"F0.wireOp",EDGE,"E13.trimOffspring");var subQ2=makeQuery(id+"F0.imprint","INTERSECT",VERTEX,{"derivedFrom":[subQ1,subQ0]});Q8=makeQuery(id+"F0.imprint","IMPRINT",FACE,{"disambiguationData":[TD([[makeQuery(id+"F0.imprint","IMPRINT",EDGE,{"disambiguationData":[TD([[subQ2,-1.0]])],"derivedFrom":subQ1}),1.0]])]});}
            var Q9;
            {var subQ0=sQuery(id+"F0.wireOp",EDGE,"E22.8.0.0");var subQ1=sQuery(id+"F0.wireOp",EDGE,"E14.trimOffspring");var subQ2=makeQuery(id+"F0.imprint","INTERSECT",VERTEX,{"derivedFrom":[subQ1,subQ0]});Q9=makeQuery(id+"F0.imprint","IMPRINT",FACE,{"disambiguationData":[TD([[makeQuery(id+"F0.imprint","IMPRINT",EDGE,{"disambiguationData":[TD([[subQ2,-1.0]])],"derivedFrom":subQ1}),1.0]])]});}
            var Q10;
            {var subQ0=sQuery(id+"F0.wireOp",EDGE,"E23.trimOffspring");var subQ1=sQuery(id+"F0.wireOp",EDGE,"E17.trimOffspring");var subQ2=makeQuery(id+"F0.imprint","INTERSECT",VERTEX,{"derivedFrom":[subQ1,subQ0]});Q10=makeQuery(id+"F0.imprint","IMPRINT",FACE,{"disambiguationData":[TD([[makeQuery(id+"F0.imprint","IMPRINT",EDGE,{"disambiguationData":[TD([[subQ2,-1.0]])],"derivedFrom":subQ1}),1.0]])]});}
            var Q11;
            {var subQ0=sQuery(id+"F0.wireOp",EDGE,"E22.5.0.0");var subQ1=sQuery(id+"F0.wireOp",EDGE,"E2.0.9.0");var subQ2=makeQuery(id+"F0.imprint","INTERSECT",VERTEX,{"derivedFrom":[subQ1,subQ0]});Q11=makeQuery(id+"F0.imprint","IMPRINT",FACE,{"disambiguationData":[TD([[makeQuery(id+"F0.imprint","IMPRINT",EDGE,{"disambiguationData":[TD([[subQ2,-1.0]])],"derivedFrom":subQ1}),-1.0]])]});}
            var Q12;
            {var subQ0=sQuery(id+"F0.wireOp",EDGE,"E21.3.0.0");var subQ1=sQuery(id+"F0.wireOp",EDGE,"E2.0.9.0");var subQ2=makeQuery(id+"F0.imprint","INTERSECT",VERTEX,{"derivedFrom":[subQ1,subQ0]});Q12=makeQuery(id+"F0.imprint","IMPRINT",FACE,{"disambiguationData":[TD([[makeQuery(id+"F0.imprint","IMPRINT",EDGE,{"disambiguationData":[TD([[subQ2,-1.0]])],"derivedFrom":subQ1}),-1.0]])]});}
            var Q13;
            {var subQ0=sQuery(id+"F0.wireOp",EDGE,"E21.2.0.0");var subQ1=sQuery(id+"F0.wireOp",EDGE,"E2.0.9.0");var subQ2=makeQuery(id+"F0.imprint","INTERSECT",VERTEX,{"derivedFrom":[subQ1,subQ0]});Q13=makeQuery(id+"F0.imprint","IMPRINT",FACE,{"disambiguationData":[TD([[makeQuery(id+"F0.imprint","IMPRINT",EDGE,{"disambiguationData":[TD([[subQ2,-1.0]])],"derivedFrom":subQ1}),-1.0]])]});}
            var Q14;
            {var subQ0=sQuery(id+"F0.wireOp",EDGE,"E21.5.0.0");var subQ1=sQuery(id+"F0.wireOp",EDGE,"E16.trimOffspring");var subQ2=makeQuery(id+"F0.imprint","INTERSECT",VERTEX,{"derivedFrom":[subQ1,subQ0]});Q14=makeQuery(id+"F0.imprint","IMPRINT",FACE,{"disambiguationData":[TD([[makeQuery(id+"F0.imprint","IMPRINT",EDGE,{"disambiguationData":[TD([[subQ2,-1.0]])],"derivedFrom":subQ1}),1.0]])]});}
            var Q15;
            {var subQ0=sQuery(id+"F0.wireOp",EDGE,"E21.6.0.0");var subQ1=sQuery(id+"F0.wireOp",EDGE,"E17.trimOffspring");var subQ2=makeQuery(id+"F0.imprint","INTERSECT",VERTEX,{"derivedFrom":[subQ1,subQ0]});Q15=makeQuery(id+"F0.imprint","IMPRINT",FACE,{"disambiguationData":[TD([[makeQuery(id+"F0.imprint","IMPRINT",EDGE,{"disambiguationData":[TD([[subQ2,-1.0]])],"derivedFrom":subQ1}),1.0]])]});}
            var Q16;
            {var subQ0=sQuery(id+"F0.wireOp",EDGE,"E21.6.0.0");var subQ1=sQuery(id+"F0.wireOp",EDGE,"E14.trimOffspring");var subQ2=makeQuery(id+"F0.imprint","INTERSECT",VERTEX,{"derivedFrom":[subQ1,subQ0]});Q16=makeQuery(id+"F0.imprint","IMPRINT",FACE,{"disambiguationData":[TD([[makeQuery(id+"F0.imprint","IMPRINT",EDGE,{"disambiguationData":[TD([[subQ2,-1.0]])],"derivedFrom":subQ1}),1.0]])]});}
            var Q17;
            {var subQ0=sQuery(id+"F0.wireOp",EDGE,"E21.6.0.0");var subQ1=sQuery(id+"F0.wireOp",EDGE,"E12.trimOffspring");var subQ2=makeQuery(id+"F0.imprint","INTERSECT",VERTEX,{"derivedFrom":[subQ1,subQ0]});Q17=makeQuery(id+"F0.imprint","IMPRINT",FACE,{"disambiguationData":[TD([[makeQuery(id+"F0.imprint","IMPRINT",EDGE,{"disambiguationData":[TD([[subQ2,-1.0]])],"derivedFrom":subQ1}),1.0]])]});}
            var Q18;
            {var subQ0=sQuery(id+"F0.wireOp",EDGE,"E25.trimOffspring");var subQ1=sQuery(id+"F0.wireOp",EDGE,"E13.trimOffspring");var subQ2=makeQuery(id+"F0.imprint","INTERSECT",VERTEX,{"derivedFrom":[subQ1,subQ0]});Q18=makeQuery(id+"F0.imprint","IMPRINT",FACE,{"disambiguationData":[TD([[makeQuery(id+"F0.imprint","IMPRINT",EDGE,{"disambiguationData":[TD([[subQ2,-1.0]])],"derivedFrom":subQ1}),1.0]])]});}
            var Q19;
            {var subQ0=sQuery(id+"F0.wireOp",EDGE,"E25.trimOffspring");var subQ1=sQuery(id+"F0.wireOp",EDGE,"E10.trimOffspring");var subQ2=makeQuery(id+"F0.imprint","INTERSECT",VERTEX,{"derivedFrom":[subQ1,subQ0]});Q19=makeQuery(id+"F0.imprint","IMPRINT",FACE,{"disambiguationData":[TD([[makeQuery(id+"F0.imprint","IMPRINT",EDGE,{"disambiguationData":[TD([[subQ2,-1.0]])],"derivedFrom":subQ1}),1.0]])]});}
            var Q20;
            {var subQ0=sQuery(id+"F0.wireOp",EDGE,"E21.4.0.0");var subQ1=sQuery(id+"F0.wireOp",EDGE,"E7.trimOffspring");var subQ2=makeQuery(id+"F0.imprint","INTERSECT",VERTEX,{"derivedFrom":[subQ1,subQ0]});Q20=makeQuery(id+"F0.imprint","IMPRINT",FACE,{"disambiguationData":[TD([[makeQuery(id+"F0.imprint","IMPRINT",EDGE,{"disambiguationData":[TD([[subQ2,-1.0]])],"derivedFrom":subQ1}),1.0]])]});}
            var Q21;
            {var subQ0=sQuery(id+"F0.wireOp",EDGE,"E21.3.0.0");var subQ1=sQuery(id+"F0.wireOp",EDGE,"E5.trimOffspring");var subQ2=makeQuery(id+"F0.imprint","INTERSECT",VERTEX,{"derivedFrom":[subQ1,subQ0]});Q21=makeQuery(id+"F0.imprint","IMPRINT",FACE,{"disambiguationData":[TD([[makeQuery(id+"F0.imprint","IMPRINT",EDGE,{"disambiguationData":[TD([[subQ2,-1.0]])],"derivedFrom":subQ1}),1.0]])]});}
            var Q22;
            {var subQ0=sQuery(id+"F0.wireOp",EDGE,"E21.6.0.0");var subQ1=sQuery(id+"F0.wireOp",EDGE,"E16.trimOffspring");var subQ2=makeQuery(id+"F0.imprint","INTERSECT",VERTEX,{"derivedFrom":[subQ1,subQ0]});Q22=makeQuery(id+"F0.imprint","IMPRINT",FACE,{"disambiguationData":[TD([[makeQuery(id+"F0.imprint","IMPRINT",EDGE,{"disambiguationData":[TD([[subQ2,-1.0]])],"derivedFrom":subQ1}),1.0]])]});}
            var Q23;
            {var subQ0=sQuery(id+"F0.wireOp",EDGE,"E22.3.0.0");var subQ1=sQuery(id+"F0.wireOp",EDGE,"E16.trimOffspring");var subQ2=makeQuery(id+"F0.imprint","INTERSECT",VERTEX,{"derivedFrom":[subQ1,subQ0]});Q23=makeQuery(id+"F0.imprint","IMPRINT",FACE,{"disambiguationData":[TD([[makeQuery(id+"F0.imprint","IMPRINT",EDGE,{"disambiguationData":[TD([[subQ2,-1.0]])],"derivedFrom":subQ1}),1.0]])]});}
            var Q24;
            {var subQ0=sQuery(id+"F0.wireOp",EDGE,"E22.4.0.0");var subQ1=sQuery(id+"F0.wireOp",EDGE,"E16.trimOffspring");var subQ2=makeQuery(id+"F0.imprint","INTERSECT",VERTEX,{"derivedFrom":[subQ1,subQ0]});Q24=makeQuery(id+"F0.imprint","IMPRINT",FACE,{"disambiguationData":[TD([[makeQuery(id+"F0.imprint","IMPRINT",EDGE,{"disambiguationData":[TD([[subQ2,-1.0]])],"derivedFrom":subQ1}),1.0]])]});}
            var Q25;
            {var subQ0=sQuery(id+"F0.wireOp",EDGE,"E22.4.0.0");var subQ1=sQuery(id+"F0.wireOp",EDGE,"E1");var subQ2=makeQuery(id+"F0.imprint","INTERSECT",VERTEX,{"derivedFrom":[subQ1,subQ0]});Q25=makeQuery(id+"F0.imprint","IMPRINT",FACE,{"disambiguationData":[TD([[makeQuery(id+"F0.imprint","IMPRINT",EDGE,{"disambiguationData":[TD([[subQ2,-1.0]])],"derivedFrom":subQ1}),-1.0]])]});}
            var Q26;
            {var subQ0=sQuery(id+"F0.wireOp",EDGE,"E22.6.0.0");var subQ1=sQuery(id+"F0.wireOp",EDGE,"E13.trimOffspring");var subQ2=makeQuery(id+"F0.imprint","INTERSECT",VERTEX,{"derivedFrom":[subQ1,subQ0]});Q26=makeQuery(id+"F0.imprint","IMPRINT",FACE,{"disambiguationData":[TD([[makeQuery(id+"F0.imprint","IMPRINT",EDGE,{"disambiguationData":[TD([[subQ2,-1.0]])],"derivedFrom":subQ1}),1.0]])]});}
            var Q27;
            {var subQ0=sQuery(id+"F0.wireOp",EDGE,"E22.2.0.0");var subQ1=sQuery(id+"F0.wireOp",EDGE,"E4.trimOffspring");var subQ2=makeQuery(id+"F0.imprint","INTERSECT",VERTEX,{"derivedFrom":[subQ1,subQ0]});Q27=makeQuery(id+"F0.imprint","IMPRINT",FACE,{"disambiguationData":[TD([[makeQuery(id+"F0.imprint","IMPRINT",EDGE,{"disambiguationData":[TD([[subQ2,-1.0]])],"derivedFrom":subQ1}),1.0]])]});}
            var Q28;
            {var subQ0=sQuery(id+"F0.wireOp",EDGE,"E21.6.0.0");var subQ1=sQuery(id+"F0.wireOp",EDGE,"E5.trimOffspring");var subQ2=makeQuery(id+"F0.imprint","INTERSECT",VERTEX,{"derivedFrom":[subQ1,subQ0]});Q28=makeQuery(id+"F0.imprint","IMPRINT",FACE,{"disambiguationData":[TD([[makeQuery(id+"F0.imprint","IMPRINT",EDGE,{"disambiguationData":[TD([[subQ2,-1.0]])],"derivedFrom":subQ1}),1.0]])]});}
            var Q29;
            {var subQ0=sQuery(id+"F0.wireOp",EDGE,"E21.3.0.0");var subQ1=sQuery(id+"F0.wireOp",EDGE,"E1");var subQ2=makeQuery(id+"F0.imprint","INTERSECT",VERTEX,{"derivedFrom":[subQ1,subQ0]});Q29=makeQuery(id+"F0.imprint","IMPRINT",FACE,{"disambiguationData":[TD([[makeQuery(id+"F0.imprint","IMPRINT",EDGE,{"disambiguationData":[TD([[subQ2,-1.0]])],"derivedFrom":subQ1}),-1.0]])]});}
            var Q30;
            {var subQ0=sQuery(id+"F0.wireOp",EDGE,"E21.3.0.0");var subQ1=sQuery(id+"F0.wireOp",EDGE,"E10.trimOffspring");var subQ2=makeQuery(id+"F0.imprint","INTERSECT",VERTEX,{"derivedFrom":[subQ1,subQ0]});Q30=makeQuery(id+"F0.imprint","IMPRINT",FACE,{"disambiguationData":[TD([[makeQuery(id+"F0.imprint","IMPRINT",EDGE,{"disambiguationData":[TD([[subQ2,-1.0]])],"derivedFrom":subQ1}),1.0]])]});}
            var Q31;
            {var subQ0=sQuery(id+"F0.wireOp",EDGE,"E21.1.0.0");var subQ1=sQuery(id+"F0.wireOp",EDGE,"E10.trimOffspring");var subQ2=makeQuery(id+"F0.imprint","INTERSECT",VERTEX,{"derivedFrom":[subQ1,subQ0]});Q31=makeQuery(id+"F0.imprint","IMPRINT",FACE,{"disambiguationData":[TD([[makeQuery(id+"F0.imprint","IMPRINT",EDGE,{"disambiguationData":[TD([[subQ2,-1.0]])],"derivedFrom":subQ1}),1.0]])]});}
            var Q32;
            {var subQ0=sQuery(id+"F0.wireOp",EDGE,"E21.2.0.0");var subQ1=sQuery(id+"F0.wireOp",EDGE,"E13.trimOffspring");var subQ2=makeQuery(id+"F0.imprint","INTERSECT",VERTEX,{"derivedFrom":[subQ1,subQ0]});Q32=makeQuery(id+"F0.imprint","IMPRINT",FACE,{"disambiguationData":[TD([[makeQuery(id+"F0.imprint","IMPRINT",EDGE,{"disambiguationData":[TD([[subQ2,-1.0]])],"derivedFrom":subQ1}),1.0]])]});}
            var Q33;
            {var subQ0=sQuery(id+"F0.wireOp",EDGE,"E22.1.0.0");var subQ1=sQuery(id+"F0.wireOp",EDGE,"E2.0.9.0");var subQ2=makeQuery(id+"F0.imprint","INTERSECT",VERTEX,{"derivedFrom":[subQ1,subQ0]});Q33=makeQuery(id+"F0.imprint","IMPRINT",FACE,{"disambiguationData":[TD([[makeQuery(id+"F0.imprint","IMPRINT",EDGE,{"disambiguationData":[TD([[subQ2,-1.0]])],"derivedFrom":subQ1}),-1.0]])]});}
            var Q34;
            {var subQ0=sQuery(id+"F0.wireOp",EDGE,"E22.8.0.0");var subQ1=sQuery(id+"F0.wireOp",EDGE,"E6.trimOffspring");var subQ2=makeQuery(id+"F0.imprint","INTERSECT",VERTEX,{"derivedFrom":[subQ1,subQ0]});Q34=makeQuery(id+"F0.imprint","IMPRINT",FACE,{"disambiguationData":[TD([[makeQuery(id+"F0.imprint","IMPRINT",EDGE,{"disambiguationData":[TD([[subQ2,-1.0]])],"derivedFrom":subQ1}),1.0]])]});}
            var Q35;
            {var subQ0=sQuery(id+"F0.wireOp",EDGE,"E22.1.0.0");var subQ1=sQuery(id+"F0.wireOp",EDGE,"E3.trimOffspring");var subQ2=makeQuery(id+"F0.imprint","INTERSECT",VERTEX,{"derivedFrom":[subQ1,subQ0]});Q35=makeQuery(id+"F0.imprint","IMPRINT",FACE,{"disambiguationData":[TD([[makeQuery(id+"F0.imprint","IMPRINT",EDGE,{"disambiguationData":[TD([[subQ2,-1.0]])],"derivedFrom":subQ1}),1.0]])]});}
            var Q36;
            {var subQ0=sQuery(id+"F0.wireOp",EDGE,"E21.5.0.0");var subQ1=sQuery(id+"F0.wireOp",EDGE,"E8.trimOffspring");var subQ2=makeQuery(id+"F0.imprint","INTERSECT",VERTEX,{"derivedFrom":[subQ1,subQ0]});Q36=makeQuery(id+"F0.imprint","IMPRINT",FACE,{"disambiguationData":[TD([[makeQuery(id+"F0.imprint","IMPRINT",EDGE,{"disambiguationData":[TD([[subQ2,-1.0]])],"derivedFrom":subQ1}),1.0]])]});}
            var Q37;
            {var subQ0=sQuery(id+"F0.wireOp",EDGE,"E22.1.0.0");var subQ1=sQuery(id+"F0.wireOp",EDGE,"E4.trimOffspring");var subQ2=makeQuery(id+"F0.imprint","INTERSECT",VERTEX,{"derivedFrom":[subQ1,subQ0]});Q37=makeQuery(id+"F0.imprint","IMPRINT",FACE,{"disambiguationData":[TD([[makeQuery(id+"F0.imprint","IMPRINT",EDGE,{"disambiguationData":[TD([[subQ2,-1.0]])],"derivedFrom":subQ1}),1.0]])]});}
            var Q38;
            {var subQ0=sQuery(id+"F0.wireOp",EDGE,"E21.4.0.0");var subQ1=sQuery(id+"F0.wireOp",EDGE,"E3.trimOffspring");var subQ2=makeQuery(id+"F0.imprint","INTERSECT",VERTEX,{"derivedFrom":[subQ1,subQ0]});Q38=makeQuery(id+"F0.imprint","IMPRINT",FACE,{"disambiguationData":[TD([[makeQuery(id+"F0.imprint","IMPRINT",EDGE,{"disambiguationData":[TD([[subQ2,-1.0]])],"derivedFrom":subQ1}),1.0]])]});}
            var Q39;
            {var subQ0=sQuery(id+"F0.wireOp",EDGE,"E21.5.0.0");var subQ1=sQuery(id+"F0.wireOp",EDGE,"E7.trimOffspring");var subQ2=makeQuery(id+"F0.imprint","INTERSECT",VERTEX,{"derivedFrom":[subQ1,subQ0]});Q39=makeQuery(id+"F0.imprint","IMPRINT",FACE,{"disambiguationData":[TD([[makeQuery(id+"F0.imprint","IMPRINT",EDGE,{"disambiguationData":[TD([[subQ2,-1.0]])],"derivedFrom":subQ1}),1.0]])]});}
            var Q40;
            {var subQ0=sQuery(id+"F0.wireOp",EDGE,"E21.1.0.0");var subQ1=sQuery(id+"F0.wireOp",EDGE,"E6.trimOffspring");var subQ2=makeQuery(id+"F0.imprint","INTERSECT",VERTEX,{"derivedFrom":[subQ1,subQ0]});Q40=makeQuery(id+"F0.imprint","IMPRINT",FACE,{"disambiguationData":[TD([[makeQuery(id+"F0.imprint","IMPRINT",EDGE,{"disambiguationData":[TD([[subQ2,-1.0]])],"derivedFrom":subQ1}),1.0]])]});}
            extrude(context, id + "F2", {"entities" : qUnion([Q0, Q1, Q2, Q3, Q4, Q5, Q6, Q7, Q8, Q9, Q10, Q11, Q12, Q13, Q14, Q15, Q16, Q17, Q18, Q19, Q20, Q21, Q22, Q23, Q24, Q25, Q26, Q27, Q28, Q29, Q30, Q31, Q32, Q33, Q34, Q35, Q36, Q37, Q38, Q39, Q40]), "operationType" : NewBodyOperationType.ADD, "depth" : 4 * mm, "offsetDistance" : 25 * mm});
        }
        {
            var Q0;
            {var subQ0=sQuery(id+"F0.wireOp",EDGE,"E22.3.0.0");var subQ1=sQuery(id+"F0.wireOp",EDGE,"E7.trimOffspring");var subQ2=makeQuery(id+"F0.imprint","INTERSECT",VERTEX,{"derivedFrom":[subQ1,subQ0]});Q0=makeQuery(id+"F0.imprint","IMPRINT",FACE,{"disambiguationData":[TD([[makeQuery(id+"F0.imprint","IMPRINT",EDGE,{"disambiguationData":[TD([[subQ2,-1.0]])],"derivedFrom":subQ1}),1.0]])]});}
            var Q1;
            {var subQ0=sQuery(id+"F0.wireOp",EDGE,"E20");var subQ1=sQuery(id+"F0.wireOp",EDGE,"E6.trimOffspring");var subQ2=makeQuery(id+"F0.imprint","INTERSECT",VERTEX,{"derivedFrom":[subQ1,subQ0]});Q1=makeQuery(id+"F0.imprint","IMPRINT",FACE,{"disambiguationData":[TD([[makeQuery(id+"F0.imprint","IMPRINT",EDGE,{"disambiguationData":[TD([[subQ2,-1.0]])],"derivedFrom":subQ1}),1.0]])]});}
            var Q2;
            {var subQ0=sQuery(id+"F0.wireOp",EDGE,"E21.1.0.0");var subQ1=sQuery(id+"F0.wireOp",EDGE,"E7.trimOffspring");var subQ2=makeQuery(id+"F0.imprint","INTERSECT",VERTEX,{"derivedFrom":[subQ1,subQ0]});Q2=makeQuery(id+"F0.imprint","IMPRINT",FACE,{"disambiguationData":[TD([[makeQuery(id+"F0.imprint","IMPRINT",EDGE,{"disambiguationData":[TD([[subQ2,-1.0]])],"derivedFrom":subQ1}),1.0]])]});}
            var Q3;
            {var subQ0=sQuery(id+"F0.wireOp",EDGE,"E21.1.0.0");var subQ1=sQuery(id+"F0.wireOp",EDGE,"E6.trimOffspring");var subQ2=makeQuery(id+"F0.imprint","INTERSECT",VERTEX,{"derivedFrom":[subQ1,subQ0]});Q3=makeQuery(id+"F0.imprint","IMPRINT",FACE,{"disambiguationData":[TD([[makeQuery(id+"F0.imprint","IMPRINT",EDGE,{"disambiguationData":[TD([[subQ2,-1.0]])],"derivedFrom":subQ1}),1.0]])]});}
            var Q4;
            {var subQ0=sQuery(id+"F0.wireOp",EDGE,"E21.4.0.0");var subQ1=sQuery(id+"F0.wireOp",EDGE,"E6.trimOffspring");var subQ2=makeQuery(id+"F0.imprint","INTERSECT",VERTEX,{"derivedFrom":[subQ1,subQ0]});Q4=makeQuery(id+"F0.imprint","IMPRINT",FACE,{"disambiguationData":[TD([[makeQuery(id+"F0.imprint","IMPRINT",EDGE,{"disambiguationData":[TD([[subQ2,-1.0]])],"derivedFrom":subQ1}),1.0]])]});}
            var Q5;
            {var subQ0=sQuery(id+"F0.wireOp",EDGE,"E21.4.0.0");var subQ1=sQuery(id+"F0.wireOp",EDGE,"E3.trimOffspring");var subQ2=makeQuery(id+"F0.imprint","INTERSECT",VERTEX,{"derivedFrom":[subQ1,subQ0]});Q5=makeQuery(id+"F0.imprint","IMPRINT",FACE,{"disambiguationData":[TD([[makeQuery(id+"F0.imprint","IMPRINT",EDGE,{"disambiguationData":[TD([[subQ2,-1.0]])],"derivedFrom":subQ1}),1.0]])]});}
            var Q6;
            {var subQ0=sQuery(id+"F0.wireOp",EDGE,"E22.6.0.0");var subQ1=sQuery(id+"F0.wireOp",EDGE,"E5.trimOffspring");var subQ2=makeQuery(id+"F0.imprint","INTERSECT",VERTEX,{"derivedFrom":[subQ1,subQ0]});Q6=makeQuery(id+"F0.imprint","IMPRINT",FACE,{"disambiguationData":[TD([[makeQuery(id+"F0.imprint","IMPRINT",EDGE,{"disambiguationData":[TD([[subQ2,-1.0]])],"derivedFrom":subQ1}),1.0]])]});}
            var Q7;
            {var subQ0=sQuery(id+"F0.wireOp",EDGE,"E22.5.0.0");var subQ1=sQuery(id+"F0.wireOp",EDGE,"E5.trimOffspring");var subQ2=makeQuery(id+"F0.imprint","INTERSECT",VERTEX,{"derivedFrom":[subQ1,subQ0]});Q7=makeQuery(id+"F0.imprint","IMPRINT",FACE,{"disambiguationData":[TD([[makeQuery(id+"F0.imprint","IMPRINT",EDGE,{"disambiguationData":[TD([[subQ2,-1.0]])],"derivedFrom":subQ1}),1.0]])]});}
            var Q8;
            {var subQ0=sQuery(id+"F0.wireOp",EDGE,"E22.6.0.0");var subQ1=sQuery(id+"F0.wireOp",EDGE,"E7.trimOffspring");var subQ2=makeQuery(id+"F0.imprint","INTERSECT",VERTEX,{"derivedFrom":[subQ1,subQ0]});Q8=makeQuery(id+"F0.imprint","IMPRINT",FACE,{"disambiguationData":[TD([[makeQuery(id+"F0.imprint","IMPRINT",EDGE,{"disambiguationData":[TD([[subQ2,-1.0]])],"derivedFrom":subQ1}),1.0]])]});}
            var Q9;
            {var subQ0=sQuery(id+"F0.wireOp",EDGE,"E22.8.0.0");var subQ1=sQuery(id+"F0.wireOp",EDGE,"E7.trimOffspring");var subQ2=makeQuery(id+"F0.imprint","INTERSECT",VERTEX,{"derivedFrom":[subQ1,subQ0]});Q9=makeQuery(id+"F0.imprint","IMPRINT",FACE,{"disambiguationData":[TD([[makeQuery(id+"F0.imprint","IMPRINT",EDGE,{"disambiguationData":[TD([[subQ2,-1.0]])],"derivedFrom":subQ1}),1.0]])]});}
            var Q10;
            {var subQ0=sQuery(id+"F0.wireOp",EDGE,"E22.8.0.0");var subQ1=sQuery(id+"F0.wireOp",EDGE,"E9.trimOffspring");var subQ2=makeQuery(id+"F0.imprint","INTERSECT",VERTEX,{"derivedFrom":[subQ1,subQ0]});Q10=makeQuery(id+"F0.imprint","IMPRINT",FACE,{"disambiguationData":[TD([[makeQuery(id+"F0.imprint","IMPRINT",EDGE,{"disambiguationData":[TD([[subQ2,-1.0]])],"derivedFrom":subQ1}),1.0]])]});}
            var Q11;
            {var subQ0=sQuery(id+"F0.wireOp",EDGE,"E22.4.0.0");var subQ1=sQuery(id+"F0.wireOp",EDGE,"E10.trimOffspring");var subQ2=makeQuery(id+"F0.imprint","INTERSECT",VERTEX,{"derivedFrom":[subQ1,subQ0]});Q11=makeQuery(id+"F0.imprint","IMPRINT",FACE,{"disambiguationData":[TD([[makeQuery(id+"F0.imprint","IMPRINT",EDGE,{"disambiguationData":[TD([[subQ2,-1.0]])],"derivedFrom":subQ1}),1.0]])]});}
            var Q12;
            {var subQ0=sQuery(id+"F0.wireOp",EDGE,"E22.6.0.0");var subQ1=sQuery(id+"F0.wireOp",EDGE,"E1");var subQ2=makeQuery(id+"F0.imprint","INTERSECT",VERTEX,{"derivedFrom":[subQ1,subQ0]});Q12=makeQuery(id+"F0.imprint","IMPRINT",FACE,{"disambiguationData":[TD([[makeQuery(id+"F0.imprint","IMPRINT",EDGE,{"disambiguationData":[TD([[subQ2,-1.0]])],"derivedFrom":subQ1}),-1.0]])]});}
            var Q13;
            {var subQ0=sQuery(id+"F0.wireOp",EDGE,"E23.trimOffspring");var subQ1=sQuery(id+"F0.wireOp",EDGE,"E12.trimOffspring");var subQ2=makeQuery(id+"F0.imprint","INTERSECT",VERTEX,{"derivedFrom":[subQ1,subQ0]});Q13=makeQuery(id+"F0.imprint","IMPRINT",FACE,{"disambiguationData":[TD([[makeQuery(id+"F0.imprint","IMPRINT",EDGE,{"disambiguationData":[TD([[subQ2,-1.0]])],"derivedFrom":subQ1}),1.0]])]});}
            var Q14;
            {var subQ0=sQuery(id+"F0.wireOp",EDGE,"E22.9.0.0");var subQ1=sQuery(id+"F0.wireOp",EDGE,"E12.trimOffspring");var subQ2=makeQuery(id+"F0.imprint","INTERSECT",VERTEX,{"derivedFrom":[subQ1,subQ0]});Q14=makeQuery(id+"F0.imprint","IMPRINT",FACE,{"disambiguationData":[TD([[makeQuery(id+"F0.imprint","IMPRINT",EDGE,{"disambiguationData":[TD([[subQ2,-1.0]])],"derivedFrom":subQ1}),1.0]])]});}
            var Q15;
            {var subQ0=sQuery(id+"F0.wireOp",EDGE,"E22.8.0.0");var subQ1=sQuery(id+"F0.wireOp",EDGE,"E15.trimOffspring");var subQ2=makeQuery(id+"F0.imprint","INTERSECT",VERTEX,{"derivedFrom":[subQ1,subQ0]});Q15=makeQuery(id+"F0.imprint","IMPRINT",FACE,{"disambiguationData":[TD([[makeQuery(id+"F0.imprint","IMPRINT",EDGE,{"disambiguationData":[TD([[subQ2,-1.0]])],"derivedFrom":subQ1}),1.0]])]});}
            var Q16;
            {var subQ0=sQuery(id+"F0.wireOp",EDGE,"E23.trimOffspring");var subQ1=sQuery(id+"F0.wireOp",EDGE,"E15.trimOffspring");var subQ2=makeQuery(id+"F0.imprint","INTERSECT",VERTEX,{"derivedFrom":[subQ1,subQ0]});Q16=makeQuery(id+"F0.imprint","IMPRINT",FACE,{"disambiguationData":[TD([[makeQuery(id+"F0.imprint","IMPRINT",EDGE,{"disambiguationData":[TD([[subQ2,-1.0]])],"derivedFrom":subQ1}),1.0]])]});}
            var Q17;
            {var subQ0=sQuery(id+"F0.wireOp",EDGE,"E22.6.0.0");var subQ1=sQuery(id+"F0.wireOp",EDGE,"E17.trimOffspring");var subQ2=makeQuery(id+"F0.imprint","INTERSECT",VERTEX,{"derivedFrom":[subQ1,subQ0]});Q17=makeQuery(id+"F0.imprint","IMPRINT",FACE,{"disambiguationData":[TD([[makeQuery(id+"F0.imprint","IMPRINT",EDGE,{"disambiguationData":[TD([[subQ2,-1.0]])],"derivedFrom":subQ1}),1.0]])]});}
            var Q18;
            {var subQ0=sQuery(id+"F0.wireOp",EDGE,"E22.5.0.0");var subQ1=sQuery(id+"F0.wireOp",EDGE,"E2.0.9.0");var subQ2=makeQuery(id+"F0.imprint","INTERSECT",VERTEX,{"derivedFrom":[subQ1,subQ0]});Q18=makeQuery(id+"F0.imprint","IMPRINT",FACE,{"disambiguationData":[TD([[makeQuery(id+"F0.imprint","IMPRINT",EDGE,{"disambiguationData":[TD([[subQ2,-1.0]])],"derivedFrom":subQ1}),-1.0]])]});}
            var Q19;
            {var subQ0=sQuery(id+"F0.wireOp",EDGE,"E22.3.0.0");var subQ1=sQuery(id+"F0.wireOp",EDGE,"E2.0.9.0");var subQ2=makeQuery(id+"F0.imprint","INTERSECT",VERTEX,{"derivedFrom":[subQ1,subQ0]});Q19=makeQuery(id+"F0.imprint","IMPRINT",FACE,{"disambiguationData":[TD([[makeQuery(id+"F0.imprint","IMPRINT",EDGE,{"disambiguationData":[TD([[subQ2,-1.0]])],"derivedFrom":subQ1}),-1.0]])]});}
            var Q20;
            {var subQ0=sQuery(id+"F0.wireOp",EDGE,"E22.3.0.0");var subQ1=sQuery(id+"F0.wireOp",EDGE,"E18.trimOffspring");var subQ2=makeQuery(id+"F0.imprint","INTERSECT",VERTEX,{"derivedFrom":[subQ1,subQ0]});Q20=makeQuery(id+"F0.imprint","IMPRINT",FACE,{"disambiguationData":[TD([[makeQuery(id+"F0.imprint","IMPRINT",EDGE,{"disambiguationData":[TD([[subQ2,-1.0]])],"derivedFrom":subQ1}),1.0]])]});}
            var Q21;
            {var subQ0=sQuery(id+"F0.wireOp",EDGE,"E22.3.0.0");var subQ1=sQuery(id+"F0.wireOp",EDGE,"E15.trimOffspring");var subQ2=makeQuery(id+"F0.imprint","INTERSECT",VERTEX,{"derivedFrom":[subQ1,subQ0]});Q21=makeQuery(id+"F0.imprint","IMPRINT",FACE,{"disambiguationData":[TD([[makeQuery(id+"F0.imprint","IMPRINT",EDGE,{"disambiguationData":[TD([[subQ2,-1.0]])],"derivedFrom":subQ1}),1.0]])]});}
            var Q22;
            {var subQ0=sQuery(id+"F0.wireOp",EDGE,"E22.5.0.0");var subQ1=sQuery(id+"F0.wireOp",EDGE,"E13.trimOffspring");var subQ2=makeQuery(id+"F0.imprint","INTERSECT",VERTEX,{"derivedFrom":[subQ1,subQ0]});Q22=makeQuery(id+"F0.imprint","IMPRINT",FACE,{"disambiguationData":[TD([[makeQuery(id+"F0.imprint","IMPRINT",EDGE,{"disambiguationData":[TD([[subQ2,-1.0]])],"derivedFrom":subQ1}),1.0]])]});}
            var Q23;
            {var subQ0=sQuery(id+"F0.wireOp",EDGE,"E22.2.0.0");var subQ1=sQuery(id+"F0.wireOp",EDGE,"E1");var subQ2=makeQuery(id+"F0.imprint","INTERSECT",VERTEX,{"derivedFrom":[subQ1,subQ0]});Q23=makeQuery(id+"F0.imprint","IMPRINT",FACE,{"disambiguationData":[TD([[makeQuery(id+"F0.imprint","IMPRINT",EDGE,{"disambiguationData":[TD([[subQ2,-1.0]])],"derivedFrom":subQ1}),1.0]])]});}
            var Q24;
            {var subQ0=sQuery(id+"F0.wireOp",EDGE,"E21.2.0.0");var subQ1=sQuery(id+"F0.wireOp",EDGE,"E13.trimOffspring");var subQ2=makeQuery(id+"F0.imprint","INTERSECT",VERTEX,{"derivedFrom":[subQ1,subQ0]});Q24=makeQuery(id+"F0.imprint","IMPRINT",FACE,{"disambiguationData":[TD([[makeQuery(id+"F0.imprint","IMPRINT",EDGE,{"disambiguationData":[TD([[subQ2,-1.0]])],"derivedFrom":subQ1}),1.0]])]});}
            var Q25;
            {var subQ0=sQuery(id+"F0.wireOp",EDGE,"E20");var subQ1=sQuery(id+"F0.wireOp",EDGE,"E14.trimOffspring");var subQ2=makeQuery(id+"F0.imprint","INTERSECT",VERTEX,{"derivedFrom":[subQ1,subQ0]});Q25=makeQuery(id+"F0.imprint","IMPRINT",FACE,{"disambiguationData":[TD([[makeQuery(id+"F0.imprint","IMPRINT",EDGE,{"disambiguationData":[TD([[subQ2,-1.0]])],"derivedFrom":subQ1}),1.0]])]});}
            var Q26;
            {var subQ0=sQuery(id+"F0.wireOp",EDGE,"E21.2.0.0");var subQ1=sQuery(id+"F0.wireOp",EDGE,"E17.trimOffspring");var subQ2=makeQuery(id+"F0.imprint","INTERSECT",VERTEX,{"derivedFrom":[subQ1,subQ0]});Q26=makeQuery(id+"F0.imprint","IMPRINT",FACE,{"disambiguationData":[TD([[makeQuery(id+"F0.imprint","IMPRINT",EDGE,{"disambiguationData":[TD([[subQ2,-1.0]])],"derivedFrom":subQ1}),1.0]])]});}
            var Q27;
            {var subQ0=sQuery(id+"F0.wireOp",EDGE,"E21.2.0.0");var subQ1=sQuery(id+"F0.wireOp",EDGE,"E2.0.9.0");var subQ2=makeQuery(id+"F0.imprint","INTERSECT",VERTEX,{"derivedFrom":[subQ1,subQ0]});Q27=makeQuery(id+"F0.imprint","IMPRINT",FACE,{"disambiguationData":[TD([[makeQuery(id+"F0.imprint","IMPRINT",EDGE,{"disambiguationData":[TD([[subQ2,-1.0]])],"derivedFrom":subQ1}),-1.0]])]});}
            var Q28;
            {var subQ0=sQuery(id+"F0.wireOp",EDGE,"E21.5.0.0");var subQ1=sQuery(id+"F0.wireOp",EDGE,"E18.trimOffspring");var subQ2=makeQuery(id+"F0.imprint","INTERSECT",VERTEX,{"derivedFrom":[subQ1,subQ0]});Q28=makeQuery(id+"F0.imprint","IMPRINT",FACE,{"disambiguationData":[TD([[makeQuery(id+"F0.imprint","IMPRINT",EDGE,{"disambiguationData":[TD([[subQ2,-1.0]])],"derivedFrom":subQ1}),1.0]])]});}
            var Q29;
            {var subQ0=sQuery(id+"F0.wireOp",EDGE,"E26.trimOffspring");var subQ1=sQuery(id+"F0.wireOp",EDGE,"E16.trimOffspring");var subQ2=makeQuery(id+"F0.imprint","INTERSECT",VERTEX,{"derivedFrom":[subQ1,subQ0]});Q29=makeQuery(id+"F0.imprint","IMPRINT",FACE,{"disambiguationData":[TD([[makeQuery(id+"F0.imprint","IMPRINT",EDGE,{"disambiguationData":[TD([[subQ2,-1.0]])],"derivedFrom":subQ1}),1.0]])]});}
            var Q30;
            {var subQ0=sQuery(id+"F0.wireOp",EDGE,"E21.5.0.0");var subQ1=sQuery(id+"F0.wireOp",EDGE,"E15.trimOffspring");var subQ2=makeQuery(id+"F0.imprint","INTERSECT",VERTEX,{"derivedFrom":[subQ1,subQ0]});Q30=makeQuery(id+"F0.imprint","IMPRINT",FACE,{"disambiguationData":[TD([[makeQuery(id+"F0.imprint","IMPRINT",EDGE,{"disambiguationData":[TD([[subQ2,-1.0]])],"derivedFrom":subQ1}),1.0]])]});}
            var Q31;
            {var subQ0=sQuery(id+"F0.wireOp",EDGE,"E21.6.0.0");var subQ1=sQuery(id+"F0.wireOp",EDGE,"E13.trimOffspring");var subQ2=makeQuery(id+"F0.imprint","INTERSECT",VERTEX,{"derivedFrom":[subQ1,subQ0]});Q31=makeQuery(id+"F0.imprint","IMPRINT",FACE,{"disambiguationData":[TD([[makeQuery(id+"F0.imprint","IMPRINT",EDGE,{"disambiguationData":[TD([[subQ2,-1.0]])],"derivedFrom":subQ1}),1.0]])]});}
            var Q32;
            {var subQ0=sQuery(id+"F0.wireOp",EDGE,"E21.4.0.0");var subQ1=sQuery(id+"F0.wireOp",EDGE,"E1");var subQ2=makeQuery(id+"F0.imprint","INTERSECT",VERTEX,{"derivedFrom":[subQ1,subQ0]});Q32=makeQuery(id+"F0.imprint","IMPRINT",FACE,{"disambiguationData":[TD([[makeQuery(id+"F0.imprint","IMPRINT",EDGE,{"disambiguationData":[TD([[subQ2,-1.0]])],"derivedFrom":subQ1}),1.0]])]});}
            var Q33;
            {var subQ0=sQuery(id+"F0.wireOp",EDGE,"E21.5.0.0");var subQ1=sQuery(id+"F0.wireOp",EDGE,"E10.trimOffspring");var subQ2=makeQuery(id+"F0.imprint","INTERSECT",VERTEX,{"derivedFrom":[subQ1,subQ0]});Q33=makeQuery(id+"F0.imprint","IMPRINT",FACE,{"disambiguationData":[TD([[makeQuery(id+"F0.imprint","IMPRINT",EDGE,{"disambiguationData":[TD([[subQ2,-1.0]])],"derivedFrom":subQ1}),1.0]])]});}
            var Q34;
            {var subQ0=sQuery(id+"F0.wireOp",EDGE,"E21.4.0.0");var subQ1=sQuery(id+"F0.wireOp",EDGE,"E8.trimOffspring");var subQ2=makeQuery(id+"F0.imprint","INTERSECT",VERTEX,{"derivedFrom":[subQ1,subQ0]});Q34=makeQuery(id+"F0.imprint","IMPRINT",FACE,{"disambiguationData":[TD([[makeQuery(id+"F0.imprint","IMPRINT",EDGE,{"disambiguationData":[TD([[subQ2,-1.0]])],"derivedFrom":subQ1}),1.0]])]});}
            var Q35;
            {var subQ0=sQuery(id+"F0.wireOp",EDGE,"E21.5.0.0");var subQ1=sQuery(id+"F0.wireOp",EDGE,"E6.trimOffspring");var subQ2=makeQuery(id+"F0.imprint","INTERSECT",VERTEX,{"derivedFrom":[subQ1,subQ0]});Q35=makeQuery(id+"F0.imprint","IMPRINT",FACE,{"disambiguationData":[TD([[makeQuery(id+"F0.imprint","IMPRINT",EDGE,{"disambiguationData":[TD([[subQ2,-1.0]])],"derivedFrom":subQ1}),1.0]])]});}
            var Q36;
            {var subQ0=sQuery(id+"F0.wireOp",EDGE,"E20");var subQ1=sQuery(id+"F0.wireOp",EDGE,"E3.trimOffspring");var subQ2=makeQuery(id+"F0.imprint","INTERSECT",VERTEX,{"derivedFrom":[subQ1,subQ0]});Q36=makeQuery(id+"F0.imprint","IMPRINT",FACE,{"disambiguationData":[TD([[makeQuery(id+"F0.imprint","IMPRINT",EDGE,{"disambiguationData":[TD([[subQ2,-1.0]])],"derivedFrom":subQ1}),1.0]])]});}
            var Q37;
            {var subQ0=sQuery(id+"F0.wireOp",EDGE,"E21.6.0.0");var subQ1=sQuery(id+"F0.wireOp",EDGE,"E10.trimOffspring");var subQ2=makeQuery(id+"F0.imprint","INTERSECT",VERTEX,{"derivedFrom":[subQ1,subQ0]});Q37=makeQuery(id+"F0.imprint","IMPRINT",FACE,{"disambiguationData":[TD([[makeQuery(id+"F0.imprint","IMPRINT",EDGE,{"disambiguationData":[TD([[subQ2,-1.0]])],"derivedFrom":subQ1}),1.0]])]});}
            var Q38;
            {var subQ0=sQuery(id+"F0.wireOp",EDGE,"E25.trimOffspring");var subQ1=sQuery(id+"F0.wireOp",EDGE,"E1");var subQ2=makeQuery(id+"F0.imprint","INTERSECT",VERTEX,{"derivedFrom":[subQ1,subQ0]});Q38=makeQuery(id+"F0.imprint","IMPRINT",FACE,{"disambiguationData":[TD([[makeQuery(id+"F0.imprint","IMPRINT",EDGE,{"disambiguationData":[TD([[subQ2,-1.0]])],"derivedFrom":subQ1}),-1.0]])]});}
            var Q39;
            {var subQ0=sQuery(id+"F0.wireOp",EDGE,"E20");var subQ1=sQuery(id+"F0.wireOp",EDGE,"E10.trimOffspring");var subQ2=makeQuery(id+"F0.imprint","INTERSECT",VERTEX,{"derivedFrom":[subQ1,subQ0]});Q39=makeQuery(id+"F0.imprint","IMPRINT",FACE,{"disambiguationData":[TD([[makeQuery(id+"F0.imprint","IMPRINT",EDGE,{"disambiguationData":[TD([[subQ2,-1.0]])],"derivedFrom":subQ1}),1.0]])]});}
            var Q40;
            {var subQ0=sQuery(id+"F0.wireOp",EDGE,"E20");var subQ1=sQuery(id+"F0.wireOp",EDGE,"E13.trimOffspring");var subQ2=makeQuery(id+"F0.imprint","INTERSECT",VERTEX,{"derivedFrom":[subQ1,subQ0]});Q40=makeQuery(id+"F0.imprint","IMPRINT",FACE,{"disambiguationData":[TD([[makeQuery(id+"F0.imprint","IMPRINT",EDGE,{"disambiguationData":[TD([[subQ2,-1.0]])],"derivedFrom":subQ1}),1.0]])]});}
            var Q41;
            {var subQ0=sQuery(id+"F0.wireOp",EDGE,"E23.trimOffspring");var subQ1=sQuery(id+"F0.wireOp",EDGE,"E1");var subQ2=makeQuery(id+"F0.imprint","INTERSECT",VERTEX,{"derivedFrom":[subQ1,subQ0]});Q41=makeQuery(id+"F0.imprint","IMPRINT",FACE,{"disambiguationData":[TD([[makeQuery(id+"F0.imprint","IMPRINT",EDGE,{"disambiguationData":[TD([[subQ2,-1.0]])],"derivedFrom":subQ1}),-1.0]])]});}
            var Q42;
            {var subQ0=sQuery(id+"F0.wireOp",EDGE,"E21.3.0.0");var subQ1=sQuery(id+"F0.wireOp",EDGE,"E1");var subQ2=makeQuery(id+"F0.imprint","INTERSECT",VERTEX,{"derivedFrom":[subQ1,subQ0]});Q42=makeQuery(id+"F0.imprint","IMPRINT",FACE,{"disambiguationData":[TD([[makeQuery(id+"F0.imprint","IMPRINT",EDGE,{"disambiguationData":[TD([[subQ2,-1.0]])],"derivedFrom":subQ1}),1.0]])]});}
            var Q43;
            {var subQ0=sQuery(id+"F0.wireOp",EDGE,"E22.5.0.0");var subQ1=sQuery(id+"F0.wireOp",EDGE,"E3.trimOffspring");var subQ2=makeQuery(id+"F0.imprint","INTERSECT",VERTEX,{"derivedFrom":[subQ1,subQ0]});Q43=makeQuery(id+"F0.imprint","IMPRINT",FACE,{"disambiguationData":[TD([[makeQuery(id+"F0.imprint","IMPRINT",EDGE,{"disambiguationData":[TD([[subQ2,-1.0]])],"derivedFrom":subQ1}),1.0]])]});}
            var Q44;
            {var subQ0=sQuery(id+"F0.wireOp",EDGE,"E21.3.0.0");var subQ1=sQuery(id+"F0.wireOp",EDGE,"E6.trimOffspring");var subQ2=makeQuery(id+"F0.imprint","INTERSECT",VERTEX,{"derivedFrom":[subQ1,subQ0]});Q44=makeQuery(id+"F0.imprint","IMPRINT",FACE,{"disambiguationData":[TD([[makeQuery(id+"F0.imprint","IMPRINT",EDGE,{"disambiguationData":[TD([[subQ2,-1.0]])],"derivedFrom":subQ1}),1.0]])]});}
            extrude(context, id + "F3", {"entities" : qUnion([Q0, Q1, Q2, Q3, Q4, Q5, Q6, Q7, Q8, Q9, Q10, Q11, Q12, Q13, Q14, Q15, Q16, Q17, Q18, Q19, Q20, Q21, Q22, Q23, Q24, Q25, Q26, Q27, Q28, Q29, Q30, Q31, Q32, Q33, Q34, Q35, Q36, Q37, Q38, Q39, Q40, Q41, Q42, Q43, Q44]), "operationType" : NewBodyOperationType.REMOVE, "depth" : 25 * mm, "offsetDistance" : 25 * mm});
        }
    });
